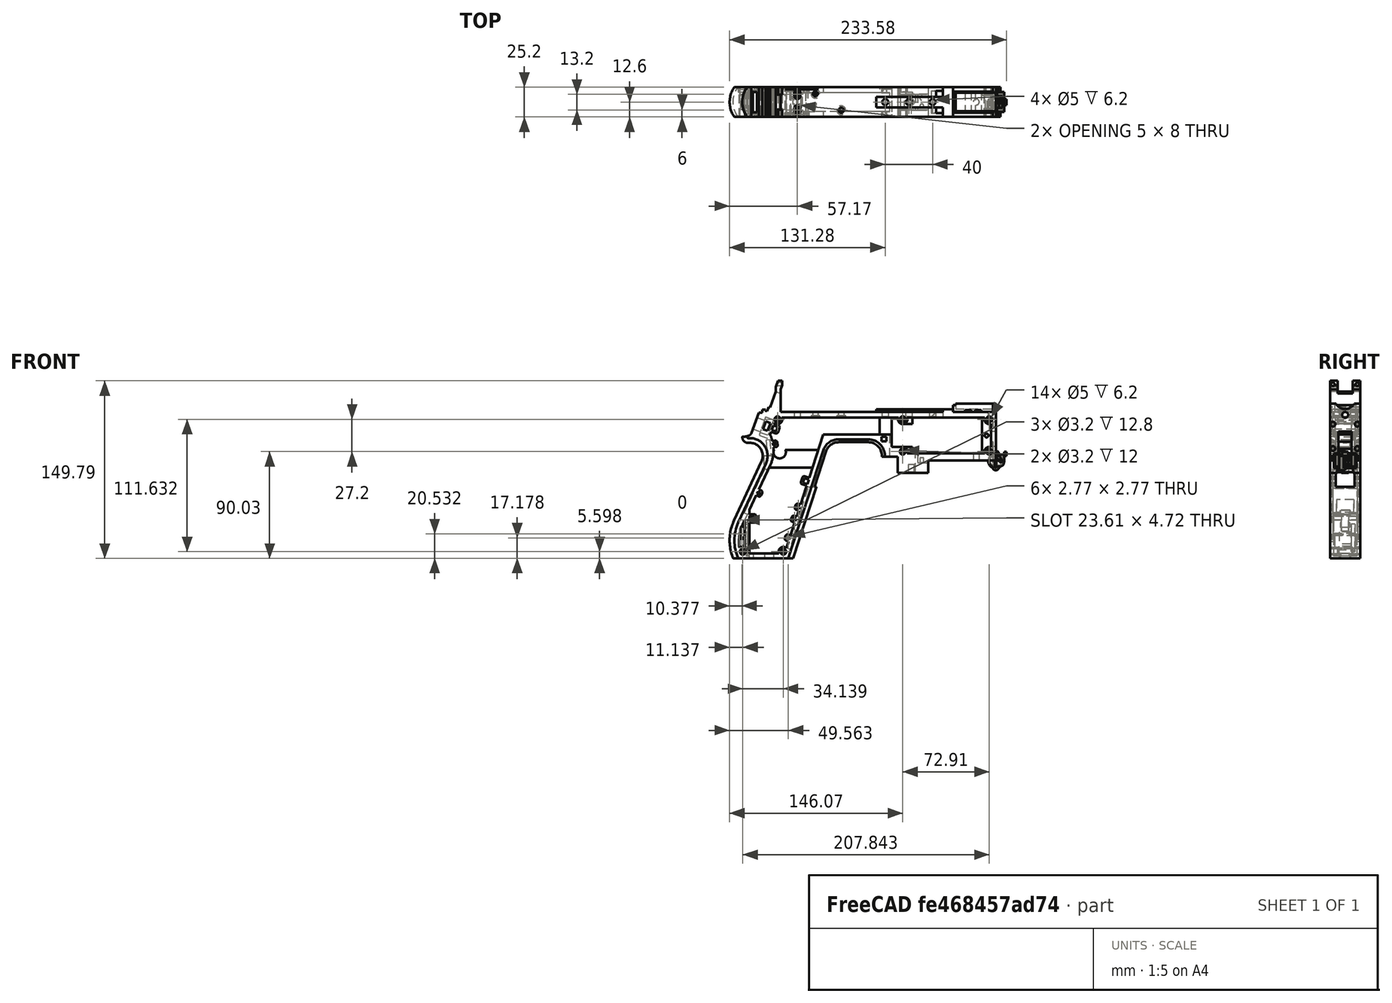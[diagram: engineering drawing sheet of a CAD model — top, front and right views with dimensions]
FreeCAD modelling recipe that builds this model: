
FCSTD DOCUMENT  (FreeCAD 1.0R39319 (Git))
Label: PICON-OF_ver_45
License: All rights reserved
LicenseURL: https://en.wikipedia.org/wiki/All_rights_reserved
objects: Sketcher::SketchObject×119, Part::Extrusion×62, Part::Cut×46, PartDesign::Pad×29, PartDesign::Pocket×18, PartDesign::Chamfer×15, PartDesign::Body×10, PartDesign::Fillet×6, Part::MultiFuse×4, PartDesign::SubtractivePipe×4, Part::Part2DObjectPython×4, PartDesign::SubtractiveLoft×4, PartDesign::Plane×2, PartDesign::SubShapeBinder×2, Part::Sweep×1, PartDesign::ShapeBinder×1, Mesh::Feature×1
note: 598 computed .brp shape members not serialized (recipe doc carries the construction recipe); baked Part::Feature solids carry a one-line shape summary decoded from their .brp

FEATURE [Sketcher::SketchObject] Sketch  label="corpo principale"
  ArcFitTolerance = 1e-06
  AttacherType = Attacher::AttachEngine3D
  AttachmentSupport = -> [XZ_Plane]
  FullyConstrained = true
  MakeInternals = false
  MapMode = 5
  Placement = pos=(0,0,0) rot=(1,0,0;1.5708rad)
  sketch-geometry (65):
    g0: LineSegment StartX=0 StartY=0 StartZ=0 EndX=-57.2 EndY=0 EndZ=0
    g1: LineSegment StartX=-57.2 StartY=0 StartZ=0 EndX=-57.2 EndY=-10.4 EndZ=0
    g2: LineSegment StartX=-57.2 StartY=-10.4 StartZ=0 EndX=-82.8 EndY=-10.4 EndZ=0
    g3: LineSegment StartX=-82.8 StartY=-10.4 StartZ=0 EndX=-82.8 EndY=3.2 EndZ=0
    g4: LineSegment StartX=-82.8 StartY=3.2 StartZ=0 EndX=-93.6 EndY=3.2 EndZ=0
    g5: LineSegment StartX=-93.6 StartY=3.2 StartZ=0 EndX=-93.6 EndY=4 EndZ=0
    g6: LineSegment StartX=-107.6 StartY=18 StartZ=0 EndX=-132.428 EndY=18 EndZ=0
    g7: LineSegment StartX=-145.743 StartY=8.32624 StartZ=0 EndX=-175.232 EndY=-82.4316 EndZ=0
    g8: LineSegment StartX=-175.232 StartY=-82.4316 StartZ=0 EndX=-217.232 EndY=-82.4316 EndZ=0
    g9: LineSegment StartX=-217.232 StartY=-52.1862 StartZ=0 EndX=-193.988 EndY=-2.33927 EndZ=0
    g10: LineSegment StartX=-206.196 StartY=23.0857 StartZ=0 EndX=-199.861 EndY=40.4914 EndZ=0
    g11: LineSegment StartX=-199.861 StartY=40.4914 StartZ=0 EndX=-197.061 EndY=40.4914 EndZ=0
    g12: LineSegment StartX=-197.061 StartY=40.4914 StartZ=0 EndX=-197.061 EndY=42.8914 EndZ=0
    g13: LineSegment StartX=-197.061 StartY=42.8914 StartZ=0 EndX=-194.261 EndY=42.8914 EndZ=0
    g14: LineSegment StartX=-194.261 StartY=42.8914 StartZ=0 EndX=-194.535 EndY=42.1397 EndZ=0
    g15: LineSegment StartX=-194.535 StartY=42.1397 StartZ=0 EndX=-193.031 EndY=41.5924 EndZ=0
    g16: LineSegment StartX=-193.031 StartY=41.5924 StartZ=0 EndX=-191.663 EndY=45.3512 EndZ=0
    g17: LineSegment StartX=-191.663 StartY=45.3512 StartZ=0 EndX=-190.536 EndY=44.9408 EndZ=0
    g18: LineSegment StartX=-190.536 StartY=44.9408 StartZ=0 EndX=-185.747 EndY=58.0965 EndZ=0
    g19: LineSegment StartX=-185.747 StartY=58.0965 StartZ=0 EndX=-185.747 EndY=62.0965 EndZ=0
    g20: LineSegment StartX=-185.747 StartY=62.0965 StartZ=0 EndX=-183.832 EndY=67.3588 EndZ=0
    g21: LineSegment StartX=-183.832 StartY=67.3588 StartZ=0 EndX=-180.232 EndY=67.3588 EndZ=0
    g22: LineSegment StartX=-180.232 StartY=67.3588 StartZ=0 EndX=-180.232 EndY=63.7588 EndZ=0
    g23: LineSegment StartX=-180.232 StartY=63.7588 StartZ=0 EndX=-181.6 EndY=60 EndZ=0
    g24: LineSegment StartX=-181.6 StartY=60 StartZ=0 EndX=-181.6 EndY=41.2 EndZ=0
    g25: LineSegment StartX=-181.6 StartY=41.2 StartZ=0 EndX=-100.8 EndY=41.2 EndZ=0
    g26: LineSegment StartX=-36 StartY=43.2 StartZ=0 EndX=-36 EndY=41.2 EndZ=0
    g27: LineSegment StartX=0 StartY=48 StartZ=0 EndX=0 EndY=0 EndZ=0
    g28: LineSegment StartX=-209.901 StartY=19.85 StartZ=0 EndX=-209.901 EndY=20.1 EndZ=0
    g29: LineSegment StartX=-208.001 StartY=22 StartZ=0 EndX=-207.747 EndY=22 EndZ=0
    g30: LineSegment StartX=-207.583 StartY=19 StartZ=0 EndX=-209.051 EndY=19 EndZ=0
    g31: ArcOfCircle CenterX=-208.001 CenterY=20.1 CenterZ=0 NormalX=0 NormalY=0 NormalZ=1 AngleXU=0 Radius=1.9 StartAngle=1.5708 EndAngle=3.14159
    g32: GeomPoint [constr] X=-209.901 Y=22 Z=0
    g33: ArcOfCircle CenterX=-209.051 CenterY=19.85 CenterZ=0 NormalX=0 NormalY=0 NormalZ=1 AngleXU=0 Radius=0.85 StartAngle=3.14159 EndAngle=4.71239
    g34: GeomPoint [constr] X=-209.901 Y=19 Z=0
    g35: ArcOfCircle CenterX=-207.747 CenterY=23.65 CenterZ=0 NormalX=0 NormalY=0 NormalZ=1 AngleXU=0 Radius=1.65 StartAngle=4.71239 EndAngle=5.93412
    g36: GeomPoint [constr] X=-206.591 Y=22 Z=0
    g37: LineSegment StartX=-4 StartY=6 StartZ=0 EndX=-4 EndY=36.4 EndZ=0
    g38: LineSegment StartX=-4 StartY=36.4 StartZ=0 EndX=-185.2 EndY=36.4 EndZ=0
    g39: LineSegment StartX=-185.2 StartY=36.4 StartZ=0 EndX=-190.441 EndY=22 EndZ=0
    g40: LineSegment StartX=-214.575 StartY=-78.4316 StartZ=0 EndX=-178.142 EndY=-78.4316 EndZ=0
    g41: LineSegment StartX=-178.142 StartY=-78.4316 StartZ=0 EndX=-145.51 EndY=22 EndZ=0
    g42: LineSegment StartX=-145.51 StartY=22 StartZ=0 EndX=-87.91 EndY=22 EndZ=0
    g43: LineSegment StartX=-87.91 StartY=22 StartZ=0 EndX=-87.91 EndY=11.6 EndZ=0
    g44: LineSegment StartX=-87.91 StartY=11.6 StartZ=0 EndX=-80.11 EndY=11.6 EndZ=0
    g45: LineSegment StartX=-80.11 StartY=11.6 StartZ=0 EndX=-80.11 EndY=6 EndZ=0
    g46: LineSegment StartX=-80.11 StartY=6 StartZ=0 EndX=-4 EndY=6 EndZ=0
    g47: LineSegment StartX=-190.363 StartY=-4.02975 StartZ=0 EndX=-213.607 EndY=-53.8767 EndZ=0
    g48: ArcOfCircle CenterX=-132.428 CenterY=4 CenterZ=0 NormalX=0 NormalY=0 NormalZ=1 AngleXU=0 Radius=14 StartAngle=1.5708 EndAngle=2.82743
    g49: GeomPoint [constr] X=-142.6 Y=18 Z=0
    g50: ArcOfCircle CenterX=-107.6 CenterY=4 CenterZ=0 NormalX=0 NormalY=0 NormalZ=1 AngleXU=0 Radius=14 StartAngle=0 EndAngle=1.5708
    g51: GeomPoint [constr] X=-93.6 Y=18 Z=0
    g52: ArcOfCircle CenterX=-184.801 CenterY=-67.3089 CenterZ=0 NormalX=0 NormalY=0 NormalZ=1 AngleXU=0 Radius=35.7833 StartAngle=2.70526 EndAngle=3.57792
    g53: ArcOfCircle CenterX=-207.583 CenterY=4 CenterZ=0 NormalX=0 NormalY=0 NormalZ=1 AngleXU=0 Radius=15 StartAngle=5.84685 EndAngle=7.85398
    g54: LineSegment [constr] StartX=-213.607 StartY=-53.8767 StartZ=0 EndX=-217.232 EndY=-52.1862 EndZ=0
    g55: ArcOfCircle CenterX=-184.801 CenterY=-67.3089 CenterZ=0 NormalX=0 NormalY=0 NormalZ=1 AngleXU=0 Radius=31.7833 StartAngle=2.70526 EndAngle=3.49911
    g56: ArcOfCircle CenterX=-218.095 CenterY=8.90192 CenterZ=0 NormalX=0 NormalY=0 NormalZ=1 AngleXU=0 Radius=30.5989 StartAngle=5.84685 EndAngle=6.72553
    g57: LineSegment StartX=-44.6 StartY=43.2 StartZ=0 EndX=-36 EndY=43.2 EndZ=0
    g58: LineSegment StartX=-100.8 StartY=41.2 StartZ=0 EndX=-44.6 EndY=41.2 EndZ=0
    g59: LineSegment StartX=-44.6 StartY=41.2 StartZ=0 EndX=-44.6 EndY=43.2 EndZ=0
    g60: LineSegment StartX=-2.4 StartY=48 StartZ=0 EndX=0 EndY=48 EndZ=0
    g61: LineSegment StartX=-36 StartY=41.2 StartZ=0 EndX=-2.4 EndY=41.2 EndZ=0
    g62: LineSegment StartX=-2.4 StartY=41.2 StartZ=0 EndX=-2.4 EndY=48 EndZ=0
    g63: LineSegment [constr] StartX=-181.6 StartY=36.4 StartZ=0 EndX=-152.209 EndY=36.4 EndZ=0
    g64: LineSegment [constr] StartX=-181.6 StartY=36.4 StartZ=0 EndX=-130.41 EndY=36.4 EndZ=0
  constraints (183):
    c: Coincident(g-1,g0)
    c: PointOnObject(g0,g-1)
    c: Coincident(g0,g1)
    c: Vertical(g1)
    c: Coincident(g1,g2)
    c: Horizontal(g2)
    c: Coincident(g2,g3)
    c: Vertical(g3)
    c: Coincident(g3,g4)
    c: Coincident(g4,g5)
    c: Vertical(g5)
    c: Horizontal(g6)
    c: Coincident(g7,g8)
    c: Horizontal(g8)
    c: Coincident(g10,g11)
    c: Horizontal(g11)
    c: Coincident(g11,g12)
    c: Vertical(g12)
    c: Coincident(g12,g13)
    c: Horizontal(g13)
    c: Coincident(g13,g14)
    c: Coincident(g14,g15)
    c: Coincident(g15,g16)
    c: Coincident(g16,g17)
    c: Coincident(g17,g18)
    c: Coincident(g18,g19)
    c: Vertical(g19)
    c: Coincident(g19,g20)
    c: Coincident(g20,g21)
    c: Horizontal(g21)
    c: Coincident(g21,g22)
    c: Vertical(g22)
    c: Coincident(g22,g23)
    c: Coincident(g23,g24)
    c: Vertical(g24)
    c: Coincident(g24,g25)
    c: Horizontal(g25)
    c: Coincident(g57,g26)
    c: Vertical(g26)
    c: Coincident(g26,g61)
    c: PointOnObject(g60,g-2)
    c: Coincident(g60,g27)
    c: Coincident(g27,g0)
    c: DistanceY(g27,g27) = 48
    c: DistanceY(g1,g1) = 10.4
    c: DistanceX(g0,g0) = 57.2
    c: DistanceX(g2,g2) = 25.6
    c: Horizontal(g4)
    c: DistanceY(g3,g3) = 13.6
    c: DistanceX(g4,g4) = 10.8
    c: DistanceY(g5,g51) = 14.8
    c: DistanceX(g49,g51) = 49
    c: Distance(g7,g49) = 105.6
    c: DistanceX(g61,g60) = 36
    c: DistanceX(g25,g25) = 80.8
    c: DistanceY(g24,g24) = 18.8
    c: DistanceY(g22,g22) = 3.6
    c: Distance(g23) = 4
    c: Angle(g-1,g23) = 1.22173
    c: DistanceX(g21,g21) = 3.6
    c: Distance(g20) = 5.6
    c: Angle(g-1,g20) = 1.22173
    c: DistanceY(g19,g19) = 4
    c: Distance(g18) = 14
    c: Angle(g-1,g18) = 1.22173
    c: Distance(g17) = 1.2
    c: Distance(g16) = 4
    c: Angle(g16) = 1.22173
    c: Perpendicular(g18,g17)
    c: Distance(g15) = 1.6
    c: Perpendicular(g16,g15)
    c: Distance(g14) = 0.8
    c: DistanceX(g13,g13) = 2.8
    c: Perpendicular(g15,g14)
    c: DistanceY(g12,g12) = 2.4
    c: DistanceX(g11,g11) = 2.8
    c: Distance(g9) = 55
    c: Angle(g9,g-1) = 2.00713
    c: Horizontal(g29)
    c: Vertical(g28)
    c: Horizontal(g30)
    c: PointOnObject(g32,g29)
    c: PointOnObject(g32,g28)
    c: Tangent(g29,g31) = 1.5708
    c: Tangent(g28,g31) = 1.5708
    c: PointOnObject(g34,g28)
    c: PointOnObject(g34,g30)
    c: Tangent(g28,g33) = 1.5708
    c: Tangent(g30,g33) = 1.5708
    c: PointOnObject(g36,g29)
    c: PointOnObject(g36,g10)
    c: Tangent(g29,g35) = -1.5708
    c: Tangent(g10,g35) = -1.5708
    c: Angle(g-1,g10) = 1.22173
    c: Radius(g35) = 1.65
    c: Vertical(g37)
    c: Coincident(g37,g38)
    c: Horizontal(g38)
    c: Coincident(g38,g39)
    c: Horizontal(g40)
    c: Coincident(g40,g41)
    c: Coincident(g41,g42)
    c: Horizontal(g42)
    c: Coincident(g42,g43)
    c: Vertical(g43)
    c: Coincident(g43,g44)
    c: Horizontal(g44)
    c: Coincident(g44,g45)
    c: Vertical(g45)
    c: Coincident(g45,g46)
    c: Coincident(g46,g37)
    c: Horizontal(g46)
    c: DistanceY(g0,g37) = 6
    c: DistanceX(g37,g0) = 4
    c: DistanceY(g37,g25) = 4.8
    c: DistanceX(g38,g38) = 181.2
    c: DistanceX(g42,g42) = 57.6
    c: DistanceY(g49,g41) = 4
    c: DistanceX(g41,g49) = 2.91
    c: DistanceY(g43,g43) = 10.4
    c: DistanceX(g44,g44) = 7.8
    c: DistanceY(g7,g40) = 4
    c: Distance(g47) = 55
    c: Angle(g-1,g39) = 1.22173
    c: PointOnObject(g49,g7)
    c: PointOnObject(g49,g6)
    c: Tangent(g7,g48) = -1.5708
    c: Tangent(g6,g48) = -1.5708
    c: PointOnObject(g51,g5)
    c: PointOnObject(g51,g6)
    c: Tangent(g5,g50) = -1.5708
    c: Tangent(g6,g50) = -1.5708
    c: Radius(g50) = 14
    c: Radius(g48) = 14
    c: DistanceX(g8,g8) = 42
    c: Angle(g7,g-1) = 1.88496
    c: Parallel(g41,g7)
    c: Parallel(g47,g9)
    c: Coincident(g52,g8)
    c: Tangent(g52,g9) = 1.5708
    c: DistanceX(g9,g8) = 0
    c: Tangent(g53,g9) = -1.5708
    c: Tangent(g53,g30) = -1.5708
    c: Diameter(g53) = 30
    c: DistanceY(g53,g0) = -4
    c: Coincident(g54,g47)
    c: Distance(g54) = 4
    c: Coincident(g54,g9)
    c: Coincident(g55,g40)
    c: Tangent(g55,g47) = -1.5708
    c: Coincident(g52,g55)
    c: Coincident(g56,g39)
    c: Tangent(g56,g47) = 1.5708
    c: Horizontal(g57)
    c: DistanceX(g57,g57) = 8.6
    c: Coincident(g58,g25)
    c: Horizontal(g58)
    c: Coincident(g59,g58)
    c: Vertical(g59)
    c: DistanceY(g58,g57) = 2
    c: DistanceX(g58,g58) = 56.2
    c: Coincident(g59,g57)
    c: DistanceY(g41,g36) = 0
    c: DistanceY(g36,g39) = 0
    c: DistanceY(g28,g28) = 0.25
    c: DistanceX(g30,g36) = 2.46
    c: DistanceX(g28,g29) = 1.9
    c: Coincident(g62,g60)
    c: Horizontal(g60)
    c: DistanceX(g62,g27) = 2.4
    c: Coincident(g61,g62)
    c: DistanceY(g26,g26) = 2
    c: Vertical(g62)
    c: DistanceY(g61,g60) = 6.8
    c: Horizontal(g61)
    c: Distance(g63) = 29.391
    c: PointOnObject(g63,g38)
    c: PointOnObject(g63,g38)
    c: Distance(g64) = 51.19
    c: PointOnObject(g64,g38)
    c: PointOnObject(g64,g38)
    c: DistanceX(g24,g63) = 0
    c: DistanceX(g24,g64) = 0
FEATURE [Part::Extrusion] Extrude  label="Extrude corpo principale"
  Base = -> Sketch
  Dir = (0,-1,2e-16)
  DirMode = 2
  FaceMakerClass = Part::FaceMakerBullseye
  FaceMakerMode = 3
  LengthFwd = 25.2
  LengthRev = 12.6
  Solid = true
  Symmetric = true
FEATURE [Sketcher::SketchObject] Sketch002  label="scavo grilletto"
  ArcFitTolerance = 1e-06
  AttachmentSupport = -> [XZ_Plane]
  ExternalGeometry = -> [Sketch]
  FullyConstrained = true
  MakeInternals = false
  MapMode = 5
  Placement = pos=(0,0,0) rot=(1,0,0;1.5708rad)
  sketch-geometry (4):
    g0: LineSegment StartX=-89.51 StartY=22 StartZ=0 EndX=-152.71 EndY=22 EndZ=0
    g1: LineSegment StartX=-152.71 StartY=22 StartZ=0 EndX=-167.006 EndY=-22 EndZ=0
    g2: LineSegment StartX=-167.006 StartY=-22 StartZ=0 EndX=-89.51 EndY=-22 EndZ=0
    g3: LineSegment StartX=-89.51 StartY=-22 StartZ=0 EndX=-89.51 EndY=22 EndZ=0
  constraints (12):
    c: Horizontal(g0)
    c: Coincident(g0,g1)
    c: Coincident(g1,g2)
    c: Horizontal(g2)
    c: Coincident(g2,g3)
    c: Coincident(g3,g0)
    c: Vertical(g3)
    c: Angle(g1,g0) = 1.88496
    c: DistanceY(g3,g3) = 44
    c: DistanceX(g0,g0) = 63.2
    c: DistanceX(g0,g-3) = 1.6
    c: DistanceY(g-3,g0) = 0
FEATURE [Sketcher::SketchObject] Sketch004  label="traiettoria arrotondamento impugnatura anteriore"
  ArcFitTolerance = 1e-06
  AttachmentSupport = -> [XZ_Plane]
  ExternalGeometry = -> [Sketch]
  FullyConstrained = true
  MakeInternals = false
  MapMode = 5
  Placement = pos=(0,0,0) rot=(1,0,0;1.5708rad)
  sketch-geometry (13):
    g0: LineSegment StartX=-175.232 StartY=-82.4316 StartZ=0 EndX=-145.743 EndY=8.32624 EndZ=0
    g1: LineSegment StartX=-93.6 StartY=3.2 StartZ=0 EndX=-93.6 EndY=4 EndZ=0
    g2: LineSegment StartX=-132.428 StartY=18 StartZ=0 EndX=-107.6 EndY=18 EndZ=0
    g3: ArcOfCircle CenterX=-132.428 CenterY=4 CenterZ=0 NormalX=0 NormalY=0 NormalZ=1 AngleXU=0 Radius=14 StartAngle=1.5708 EndAngle=2.82743
    g4: ArcOfCircle CenterX=-107.6 CenterY=4 CenterZ=0 NormalX=0 NormalY=0 NormalZ=1 AngleXU=0 Radius=14 StartAngle=0 EndAngle=1.5708
    g5: LineSegment StartX=-175.232 StartY=-82.4316 StartZ=0 EndX=-217.232 EndY=-82.4316 EndZ=0
    g6: LineSegment StartX=-217.232 StartY=-52.1862 StartZ=0 EndX=-193.988 EndY=-2.33927 EndZ=0
    g7: LineSegment StartX=-209.051 StartY=19 StartZ=0 EndX=-207.583 EndY=19 EndZ=0
    g8: LineSegment StartX=-209.901 StartY=20.1 StartZ=0 EndX=-209.901 EndY=19.85 EndZ=0
    g9: ArcOfCircle CenterX=-184.801 CenterY=-67.3089 CenterZ=0 NormalX=0 NormalY=0 NormalZ=1 AngleXU=0 Radius=35.7833 StartAngle=2.70526 EndAngle=3.57792
    g10: ArcOfCircle CenterX=-207.583 CenterY=4 CenterZ=0 NormalX=0 NormalY=0 NormalZ=1 AngleXU=0 Radius=15 StartAngle=5.84685 EndAngle=7.85398
    g11: ArcOfCircle CenterX=-209.051 CenterY=19.85 CenterZ=0 NormalX=0 NormalY=0 NormalZ=1 AngleXU=0 Radius=0.85 StartAngle=3.14159 EndAngle=4.71239
    g12: ArcOfCircle CenterX=-208.001 CenterY=20.1 CenterZ=0 NormalX=0 NormalY=0 NormalZ=1 AngleXU=0 Radius=1.9 StartAngle=1.5708 EndAngle=3.14159
  constraints (26):
    c: Coincident(g0,g-3)
    c: Coincident(g0,g-6)
    c: Coincident(g1,g-8)
    c: Coincident(g1,g-7)
    c: Coincident(g2,g-5)
    c: Coincident(g2,g-4)
    c: Coincident(g3,g2)
    c: Tangent(g3,g0) = 1.5708
    c: Coincident(g4,g1)
    c: Tangent(g4,g2) = 1.5708
    c: Coincident(g5,g0)
    c: Coincident(g5,g-9)
    c: Coincident(g6,g-12)
    c: Coincident(g6,g-11)
    c: Coincident(g7,g-15)
    c: Coincident(g7,g-14)
    c: Coincident(g8,g-16)
    c: Coincident(g8,g-17)
    c: Tangent(g9,g6) = 1.5708
    c: Coincident(g9,g5)
    c: Coincident(g10,g7)
    c: Tangent(g10,g6) = -1.5708
    c: Tangent(g11,g7) = -1.5708
    c: Coincident(g11,g8)
    c: Tangent(g12,g8) = -1.5708
    c: Coincident(g12,g-17)
FEATURE [PartDesign::Plane] DatumPlane  label="Piano per disegno arrotondamento impugnatura"
  AttachmentSupport = -> [Sketch]
  Length = 73.6581
  MapMode = 7
  Placement = pos=(-145.743,1.8e-15,8.32624) rot=(0.154555,0.154555,0.97582;1.59527rad)
  ResizeMode = 0
  Width = 303.511
FEATURE [Sketcher::SketchObject] Sketch005  label="forma arrotondamento impugnatura anteriore"
  ArcFitTolerance = 1e-06
  AttachmentSupport = -> [DatumPlane]
  FullyConstrained = true
  MakeInternals = false
  MapMode = 5
  Placement = pos=(-145.743,1.8e-15,8.32624) rot=(0.154555,0.154555,0.97582;1.59527rad)
  sketch-geometry (5):
    g0: GeomPoint [constr] X=0 Y=-4 Z=0
    g1: GeomPoint [constr] X=-12.6 Y=7.1e-15 Z=0
    g2: GeomPoint [constr] X=12.6 Y=4.97e-14 Z=0
    g3: LineSegment StartX=-12.6 StartY=7.1e-15 StartZ=0 EndX=12.6 EndY=4.97e-14 EndZ=0
    g4: ArcOfCircle CenterX=-3.88e-14 CenterY=17.845 CenterZ=0 NormalX=0 NormalY=0 NormalZ=1 AngleXU=0 Radius=21.845 StartAngle=4.09759 EndAngle=5.32718
  constraints (11):
    c: DistanceY(g0,g-1) = 4
    c: DistanceX(g-1,g0) = 0
    c: DistanceX(g1,g-1) = 12.6
    c: DistanceX(g-1,g2) = 12.6
    c: DistanceY(g-1,g2) = 0
    c: DistanceY(g-1,g1) = 0
    c: Coincident(g3,g1)
    c: Coincident(g3,g2)
    c: Coincident(g4,g1)
    c: Coincident(g4,g2)
    c: PointOnObject(g0,g4)
FEATURE [Part::Sweep] Sweep  label="Sweep impugnatura"
  Frenet = true
  Sections = -> [Sketch005]
  Solid = true
  Spine = -> Sketch [Edge32,Edge33,Edge34,Edge35,Edge36,Edge37,Edge38,Edge39,Edge40,Edge41,Edge42,Edge43,Edge44]
  Transition = 1
FEATURE [Sketcher::SketchObject] Sketch008  label="buchi e pulizie varie"
  ArcFitTolerance = 1e-06
  AttachmentSupport = -> [XZ_Plane]
  ExternalGeometry = -> [Sketch]
  FullyConstrained = true
  MakeInternals = false
  MapMode = 5
  Placement = pos=(0,0,0) rot=(1,0,0;1.5708rad)
  sketch-geometry (26):
    g0: LineSegment StartX=-96.278 StartY=20.155 StartZ=0 EndX=-92.278 EndY=20.155 EndZ=0
    g1: LineSegment StartX=-92.278 StartY=20.155 StartZ=0 EndX=-92.278 EndY=16.155 EndZ=0
    g2: LineSegment StartX=-92.278 StartY=16.155 StartZ=0 EndX=-96.278 EndY=16.155 EndZ=0
    g3: LineSegment StartX=-96.278 StartY=16.155 StartZ=0 EndX=-96.278 EndY=20.155 EndZ=0
    g4: LineSegment StartX=-222.232 StartY=-82.4316 StartZ=0 EndX=-170.232 EndY=-82.4316 EndZ=0
    g5: LineSegment StartX=-170.232 StartY=-82.4316 StartZ=0 EndX=-170.232 EndY=-86.4316 EndZ=0
    g6: LineSegment StartX=-170.232 StartY=-86.4316 StartZ=0 EndX=-222.232 EndY=-86.4316 EndZ=0
    g7: LineSegment StartX=-222.232 StartY=-86.4316 StartZ=0 EndX=-222.232 EndY=-82.4316 EndZ=0
    g8: LineSegment StartX=-213.901 StartY=20.1 StartZ=0 EndX=-213.901 EndY=26 EndZ=0
    g9: LineSegment StartX=-213.901 StartY=26 StartZ=0 EndX=-206.196 EndY=26 EndZ=0
    g10: LineSegment StartX=-17.4 StartY=42.8 StartZ=0 EndX=-12.4 EndY=42.8 EndZ=0
    g11: LineSegment StartX=-12.4 StartY=42.8 StartZ=0 EndX=-12.4 EndY=41.2 EndZ=0
    g12: LineSegment StartX=-12.4 StartY=41.2 StartZ=0 EndX=-17.4 EndY=41.2 EndZ=0
    g13: LineSegment StartX=-17.4 StartY=41.2 StartZ=0 EndX=-17.4 EndY=42.8 EndZ=0
    g14: LineSegment StartX=-25.9 StartY=42.8 StartZ=0 EndX=-20.9 EndY=42.8 EndZ=0
    g15: LineSegment StartX=-20.9 StartY=42.8 StartZ=0 EndX=-20.9 EndY=41.2 EndZ=0
    g16: LineSegment StartX=-20.9 StartY=41.2 StartZ=0 EndX=-25.9 EndY=41.2 EndZ=0
    g17: LineSegment StartX=-25.9 StartY=41.2 StartZ=0 EndX=-25.9 EndY=42.8 EndZ=0
    g18: GeomPoint [constr] X=-206.196 Y=23.0857 Z=0
    g19: GeomPoint [constr] X=-213.901 Y=20.1 Z=0
    g20: BSplineCurve PolesCount=4 KnotsCount=2 Degree=3 IsPeriodic=0
    g21-g24: Circle [constr] x4 (B-spline internal-alignment scaffolding for g20; pole/knot coordinates omitted)
    g25: LineSegment StartX=-206.196 StartY=26 StartZ=0 EndX=-206.196 EndY=23.0857 EndZ=0
  constraints (73):
    c: Horizontal(g0)
    c: Coincident(g1,g0)
    c: Vertical(g1)
    c: Coincident(g2,g1)
    c: Horizontal(g2)
    c: Coincident(g3,g2)
    c: Coincident(g3,g0)
    c: Vertical(g3)
    c: DistanceX(g0,g-4) = 4.368
    c: DistanceY(g0,g-4) = 1.845
    c: DistanceY(g1,g1) = 4
    c: DistanceX(g2,g2) = 4
    c: Horizontal(g4)
    c: Coincident(g5,g4)
    c: Vertical(g5)
    c: Coincident(g6,g5)
    c: Horizontal(g6)
    c: Coincident(g7,g6)
    c: Coincident(g7,g4)
    c: Vertical(g7)
    c: DistanceY(g7,g7) = 4
    c: DistanceX(g4,g-5) = 5
    c: DistanceX(g-5,g4) = 5
    c: DistanceY(g4,g-5) = 0
    c: Coincident(g9,g8)
    c: Parallel(g9,g-6)
    c: DistanceX(g8,g-8) = 4
    c: Horizontal(g10)
    c: Coincident(g11,g10)
    c: Vertical(g11)
    c: Coincident(g12,g11)
    c: Horizontal(g12)
    c: Coincident(g13,g12)
    c: Coincident(g13,g10)
    c: Vertical(g13)
    c: Horizontal(g14)
    c: Coincident(g15,g14)
    c: Vertical(g15)
    c: Coincident(g16,g15)
    c: Horizontal(g16)
    c: Coincident(g17,g16)
    c: Coincident(g17,g14)
    c: Vertical(g17)
    c: DistanceY(g11,g10) = 1.6
    c: DistanceX(g10,g10) = 5
    c: DistanceY(g15,g14) = 1.6
    c: DistanceX(g14,g14) = 5
    c: DistanceX(g15,g12) = 3.5
    c: DistanceX(g11,g-9) = 10
    c: DistanceY(g-9,g11) = 0
    c: DistanceY(g-9,g15) = 0
    c: Perpendicular(g8,g9)
    c: DistanceY(g-7,g9) = 4
    c: DistanceY(g8,g-8) = 0
    c: InternalAlignment(g18,g20)
    c: InternalAlignment(g19,g20)
    c: InternalAlignment(g21,g20)
    c: Weight(g21) = 1
    c: InternalAlignment(g22,g20)
    c: Equal(g22,g21)
    c: InternalAlignment(g23,g20)
    c: Equal(g23,g21)
    c: InternalAlignment(g24,g20)
    c: Equal(g24,g21)
    c: Coincident(g18,g-12)
    c: Coincident(g19,g8)
    c: Coincident(g25,g9)
    c: Coincident(g25,g20)
    c: Vertical(g25)
    c: DistanceY(g20,g23) = 0
    c: DistanceY(g22,g18) = 2.26
    c: DistanceX(g22,g18) = 0.93
    c: DistanceX(g20,g23) = 2.9
FEATURE [Part::Extrusion] Extrude004  label="Extrude Buchi e pulizie varie"
  Base = -> Sketch008
  Dir = (0,-1,2e-16)
  DirMode = 2
  FaceMakerClass = Part::FaceMakerBullseye
  FaceMakerMode = 3
  LengthFwd = 25.2
  LengthRev = 0
  Solid = true
  Symmetric = true
FEATURE [Sketcher::SketchObject] Sketch009  label="rinforzi"
  ArcFitTolerance = 1e-06
  AttachmentSupport = -> [XZ_Plane]
  ExternalGeometry = -> [Sketch]
  FullyConstrained = true
  MakeInternals = false
  MapMode = 5
  Placement = pos=(0,0,0) rot=(1,0,0;1.5708rad)
  sketch-geometry (9):
    g0: LineSegment StartX=-87.91 StartY=22 StartZ=0 EndX=-87.91 EndY=36.4 EndZ=0
    g1: LineSegment StartX=-87.91 StartY=36.4 StartZ=0 EndX=-97.91 EndY=36.4 EndZ=0
    g2: LineSegment StartX=-97.91 StartY=36.4 StartZ=0 EndX=-97.91 EndY=22 EndZ=0
    g3: LineSegment StartX=-97.91 StartY=22 StartZ=0 EndX=-87.91 EndY=22 EndZ=0
    g4: LineSegment StartX=-149.713 StartY=9.06563 StartZ=0 EndX=-154.586 EndY=-5.93437 EndZ=0
    g5: LineSegment StartX=-154.586 StartY=-5.93437 StartZ=0 EndX=-191.863 EndY=-5.93437 EndZ=0
    g6: LineSegment StartX=-191.863 StartY=-5.93437 StartZ=0 EndX=-191.863 EndY=9.06563 EndZ=0
    g7: LineSegment StartX=-191.863 StartY=9.06563 StartZ=0 EndX=-149.713 EndY=9.06563 EndZ=0
    g8: LineSegment [constr] StartX=-145.51 StartY=22 StartZ=0 EndX=-149.713 EndY=9.06563 EndZ=0
  constraints (25):
    c: Vertical(g0)
    c: Coincident(g1,g0)
    c: Horizontal(g1)
    c: Coincident(g2,g1)
    c: Vertical(g2)
    c: Coincident(g3,g2)
    c: Coincident(g3,g0)
    c: Horizontal(g3)
    c: Coincident(g0,g-4)
    c: DistanceX(g3,g3) = 10
    c: DistanceY(g0,g-3) = 0
    c: Coincident(g5,g4)
    c: Horizontal(g5)
    c: Coincident(g6,g5)
    c: Vertical(g6)
    c: Coincident(g7,g6)
    c: Coincident(g7,g4)
    c: Horizontal(g7)
    c: Distance(g8) = 13.6
    c: Parallel(g-6,g8)
    c: Coincident(g-6,g8)
    c: Parallel(g4,g-6)
    c: DistanceY(g4,g4) = 15
    c: Coincident(g4,g8)
    c: DistanceX(g-5,g5) = -1.5
FEATURE [Part::Extrusion] Extrude001  label="Extrude scavo grilletto"
  Base = -> Sketch002
  Dir = (0,-1,2e-16)
  DirMode = 2
  FaceMakerClass = Part::FaceMakerBullseye
  FaceMakerMode = 3
  LengthFwd = 16
  LengthRev = 0
  Solid = true
  Symmetric = true
FEATURE [Part::Extrusion] Extrude005  label="Extrude Rinforzi"
  Base = -> Sketch009
  Dir = (0,-1,2e-16)
  DirMode = 2
  FaceMakerClass = Part::FaceMakerBullseye
  FaceMakerMode = 3
  LengthFwd = 2
  LengthRev = 0
  Placement = pos=(0,12.6,0) rot=(0,0,1;0rad)
  Solid = true
  Symmetric = false
FEATURE [PartDesign::ShapeBinder] CopyCut
  TraceSupport = false
FEATURE [PartDesign::Plane] DatumPlane001
  AttachmentSupport = -> [CopyCut]
  Length = 283.944
  MapMode = 5
  Placement = pos=(0,12.6,0) rot=(0,0.707107,0.707107;3.14159rad)
  ResizeMode = 0
  Width = 188.15
FEATURE [Sketcher::SketchObject] Sketch010  label="buco neopixel"
  ArcFitTolerance = 1e-06
  AttachmentSupport = -> [XZ_Plane]
  ExternalGeometry = -> [Sketch]
  FullyConstrained = true
  MakeInternals = false
  MapMode = 5
  Placement = pos=(0,0,0) rot=(1,0,0;1.5708rad)
  sketch-geometry (5):
    g0: LineSegment [constr] StartX=-199.861 StartY=40.4914 StartZ=0 EndX=-201.368 EndY=36.3521 EndZ=0
    g1: LineSegment StartX=-201.368 StartY=36.3521 StartZ=0 EndX=-204.932 EndY=26.5605 EndZ=0
    g2: LineSegment StartX=-201.368 StartY=36.3521 StartZ=0 EndX=-180.2 EndY=28.6477 EndZ=0
    g3: LineSegment StartX=-180.2 StartY=28.6477 StartZ=0 EndX=-183.764 EndY=18.8561 EndZ=0
    g4: LineSegment StartX=-183.764 StartY=18.8561 StartZ=0 EndX=-204.932 EndY=26.5605 EndZ=0
  constraints (14):
    c: Parallel(g0,g-3)
    c: Distance(g0) = 4.405
    c: Coincident(g0,g-3)
    c: Coincident(g2,g1)
    c: Coincident(g3,g2)
    c: Coincident(g4,g3)
    c: Coincident(g4,g1)
    c: Parallel(g1,g-3)
    c: Distance(g1) = 10.42
    c: Coincident(g1,g0)
    c: Parallel(g2,g4)
    c: Perpendicular(g1,g2)
    c: DistanceX(g-4,g2) = 5
    c: Parallel(g3,g1)
FEATURE [Part::Extrusion] Extrude006  label="Extrude buco neopixel"
  Base = -> Sketch010
  Dir = (0,-1,2e-16)
  DirMode = 2
  FaceMakerClass = Part::FaceMakerBullseye
  FaceMakerMode = 3
  LengthFwd = 17.2
  LengthRev = 0
  Solid = true
  Symmetric = true
FEATURE [Sketcher::SketchObject] Sketch011  label="fermo grilletto"
  ArcFitTolerance = 1e-06
  AttachmentSupport = -> [XZ_Plane]
  ExternalGeometry = -> [Sketch]
  FullyConstrained = true
  MakeInternals = false
  MapMode = 5
  Placement = pos=(0,0,0) rot=(1,0,0;1.5708rad)
  sketch-geometry (18):
    g0: LineSegment [constr] StartX=-145.51 StartY=22 StartZ=0 EndX=-157.347 EndY=-14.4293 EndZ=0
    g1: LineSegment [constr] StartX=-157.347 StartY=-14.4293 StartZ=0 EndX=-157.841 EndY=-15.951 EndZ=0
    g2: LineSegment StartX=-161.151 StartY=-13.1932 StartZ=0 EndX=-155.825 EndY=-14.9237 EndZ=0
    g3: LineSegment StartX=-163.167 StartY=-14.2205 StartZ=0 EndX=-164.403 EndY=-18.0247 EndZ=0
    g4: LineSegment StartX=-163.376 StartY=-20.0408 StartZ=0 EndX=-158.05 EndY=-21.7713 EndZ=0
    g5: LineSegment StartX=-158.05 StartY=-21.7713 StartZ=0 EndX=-155.825 EndY=-14.9237 EndZ=0
    g6: LineSegment StartX=-161.645 StartY=-14.7149 StartZ=0 EndX=-157.841 EndY=-15.951 EndZ=0
    g7: LineSegment StartX=-157.841 StartY=-15.951 StartZ=0 EndX=-159.077 EndY=-19.7552 EndZ=0
    g8: LineSegment StartX=-159.077 StartY=-19.7552 StartZ=0 EndX=-162.881 EndY=-18.5191 EndZ=0
    g9: LineSegment StartX=-162.881 StartY=-18.5191 StartZ=0 EndX=-161.645 EndY=-14.7149 EndZ=0
    g10: LineSegment [constr] StartX=-161.645 StartY=-14.7149 StartZ=0 EndX=-161.151 EndY=-13.1932 EndZ=0
    g11: LineSegment [constr] StartX=-159.077 StartY=-19.7552 StartZ=0 EndX=-157.555 EndY=-20.2496 EndZ=0
    g12: LineSegment [constr] StartX=-159.077 StartY=-19.7552 StartZ=0 EndX=-159.572 EndY=-21.2769 EndZ=0
    g13: LineSegment [constr] StartX=-161.645 StartY=-14.7149 StartZ=0 EndX=-163.167 EndY=-14.2205 EndZ=0
    g14: ArcOfCircle CenterX=-161.645 CenterY=-14.7149 CenterZ=0 NormalX=0 NormalY=0 NormalZ=1 AngleXU=0 Radius=1.6 StartAngle=1.25664 EndAngle=2.82743
    g15: GeomPoint [constr] X=-162.673 Y=-12.6988 Z=0
    g16: ArcOfCircle CenterX=-162.881 CenterY=-18.5191 CenterZ=0 NormalX=0 NormalY=0 NormalZ=1 AngleXU=0 Radius=1.6 StartAngle=2.82743 EndAngle=4.39823
    g17: GeomPoint [constr] X=-164.897 Y=-19.5464 Z=0
  constraints (48):
    c: Parallel(g0,g-3)
    c: Distance(g0) = 38.304
    c: Coincident(g0,g-3)
    c: Parallel(g1,g-3)
    c: Distance(g1) = 1.6
    c: Coincident(g1,g0)
    c: Coincident(g5,g4)
    c: Coincident(g5,g2)
    c: Coincident(g7,g6)
    c: Coincident(g8,g7)
    c: Coincident(g9,g8)
    c: Coincident(g9,g6)
    c: Parallel(g7,g-3)
    c: Parallel(g9,g7)
    c: Perpendicular(g6,g7)
    c: Parallel(g6,g8)
    c: Distance(g6) = 4
    c: Distance(g9) = 4
    c: Parallel(g5,g7)
    c: Parallel(g9,g3)
    c: Parallel(g2,g6)
    c: Parallel(g4,g8)
    c: Parallel(g13,g6)
    c: Parallel(g10,g9)
    c: Parallel(g11,g8)
    c: Parallel(g12,g7)
    c: Distance(g10) = 1.6
    c: Distance(g13) = 1.6
    c: Distance(g12) = 1.6
    c: Distance(g11) = 1.6
    c: Coincident(g10,g6)
    c: Coincident(g13,g6)
    c: Coincident(g12,g7)
    c: Coincident(g11,g7)
    c: Distance(g10,g15) = 1.6
    c: Distance(g15,g13) = 1.6
    c: Distance(g4,g12) = 1.6
    c: Distance(g4,g11) = 1.6
    c: PointOnObject(g15,g2)
    c: Tangent(g3,g14) = -1.5708
    c: Tangent(g2,g14) = 1.5708
    c: PointOnObject(g17,g4)
    c: PointOnObject(g17,g3)
    c: Tangent(g4,g16) = -1.5708
    c: Tangent(g3,g16) = -1.5708
    c: Equal(g16,g14)
    c: Coincident(g16,g8)
    c: Coincident(g6,g1)
FEATURE [Part::Extrusion] Extrude007  label="Extrude fermo grilletto"
  Base = -> Sketch011
  Dir = (0,-1,2e-16)
  DirMode = 2
  FaceMakerClass = Part::FaceMakerBullseye
  FaceMakerMode = 3
  LengthFwd = 25.2
  LengthRev = 0
  Solid = true
  Symmetric = true
FEATURE [Sketcher::SketchObject] Sketch012  label="buco oled"
  ArcFitTolerance = 1e-06
  AttachmentSupport = -> [XZ_Plane]
  ExternalGeometry = -> [Sketch]
  FullyConstrained = true
  MakeInternals = false
  MapMode = 5
  Placement = pos=(0,0,0) rot=(1,0,0;1.5708rad)
  sketch-geometry (4):
    g0: LineSegment StartX=-185.747 StartY=58.0965 StartZ=0 EndX=-180.232 EndY=56.0891 EndZ=0
    g1: LineSegment StartX=-185.747 StartY=58.0965 StartZ=0 EndX=-185.747 EndY=67.3588 EndZ=0
    g2: LineSegment StartX=-185.747 StartY=67.3588 StartZ=0 EndX=-180.232 EndY=67.3588 EndZ=0
    g3: LineSegment StartX=-180.232 StartY=67.3588 StartZ=0 EndX=-180.232 EndY=56.0891 EndZ=0
  constraints (10):
    c: Coincident(g1,g0)
    c: Coincident(g2,g1)
    c: Coincident(g3,g2)
    c: Coincident(g3,g0)
    c: Parallel(g1,g-5)
    c: Perpendicular(g-3,g0)
    c: Parallel(g2,g-6)
    c: Parallel(g3,g-4)
    c: Coincident(g0,g-5)
    c: Coincident(g2,g-6)
FEATURE [Part::Extrusion] Extrude008  label="Extrude buco oled"
  Base = -> Sketch012
  Dir = (0,-1,2e-16)
  DirMode = 2
  FaceMakerClass = Part::FaceMakerBullseye
  FaceMakerMode = 3
  LengthFwd = 12.8
  LengthRev = 0
  Solid = true
  Symmetric = true
FEATURE [Sketcher::SketchObject] Sketch013  label="buco pompa"
  ArcFitTolerance = 1e-06
  AttachmentSupport = -> [XZ_Plane]
  ExternalGeometry = -> [Sketch]
  FullyConstrained = true
  MakeInternals = false
  MapMode = 5
  Placement = pos=(0,0,0) rot=(1,0,0;1.5708rad)
  sketch-geometry (8):
    g0: LineSegment StartX=-82.8 StartY=-10.4 StartZ=0 EndX=-82.8 EndY=-9.6 EndZ=0
    g1: LineSegment StartX=-82.8 StartY=-9.6 StartZ=0 EndX=-67.9 EndY=-9.6 EndZ=0
    g2: LineSegment StartX=-67.9 StartY=-9.6 StartZ=0 EndX=-67.9 EndY=6 EndZ=0
    g3: LineSegment StartX=-67.9 StartY=6 StartZ=0 EndX=-65.9 EndY=6 EndZ=0
    g4: LineSegment StartX=-65.9 StartY=6 StartZ=0 EndX=-65.9 EndY=-1.7 EndZ=0
    g5: LineSegment StartX=-65.9 StartY=-1.7 StartZ=0 EndX=-57.2 EndY=-1.7 EndZ=0
    g6: LineSegment StartX=-57.2 StartY=-1.7 StartZ=0 EndX=-57.2 EndY=-10.4 EndZ=0
    g7: LineSegment StartX=-57.2 StartY=-10.4 StartZ=0 EndX=-82.8 EndY=-10.4 EndZ=0
  constraints (22):
    c: Vertical(g0)
    c: Coincident(g1,g0)
    c: Horizontal(g1)
    c: Coincident(g2,g1)
    c: Vertical(g2)
    c: Coincident(g3,g2)
    c: Horizontal(g3)
    c: Coincident(g4,g3)
    c: Vertical(g4)
    c: Coincident(g5,g4)
    c: Horizontal(g5)
    c: Coincident(g6,g5)
    c: Vertical(g6)
    c: Coincident(g7,g6)
    c: Coincident(g7,g0)
    c: DistanceY(g0,g0) = 0.8
    c: DistanceY(g6,g6) = 8.7
    c: DistanceX(g1,g1) = 14.9
    c: DistanceX(g3,g3) = 2
    c: Coincident(g0,g-4)
    c: DistanceY(g2,g-6) = 0
    c: Coincident(g6,g-5)
FEATURE [Part::Extrusion] Extrude009  label="Extrude buco pompa"
  Base = -> Sketch013
  Dir = (0,-1,2e-16)
  DirMode = 2
  FaceMakerClass = Part::FaceMakerBullseye
  FaceMakerMode = 3
  LengthFwd = 13.2
  LengthRev = 0
  Solid = true
  Symmetric = true
FEATURE [Sketcher::SketchObject] Sketch014  label="buco frontale"
  ArcFitTolerance = 1e-06
  AttachmentSupport = -> [XZ_Plane]
  ExternalGeometry = -> [Sketch]
  FullyConstrained = true
  MakeInternals = false
  MapMode = 5
  Placement = pos=(0,0,0) rot=(1,0,0;1.5708rad)
  sketch-geometry (10):
    g0: LineSegment StartX=0 StartY=0 StartZ=0 EndX=0 EndY=24.671 EndZ=0
    g1: LineSegment StartX=0 StartY=24.671 StartZ=0 EndX=-4 EndY=24.671 EndZ=0
    g2: LineSegment StartX=-4 StartY=24.671 StartZ=0 EndX=-4 EndY=16 EndZ=0
    g3: LineSegment StartX=-4 StartY=16 StartZ=0 EndX=-2.4 EndY=16 EndZ=0
    g4: LineSegment StartX=-2.4 StartY=16 StartZ=0 EndX=-2.4 EndY=10 EndZ=0
    g5: LineSegment StartX=-2.4 StartY=10 StartZ=0 EndX=-12 EndY=10 EndZ=0
    g6: LineSegment StartX=-12 StartY=10 StartZ=0 EndX=-12 EndY=6 EndZ=0
    g7: LineSegment StartX=-12 StartY=6 StartZ=0 EndX=-2.4 EndY=6 EndZ=0
    g8: LineSegment StartX=-2.4 StartY=6 StartZ=0 EndX=-2.4 EndY=0 EndZ=0
    g9: LineSegment StartX=-2.4 StartY=0 StartZ=0 EndX=0 EndY=0 EndZ=0
  constraints (29):
    c: Vertical(g0)
    c: Coincident(g1,g0)
    c: Horizontal(g1)
    c: Coincident(g2,g1)
    c: Vertical(g2)
    c: Coincident(g3,g2)
    c: Horizontal(g3)
    c: Coincident(g4,g3)
    c: Vertical(g4)
    c: Coincident(g5,g4)
    c: Horizontal(g5)
    c: Coincident(g6,g5)
    c: Vertical(g6)
    c: Coincident(g7,g6)
    c: Coincident(g8,g7)
    c: Vertical(g8)
    c: Coincident(g9,g8)
    c: Coincident(g9,g0)
    c: Horizontal(g9)
    c: DistanceY(g0,g0) = 24.671
    c: Horizontal(g7)
    c: DistanceY(g6,g6) = 4
    c: DistanceY(g4,g4) = 6
    c: DistanceX(g9,g9) = 2.4
    c: Coincident(g0,g-1)
    c: DistanceY(g-3,g7) = 0
    c: DistanceX(g8,g4) = 0
    c: DistanceX(g-3,g1) = 0
    c: DistanceX(g6,g-3) = 8
FEATURE [Part::Extrusion] Extrude010  label="Extrude buco frontale"
  Base = -> Sketch014
  Dir = (0,-1,2e-16)
  DirMode = 2
  FaceMakerClass = Part::FaceMakerBullseye
  FaceMakerMode = 3
  LengthFwd = 11.2
  LengthRev = 0
  Solid = true
  Symmetric = true
FEATURE [Sketcher::SketchObject] Sketch015  label="guida rail"
  ArcFitTolerance = 1e-06
  AttachmentSupport = -> [XZ_Plane]
  ExternalGeometry = -> [Sketch]
  FullyConstrained = true
  MakeInternals = false
  MapMode = 5
  Placement = pos=(0,0,0) rot=(1,0,0;1.5708rad)
  sketch-geometry (4):
    g0: LineSegment StartX=-100.8 StartY=43.2 StartZ=0 EndX=-44.6 EndY=43.2 EndZ=0
    g1: LineSegment StartX=-44.6 StartY=43.2 StartZ=0 EndX=-44.6 EndY=41.2 EndZ=0
    g2: LineSegment StartX=-44.6 StartY=41.2 StartZ=0 EndX=-100.8 EndY=41.2 EndZ=0
    g3: LineSegment StartX=-100.8 StartY=41.2 StartZ=0 EndX=-100.8 EndY=43.2 EndZ=0
  constraints (9):
    c: Horizontal(g0)
    c: Coincident(g1,g0)
    c: Coincident(g2,g1)
    c: Coincident(g3,g2)
    c: Coincident(g3,g0)
    c: Vertical(g3)
    c: Coincident(g2,g-3)
    c: Coincident(g1,g-3)
    c: Coincident(g0,g-4)
FEATURE [Part::Extrusion] Extrude011  label="Extrude guida rail"
  Base = -> Sketch015
  Dir = (0,-1,2e-16)
  DirMode = 2
  FaceMakerClass = Part::FaceMakerBullseye
  FaceMakerMode = 3
  LengthFwd = 9
  LengthRev = 0
  Solid = true
  Symmetric = true
FEATURE [Sketcher::SketchObject] Sketch016  label="guide per coperture laterali"
  ArcFitTolerance = 1e-06
  AttachmentSupport = -> [XZ_Plane]
  ExternalGeometry = -> [Sketch]
  FullyConstrained = true
  MakeInternals = false
  MapMode = 5
  Placement = pos=(0,0,0) rot=(1,0,0;1.5708rad)
  sketch-geometry (14):
    g0: Circle CenterX=-5.6 CenterY=7.6 CenterZ=0 NormalX=0 NormalY=0 NormalZ=1 AngleXU=0 Radius=1.6
    g1: Circle CenterX=-5.6 CenterY=7.6 CenterZ=0 NormalX=0 NormalY=0 NormalZ=1 AngleXU=0 Radius=4
    g2: Circle CenterX=-5.6 CenterY=34.8 CenterZ=0 NormalX=0 NormalY=0 NormalZ=1 AngleXU=0 Radius=1.6
    g3: Circle CenterX=-5.6 CenterY=34.8 CenterZ=0 NormalX=0 NormalY=0 NormalZ=1 AngleXU=0 Radius=4
    g4: Circle CenterX=-184.08 CenterY=34.8 CenterZ=0 NormalX=0 NormalY=0 NormalZ=1 AngleXU=0 Radius=1.6
    g5: Circle CenterX=-184.08 CenterY=34.8 CenterZ=0 NormalX=0 NormalY=0 NormalZ=1 AngleXU=0 Radius=4
    g6: Circle CenterX=-179.305 CenterY=-76.8316 CenterZ=0 NormalX=0 NormalY=0 NormalZ=1 AngleXU=0 Radius=1.6
    g7: Circle CenterX=-179.305 CenterY=-76.8316 CenterZ=0 NormalX=0 NormalY=0 NormalZ=1 AngleXU=0 Radius=4
    g8: Circle CenterX=-213.443 CenterY=-76.8316 CenterZ=0 NormalX=0 NormalY=0 NormalZ=1 AngleXU=0 Radius=1.6
    g9: Circle CenterX=-213.443 CenterY=-76.8316 CenterZ=0 NormalX=0 NormalY=0 NormalZ=1 AngleXU=0 Radius=4
    g10: Circle CenterX=-78.51 CenterY=7.6 CenterZ=0 NormalX=0 NormalY=0 NormalZ=1 AngleXU=0 Radius=1.6
    g11: Circle CenterX=-78.51 CenterY=7.6 CenterZ=0 NormalX=0 NormalY=0 NormalZ=1 AngleXU=0 Radius=4
    g12: Circle CenterX=-78.51 CenterY=34.8 CenterZ=0 NormalX=0 NormalY=0 NormalZ=1 AngleXU=0 Radius=1.6
    g13: Circle CenterX=-78.51 CenterY=34.8 CenterZ=0 NormalX=0 NormalY=0 NormalZ=1 AngleXU=0 Radius=4
  constraints (35):
    c: Diameter(g0) = 3.2
    c: Diameter(g1) = 8
    c: Coincident(g0,g1)
    c: Diameter(g2) = 3.2
    c: Diameter(g3) = 8
    c: Coincident(g3,g2)
    c: Tangent(g2,g-7)
    c: Diameter(g4) = 3.2
    c: Diameter(g5) = 8
    c: Coincident(g5,g4)
    c: Tangent(g4,g-7)
    c: Tangent(g4,g-8)
    c: Diameter(g6) = 3.2
    c: Diameter(g7) = 8
    c: Coincident(g7,g6)
    c: Tangent(g6,g-9)
    c: Tangent(g6,g-10)
    c: Diameter(g8) = 3.2
    c: Diameter(g9) = 8
    c: Coincident(g9,g8)
    c: Tangent(g8,g-10)
    c: Tangent(g8,g-11)
    c: Diameter(g10) = 3.2
    c: Diameter(g11) = 8
    c: Diameter(g12) = 3.2
    c: Diameter(g13) = 8
    c: Coincident(g12,g13)
    c: Coincident(g10,g11)
    c: Tangent(g12,g-7)
    c: DistanceX(g12,g10) = 0
    c: Tangent(g2,g-6)
    c: Tangent(g0,g-6)
    c: Tangent(g0,g-3)
    c: Tangent(g10,g-3)
    c: Tangent(g10,g-4)
FEATURE [Part::Extrusion] Extrude012  label="extrude guide per coperture laterali"
  Base = -> Sketch016
  Dir = (0,-1,2e-16)
  DirMode = 2
  FaceMakerClass = Part::FaceMakerBullseye
  FaceMakerMode = 3
  LengthFwd = 25.2
  LengthRev = 0
  Solid = true
  Symmetric = true
FEATURE [Sketcher::SketchObject] Sketch017  label="supporto CAM"
  ArcFitTolerance = 1e-06
  AttachmentSupport = -> [XZ_Plane]
  ExternalGeometry = -> [Sketch]
  FullyConstrained = true
  MakeInternals = false
  MapMode = 5
  Placement = pos=(0,0,0) rot=(1,0,0;1.5708rad)
  sketch-geometry (6):
    g0: LineSegment StartX=-2.4 StartY=48 StartZ=0 EndX=-2.4 EndY=41.2 EndZ=0
    g1: LineSegment StartX=-2.4 StartY=48 StartZ=0 EndX=-34 EndY=48 EndZ=0
    g2: LineSegment StartX=-34 StartY=48 StartZ=0 EndX=-34 EndY=46.72 EndZ=0
    g3: LineSegment StartX=-34 StartY=46.72 StartZ=0 EndX=-36 EndY=46.72 EndZ=0
    g4: LineSegment StartX=-36 StartY=46.72 StartZ=0 EndX=-36 EndY=41.2 EndZ=0
    g5: LineSegment StartX=-36 StartY=41.2 StartZ=0 EndX=-2.4 EndY=41.2 EndZ=0
  constraints (15):
    c: Coincident(g1,g0)
    c: Horizontal(g1)
    c: Coincident(g2,g1)
    c: Vertical(g2)
    c: Coincident(g3,g2)
    c: Horizontal(g3)
    c: Coincident(g4,g3)
    c: Coincident(g5,g4)
    c: DistanceX(g1,g0) = 31.6
    c: Coincident(g5,g0)
    c: Vertical(g4)
    c: DistanceY(g2,g1) = 1.28
    c: Coincident(g0,g-3)
    c: Coincident(g0,g-3)
    c: Coincident(g4,g-4)
FEATURE [Part::Extrusion] Extrude013  label="Extrude supporto CAM"
  Base = -> Sketch017
  Dir = (0,-1,2e-16)
  DirMode = 2
  FaceMakerClass = Part::FaceMakerBullseye
  FaceMakerMode = 3
  LengthFwd = 17.8
  LengthRev = 0
  Solid = true
  Symmetric = true
FEATURE [Sketcher::SketchObject] Sketch018  label="Scavo CAM"
  ArcFitTolerance = 1e-06
  AttachmentSupport = -> [YZ_Plane]
  ExternalGeometry = -> [Sketch]
  FullyConstrained = true
  MakeInternals = false
  MapMode = 5
  Placement = pos=(0,0,0) rot=(0.57735,0.57735,0.57735;2.0944rad)
  sketch-geometry (4):
    g0: LineSegment StartX=-7.73 StartY=48 StartZ=0 EndX=7.73 EndY=48 EndZ=0
    g1: LineSegment [constr] StartX=1.07e-14 StartY=48 StartZ=0 EndX=0 EndY=43.5155 EndZ=0
    g2: ArcOfCircle CenterX=9e-15 CenterY=52.42 CenterZ=0 NormalX=0 NormalY=0 NormalZ=1 AngleXU=0 Radius=8.90445 StartAngle=3.66102 EndAngle=5.76376
    g3: Circle [constr] CenterX=9e-15 CenterY=52.42 CenterZ=0 NormalX=0 NormalY=0 NormalZ=1 AngleXU=0 Radius=8.9
  constraints (13):
    c: Horizontal(g0)
    c: DistanceY(g-3,g0) = 0
    c: DistanceX(g0,g0) = 15.46
    c: DistanceX(g0,g-3) = 7.73
    c: DistanceX(g-3) = 0
    c: Coincident(g1,g-3)
    c: PointOnObject(g1,g-2)
    c: Coincident(g2,g0)
    c: Coincident(g2,g0)
    c: PointOnObject(g1,g2)
    c: Diameter(g3) = 17.8
    c: DistanceY(g1,g3) = 4.42
    c: Coincident(g2,g3)
FEATURE [Part::Extrusion] Extrude014  label="Extrude Scavo CAM"
  Base = -> Sketch018
  Dir = (1,0,0)
  DirMode = 2
  FaceMakerClass = Part::FaceMakerBullseye
  FaceMakerMode = 3
  LengthFwd = -34
  LengthRev = 0
  Solid = true
  Symmetric = false
FEATURE [Sketcher::SketchObject] Sketch019  label="scavo rumble"
  ArcFitTolerance = 1e-06
  AttachmentSupport = -> [XZ_Plane]
  ExternalGeometry = -> [Sketch]
  FullyConstrained = true
  MakeInternals = false
  MapMode = 5
  Placement = pos=(0,0,0) rot=(1,0,0;1.5708rad)
  sketch-geometry (6):
    g0: LineSegment StartX=-163.771 StartY=-21.9058 StartZ=0 EndX=-158.636 EndY=-23.5745 EndZ=0
    g1: LineSegment StartX=-158.636 StartY=-23.5745 StartZ=0 EndX=-165.743 EndY=-45.4488 EndZ=0
    g2: LineSegment StartX=-165.743 StartY=-45.4488 StartZ=0 EndX=-170.879 EndY=-43.7801 EndZ=0
    g3: LineSegment StartX=-170.879 StartY=-43.7801 StartZ=0 EndX=-163.771 EndY=-21.9058 EndZ=0
    g4: LineSegment [constr] StartX=-145.51 StartY=22 StartZ=0 EndX=-160.157 EndY=-23.0801 EndZ=0
    g5: LineSegment [constr] StartX=-158.636 StartY=-23.5745 StartZ=0 EndX=-160.157 EndY=-23.0801 EndZ=0
  constraints (17):
    c: Coincident(g1,g0)
    c: Coincident(g2,g1)
    c: Coincident(g3,g2)
    c: Coincident(g3,g0)
    c: Parallel(g3,g-3)
    c: Parallel(g3,g1)
    c: Perpendicular(g3,g0)
    c: Perpendicular(g2,g3)
    c: Distance(g2,g0) = 23
    c: Parallel(g4,g-3)
    c: Distance(g4) = 47.4
    c: Coincident(g4,g-3)
    c: Parallel(g5,g0)
    c: Distance(g5) = 1.6
    c: Coincident(g5,g0)
    c: Distance(g5,g0) = 3.8
    c: Coincident(g5,g4)
FEATURE [Part::Extrusion] Extrude015  label="scavo rumble001"
  Base = -> Sketch019
  Dir = (0,-1,2e-16)
  DirMode = 2
  FaceMakerClass = Part::FaceMakerBullseye
  FaceMakerMode = 3
  LengthFwd = 21
  LengthRev = 0
  Solid = true
  Symmetric = true
FEATURE [Sketcher::SketchObject] Sketch020  label="fermo rumble"
  ArcFitTolerance = 1e-06
  AttachmentSupport = -> [XZ_Plane]
  ExternalGeometry = -> [Sketch019,Sketch]
  FullyConstrained = true
  MakeInternals = false
  MapMode = 5
  Placement = pos=(0,0,0) rot=(1,0,0;1.5708rad)
  sketch-geometry (16):
    g0: LineSegment [constr] StartX=-165.905 StartY=-40.7697 StartZ=0 EndX=-167.265 EndY=-44.9544 EndZ=0
    g1: LineSegment [constr] StartX=-167.265 StartY=-44.9544 StartZ=0 EndX=-165.743 EndY=-45.4488 EndZ=0
    g2: LineSegment StartX=-167.318 StartY=-37.9976 StartZ=0 EndX=-165.225 EndY=-38.6774 EndZ=0
    g3: LineSegment StartX=-165.225 StartY=-38.6774 StartZ=0 EndX=-165.905 EndY=-40.7697 EndZ=0
    g4: LineSegment StartX=-165.905 StartY=-40.7697 StartZ=0 EndX=-167.997 EndY=-40.0899 EndZ=0
    g5: LineSegment StartX=-167.997 StartY=-40.0899 StartZ=0 EndX=-167.318 EndY=-37.9976 EndZ=0
    g6: LineSegment StartX=-166.823 StartY=-36.4759 StartZ=0 EndX=-163.399 EndY=-37.5883 EndZ=0
    g7: LineSegment StartX=-163.399 StartY=-37.5883 StartZ=0 EndX=-165.006 EndY=-42.5338 EndZ=0
    g8: LineSegment StartX=-165.006 StartY=-42.5338 StartZ=0 EndX=-168.43 EndY=-41.4214 EndZ=0
    g9: LineSegment StartX=-169.457 StartY=-39.4053 StartZ=0 EndX=-168.839 EndY=-37.5031 EndZ=0
    g10: LineSegment [constr] StartX=-168.839 StartY=-37.5031 StartZ=0 EndX=-168.345 EndY=-35.9815 EndZ=0
    g11: LineSegment [constr] StartX=-168.345 StartY=-35.9815 StartZ=0 EndX=-166.823 EndY=-36.4759 EndZ=0
    g12: ArcOfCircle CenterX=-167.936 CenterY=-39.8997 CenterZ=0 NormalX=0 NormalY=0 NormalZ=1 AngleXU=0 Radius=1.6 StartAngle=2.82743 EndAngle=4.39823
    g13: GeomPoint [constr] X=-169.952 Y=-40.9269 Z=0
    g14: ArcOfCircle CenterX=-167.318 CenterY=-37.9976 CenterZ=0 NormalX=0 NormalY=0 NormalZ=1 AngleXU=0 Radius=1.6 StartAngle=1.25664 EndAngle=2.82743
    g15: GeomPoint [constr] X=-168.345 Y=-35.9815 Z=0
  constraints (42):
    c: Parallel(g0,g-4)
    c: Distance(g0) = 4.4
    c: Coincident(g1,g0)
    c: Perpendicular(g0,g1)
    c: Distance(g1) = 1.6
    c: Coincident(g1,g-5)
    c: Coincident(g3,g2)
    c: Coincident(g4,g3)
    c: Coincident(g5,g4)
    c: Coincident(g5,g2)
    c: Parallel(g3,g-4)
    c: Parallel(g3,g5)
    c: Perpendicular(g2,g3)
    c: Parallel(g4,g2)
    c: Distance(g2) = 2.2
    c: Distance(g3) = 2.2
    c: Coincident(g7,g6)
    c: Coincident(g8,g7)
    c: Parallel(g7,g-4)
    c: Parallel(g7,g9)
    c: Perpendicular(g6,g7)
    c: Parallel(g6,g8)
    c: Distance(g6,g15) = 5.2
    c: Distance(g7) = 5.2
    c: Coincident(g11,g10)
    c: Parallel(g10,g9)
    c: Parallel(g11,g6)
    c: Distance(g10) = 1.6
    c: Distance(g11) = 1.6
    c: Coincident(g10,g15)
    c: Distance(g11,g2) = 1.6
    c: Distance(g2,g10) = 1.6
    c: PointOnObject(g13,g8)
    c: PointOnObject(g13,g9)
    c: Tangent(g8,g12) = 1.5708
    c: Tangent(g9,g12) = 1.5708
    c: PointOnObject(g15,g9)
    c: Tangent(g6,g14) = 1.5708
    c: Tangent(g9,g14) = 1.5708
    c: Equal(g12,g14)
    c: Coincident(g6,g11)
    c: Coincident(g3,g0)
FEATURE [Part::Extrusion] Extrude016  label="Extrude fermo rumble"
  Base = -> Sketch020
  Dir = (0,-1,2e-16)
  DirMode = 2
  FaceMakerClass = Part::FaceMakerBullseye
  FaceMakerMode = 3
  LengthFwd = 25.2
  LengthRev = 0
  Solid = true
  Symmetric = true
FEATURE [Sketcher::SketchObject] Sketch021  label="perno fermo rumble001"
  ArcFitTolerance = 1e-06
  AttachmentSupport = -> [XZ_Plane001]
  FullyConstrained = true
  MakeInternals = false
  MapMode = 5
  Placement = pos=(0,0,0) rot=(1,0,0;1.5708rad)
  sketch-geometry (16):
    g0: LineSegment StartX=0 StartY=0.45 StartZ=0 EndX=0 EndY=1.55 EndZ=0
    g1: LineSegment StartX=0.45 StartY=2 StartZ=0 EndX=1.55 EndY=2 EndZ=0
    g2: LineSegment StartX=2 StartY=1.55 StartZ=0 EndX=2 EndY=0.45 EndZ=0
    g3: LineSegment StartX=1.55 StartY=0 StartZ=0 EndX=0.45 EndY=0 EndZ=0
    g4: ArcOfCircle [constr] CenterX=0.45 CenterY=1.55 CenterZ=0 NormalX=0 NormalY=0 NormalZ=1 AngleXU=0 Radius=0.45 StartAngle=1.5708 EndAngle=3.14159
    g5: GeomPoint [constr] X=0 Y=2 Z=0
    g6: LineSegment StartX=0.45 StartY=2 StartZ=0 EndX=0 EndY=1.55 EndZ=0
    g7: ArcOfCircle [constr] CenterX=1.55 CenterY=1.55 CenterZ=0 NormalX=0 NormalY=0 NormalZ=1 AngleXU=0 Radius=0.45 StartAngle=0 EndAngle=1.5708
    g8: GeomPoint [constr] X=2 Y=2 Z=0
    g9: LineSegment StartX=2 StartY=1.55 StartZ=0 EndX=1.55 EndY=2 EndZ=0
    g10: ArcOfCircle [constr] CenterX=1.55 CenterY=0.45 CenterZ=0 NormalX=0 NormalY=0 NormalZ=1 AngleXU=0 Radius=0.45 StartAngle=4.71239 EndAngle=6.28319
    g11: GeomPoint [constr] X=2 Y=0 Z=0
    g12: LineSegment StartX=1.55 StartY=0 StartZ=0 EndX=2 EndY=0.45 EndZ=0
    g13: ArcOfCircle [constr] CenterX=0.45 CenterY=0.45 CenterZ=0 NormalX=0 NormalY=0 NormalZ=1 AngleXU=0 Radius=0.45 StartAngle=3.14159 EndAngle=4.71239
    g14: GeomPoint [constr] X=0 Y=0 Z=0
    g15: LineSegment StartX=0 StartY=0.45 StartZ=0 EndX=0.45 EndY=0 EndZ=0
  constraints (35):
    c: Coincident(g14,g-1)
    c: PointOnObject(g5,g-2)
    c: Horizontal(g1)
    c: Vertical(g2)
    c: Horizontal(g3)
    c: DistanceX(g5,g8) = 2
    c: DistanceY(g11,g8) = 2
    c: PointOnObject(g5,g0)
    c: PointOnObject(g5,g1)
    c: Tangent(g0,g4) = 1.5708
    c: Tangent(g1,g4) = 1.5708
    c: Coincident(g6,g0)
    c: Coincident(g6,g1)
    c: PointOnObject(g8,g2)
    c: PointOnObject(g8,g1)
    c: Tangent(g2,g7) = 1.5708
    c: Tangent(g1,g7) = 1.5708
    c: Coincident(g9,g2)
    c: Coincident(g9,g1)
    c: PointOnObject(g11,g2)
    c: PointOnObject(g11,g3)
    c: Tangent(g2,g10) = 1.5708
    c: Tangent(g3,g10) = 1.5708
    c: Coincident(g12,g2)
    c: Coincident(g12,g3)
    c: PointOnObject(g14,g0)
    c: PointOnObject(g14,g3)
    c: Tangent(g0,g13) = 1.5708
    c: Tangent(g3,g13) = 1.5708
    c: Coincident(g15,g0)
    c: Coincident(g15,g3)
    c: Equal(g6,g9)
    c: Equal(g9,g12)
    c: Equal(g12,g15)
    c: DistanceX(g14,g3) = 0.45
FEATURE [Sketcher::SketchObject] Sketch022  label="fori per M3x5(OD)x6(L)"
  ArcFitTolerance = 1e-06
  AttachmentSupport = -> [XZ_Plane]
  ExternalGeometry = -> [Sketch016]
  FullyConstrained = true
  MakeInternals = false
  MapMode = 5
  Placement = pos=(0,0,0) rot=(1,0,0;1.5708rad)
  sketch-geometry (7):
    g0: Circle CenterX=-5.6 CenterY=34.8 CenterZ=0 NormalX=0 NormalY=0 NormalZ=1 AngleXU=0 Radius=2.5
    g1: Circle CenterX=-5.6 CenterY=7.6 CenterZ=0 NormalX=0 NormalY=0 NormalZ=1 AngleXU=0 Radius=2.5
    g2: Circle CenterX=-78.51 CenterY=34.8 CenterZ=0 NormalX=0 NormalY=0 NormalZ=1 AngleXU=0 Radius=2.5
    g3: Circle CenterX=-78.51 CenterY=7.6 CenterZ=0 NormalX=0 NormalY=0 NormalZ=1 AngleXU=0 Radius=2.5
    g4: Circle CenterX=-184.08 CenterY=34.8 CenterZ=0 NormalX=0 NormalY=0 NormalZ=1 AngleXU=0 Radius=2.5
    g5: Circle CenterX=-179.305 CenterY=-76.8316 CenterZ=0 NormalX=0 NormalY=0 NormalZ=1 AngleXU=0 Radius=2.5
    g6: Circle CenterX=-213.443 CenterY=-76.8316 CenterZ=0 NormalX=0 NormalY=0 NormalZ=1 AngleXU=0 Radius=2.5
  constraints (14):
    c: Diameter(g0) = 5
    c: Diameter(g1) = 5
    c: Diameter(g2) = 5
    c: Diameter(g3) = 5
    c: Diameter(g4) = 5
    c: Diameter(g5) = 5
    c: Diameter(g6) = 5
    c: Coincident(g0,g-8)
    c: Coincident(g1,g-9)
    c: Coincident(g2,g-6)
    c: Coincident(g3,g-7)
    c: Coincident(g4,g-5)
    c: Coincident(g5,g-4)
    c: Coincident(g6,g-3)
FEATURE [Part::Extrusion] Extrude018  label="Extrude fori M3x5x6 - dx"
  Base = -> Sketch022
  Dir = (0,-1,2e-16)
  DirMode = 2
  FaceMakerClass = Part::FaceMakerBullseye
  FaceMakerMode = 3
  LengthFwd = 6.2
  LengthRev = 0
  Placement = pos=(0,-9.5,0) rot=(0,0,1;0rad)
  Solid = true
  Symmetric = true
FEATURE [Part::Extrusion] Extrude019  label="Extrude fori M3x5x6 - sx"
  Base = -> Sketch022
  Dir = (0,-1,2e-16)
  DirMode = 2
  FaceMakerClass = Part::FaceMakerBullseye
  FaceMakerMode = 3
  LengthFwd = 6.2
  LengthRev = 0
  Placement = pos=(0,9.5,0) rot=(0,0,1;0rad)
  Solid = true
  Symmetric = true
FEATURE [Sketcher::SketchObject] Sketch023  label="foro anteriore M3x5x6"
  ArcFitTolerance = 1e-06
  AttachmentSupport = -> [YZ_Plane]
  FullyConstrained = true
  MakeInternals = false
  MapMode = 5
  Placement = pos=(0,0,0) rot=(0.57735,0.57735,0.57735;2.0944rad)
  sketch-geometry (2):
    g0: LineSegment [constr] StartX=0 StartY=0 StartZ=0 EndX=0 EndY=38.6 EndZ=0
    g1: Circle CenterX=0 CenterY=38.6 CenterZ=0 NormalX=0 NormalY=0 NormalZ=1 AngleXU=0 Radius=2.5
  constraints (5):
    c: Coincident(g0,g-1)
    c: PointOnObject(g0,g-2)
    c: DistanceY(g0,g0) = 38.6
    c: Diameter(g1) = 5
    c: Coincident(g1,g0)
FEATURE [Part::Extrusion] Extrude020  label="Extrude foro anteriore M3x5x6"
  Base = -> Sketch023
  Dir = (1,0,0)
  DirMode = 2
  FaceMakerClass = Part::FaceMakerBullseye
  FaceMakerMode = 3
  LengthFwd = -6.2
  LengthRev = 0
  Solid = true
  Symmetric = false
FEATURE [Sketcher::SketchObject] Sketch024  label="fori per viti frontale"
  ArcFitTolerance = 1e-06
  AttachmentSupport = -> [YZ_Plane]
  FullyConstrained = true
  MakeInternals = false
  MapMode = 5
  Placement = pos=(0,0,0) rot=(0.57735,0.57735,0.57735;2.0944rad)
  sketch-geometry (9):
    g0: LineSegment [constr] StartX=-10.3 StartY=30.721 StartZ=0 EndX=10.3 EndY=30.721 EndZ=0
    g1: LineSegment [constr] StartX=10.3 StartY=30.721 StartZ=0 EndX=10.3 EndY=10.121 EndZ=0
    g2: LineSegment [constr] StartX=10.3 StartY=10.121 StartZ=0 EndX=-10.3 EndY=10.121 EndZ=0
    g3: LineSegment [constr] StartX=-10.3 StartY=10.121 StartZ=0 EndX=-10.3 EndY=30.721 EndZ=0
    g4: LineSegment [constr] StartX=0 StartY=0 StartZ=0 EndX=0 EndY=10.121 EndZ=0
    g5: Circle CenterX=-10.3 CenterY=30.721 CenterZ=0 NormalX=0 NormalY=0 NormalZ=1 AngleXU=0 Radius=2
    g6: Circle CenterX=10.3 CenterY=30.721 CenterZ=0 NormalX=0 NormalY=0 NormalZ=1 AngleXU=0 Radius=2
    g7: Circle CenterX=-10.3 CenterY=10.121 CenterZ=0 NormalX=0 NormalY=0 NormalZ=1 AngleXU=0 Radius=2
    g8: Circle CenterX=10.3 CenterY=10.121 CenterZ=0 NormalX=0 NormalY=0 NormalZ=1 AngleXU=0 Radius=2
  constraints (22):
    c: Horizontal(g0)
    c: Coincident(g1,g0)
    c: Vertical(g1)
    c: Coincident(g2,g1)
    c: Horizontal(g2)
    c: Coincident(g3,g2)
    c: Coincident(g3,g0)
    c: Vertical(g3)
    c: DistanceX(g0,g0) = 20.6
    c: DistanceY(g3,g3) = 20.6
    c: Coincident(g4,g-1)
    c: PointOnObject(g4,g-2)
    c: DistanceY(g4,g4) = 10.121
    c: Symmetric(g2,g2,g4)
    c: Diameter(g5) = 4
    c: Diameter(g6) = 4
    c: Diameter(g7) = 4
    c: Diameter(g8) = 4
    c: Coincident(g5,g0)
    c: Coincident(g6,g0)
    c: Coincident(g7,g2)
    c: Coincident(g8,g1)
FEATURE [Part::Extrusion] Extrude021  label="Extrude fori per viti frontale"
  Base = -> Sketch024
  Dir = (1,0,0)
  DirMode = 2
  FaceMakerClass = Part::FaceMakerBullseye
  FaceMakerMode = 3
  LengthFwd = -2.4
  LengthRev = 0
  Solid = true
  Symmetric = false
FEATURE [Sketcher::SketchObject] Sketch025  label="foro per filo CAM"
  ArcFitTolerance = 1e-06
  AttachmentSupport = -> [XZ_Plane]
  ExternalGeometry = -> [Sketch]
  FullyConstrained = true
  MakeInternals = false
  MapMode = 5
  Placement = pos=(0,0,0) rot=(1,0,0;1.5708rad)
  sketch-geometry (4):
    g0: LineSegment StartX=-44.6 StartY=41.2 StartZ=0 EndX=-44.6 EndY=36.4 EndZ=0
    g1: LineSegment StartX=-44.6 StartY=36.4 StartZ=0 EndX=-54.6 EndY=36.4 EndZ=0
    g2: LineSegment StartX=-54.6 StartY=36.4 StartZ=0 EndX=-50.4 EndY=41.2 EndZ=0
    g3: LineSegment StartX=-50.4 StartY=41.2 StartZ=0 EndX=-44.6 EndY=41.2 EndZ=0
  constraints (11):
    c: Vertical(g0)
    c: Coincident(g1,g0)
    c: Horizontal(g1)
    c: Coincident(g2,g1)
    c: Coincident(g3,g2)
    c: Coincident(g3,g0)
    c: Horizontal(g3)
    c: Coincident(g0,g-3)
    c: DistanceY(g0,g-4) = 0
    c: DistanceX(g3,g3) = 5.8
    c: DistanceX(g1,g1) = 10
FEATURE [Part::Extrusion] Extrude022  label="Extrude foro per filo CAM dx"
  Base = -> Sketch025
  Dir = (0,-1,2e-16)
  DirMode = 2
  FaceMakerClass = Part::FaceMakerBullseye
  FaceMakerMode = 3
  LengthFwd = 4.9
  LengthRev = 0
  Placement = pos=(0,6.95,0) rot=(0,0,1;0rad)
  Solid = true
  Symmetric = true
FEATURE [Part::Extrusion] Extrude023  label="Extrude foro per filo CAM sx"
  Base = -> Sketch025
  Dir = (0,-1,2e-16)
  DirMode = 2
  FaceMakerClass = Part::FaceMakerBullseye
  FaceMakerMode = 3
  LengthFwd = 4.9
  LengthRev = 0
  Placement = pos=(0,-6.95,0) rot=(0,0,1;0rad)
  Solid = true
  Symmetric = true
FEATURE [Sketcher::SketchObject] Sketch026  label="foro sotto anteriore M3x5x6"
  ArcFitTolerance = 1e-06
  AttachmentSupport = -> [XY_Plane]
  FullyConstrained = true
  MakeInternals = false
  MapMode = 5
  sketch-geometry (2):
    g0: LineSegment [constr] StartX=0 StartY=0 StartZ=0 EndX=-16.5 EndY=0 EndZ=0
    g1: Circle CenterX=-16.5 CenterY=0 CenterZ=0 NormalX=0 NormalY=0 NormalZ=1 AngleXU=0 Radius=2.5
  constraints (5):
    c: Distance(g0) = 16.5
    c: Coincident(g0,g-1)
    c: PointOnObject(g0,g-1)
    c: Diameter(g1) = 5
    c: Coincident(g0,g1)
FEATURE [Sketcher::SketchObject] Sketch027  label="foro sotto posteriore M3x5x6"
  ArcFitTolerance = 1e-06
  AttachmentSupport = -> [XY_Plane]
  ExternalGeometry = -> [Sketch]
  FullyConstrained = true
  MakeInternals = false
  MapMode = 5
  sketch-geometry (2):
    g0: LineSegment [constr] StartX=-82.8 StartY=2e-16 StartZ=0 EndX=-71.3 EndY=2e-16 EndZ=0
    g1: Circle CenterX=-71.3 CenterY=2e-16 CenterZ=0 NormalX=0 NormalY=0 NormalZ=1 AngleXU=0 Radius=2.5
  constraints (5):
    c: Distance(g0) = 11.5
    c: Coincident(g0,g-3)
    c: PointOnObject(g0,g-3)
    c: Diameter(g1) = 5
    c: Coincident(g1,g0)
FEATURE [Sketcher::SketchObject] Sketch029  label="fori sotto impugnatura"
  ArcFitTolerance = 1e-06
  AttachmentSupport = -> [XY_Plane]
  ExternalGeometry = -> [Sketch]
  FullyConstrained = true
  MakeInternals = false
  MapMode = 5
  sketch-geometry (15):
    g0: LineSegment [constr] StartX=-175.232 StartY=-1.83e-14 StartZ=0 EndX=-191.232 EndY=0 EndZ=0
    g1: Circle CenterX=-191.232 CenterY=0 CenterZ=0 NormalX=0 NormalY=0 NormalZ=1 AngleXU=0 Radius=3.95
    g2: LineSegment [constr] StartX=-175.232 StartY=-1.83e-14 StartZ=0 EndX=-204.275 EndY=0 EndZ=0
    g3: LineSegment StartX=-204.275 StartY=3.525 StartZ=0 EndX=-204.275 EndY=-3.525 EndZ=0
    g4: LineSegment StartX=-205.4 StartY=-4.65 StartZ=0 EndX=-206.65 EndY=-4.65 EndZ=0
    g5: LineSegment StartX=-207.775 StartY=-3.525 StartZ=0 EndX=-207.775 EndY=3.525 EndZ=0
    g6: LineSegment StartX=-206.65 StartY=4.65 StartZ=0 EndX=-205.4 EndY=4.65 EndZ=0
    g7: ArcOfCircle CenterX=-206.65 CenterY=3.525 CenterZ=0 NormalX=0 NormalY=0 NormalZ=1 AngleXU=0 Radius=1.125 StartAngle=1.5708 EndAngle=3.14159
    g8: GeomPoint [constr] X=-207.775 Y=4.65 Z=0
    g9: ArcOfCircle CenterX=-205.4 CenterY=3.525 CenterZ=0 NormalX=0 NormalY=0 NormalZ=1 AngleXU=0 Radius=1.125 StartAngle=0 EndAngle=1.5708
    g10: GeomPoint [constr] X=-204.275 Y=4.65 Z=0
    g11: ArcOfCircle CenterX=-205.4 CenterY=-3.525 CenterZ=0 NormalX=0 NormalY=0 NormalZ=1 AngleXU=0 Radius=1.125 StartAngle=4.71239 EndAngle=6.28319
    g12: GeomPoint [constr] X=-204.275 Y=-4.65 Z=0
    g13: ArcOfCircle CenterX=-206.65 CenterY=-3.525 CenterZ=0 NormalX=0 NormalY=0 NormalZ=1 AngleXU=0 Radius=1.125 StartAngle=3.14159 EndAngle=4.71239
    g14: GeomPoint [constr] X=-207.775 Y=-4.65 Z=0
  constraints (35):
    c: Distance(g0) = 16
    c: Coincident(g0,g-3)
    c: PointOnObject(g0,g-1)
    c: Diameter(g1) = 7.9
    c: Coincident(g1,g0)
    c: Coincident(g2,g0)
    c: PointOnObject(g2,g-1)
    c: Vertical(g3)
    c: Horizontal(g4)
    c: Vertical(g5)
    c: Horizontal(g6)
    c: DistanceY(g12,g10) = 9.3
    c: DistanceX(g8,g10) = 3.5
    c: Symmetric(g10,g12,g2)
    c: PointOnObject(g8,g5)
    c: PointOnObject(g8,g6)
    c: Tangent(g5,g7) = 1.5708
    c: Tangent(g6,g7) = 1.5708
    c: PointOnObject(g10,g3)
    c: PointOnObject(g10,g6)
    c: Tangent(g3,g9) = 1.5708
    c: Tangent(g6,g9) = 1.5708
    c: PointOnObject(g12,g3)
    c: PointOnObject(g12,g4)
    c: Tangent(g3,g11) = 1.5708
    c: Tangent(g4,g11) = 1.5708
    c: PointOnObject(g14,g4)
    c: PointOnObject(g14,g5)
    c: Tangent(g4,g13) = 1.5708
    c: Tangent(g5,g13) = 1.5708
    c: Equal(g7,g9)
    c: Equal(g9,g11)
    c: Equal(g11,g13)
    c: DistanceX(g6,g6) = 1.25
    c: DistanceX(g-5,g5) = 6.8
FEATURE [Sketcher::SketchObject] Sketch030  label="fori superiori per solenoide e oled"
  ArcFitTolerance = 1e-06
  AttachmentSupport = -> [XY_Plane]
  ExternalGeometry = -> [Sketch]
  FullyConstrained = true
  MakeInternals = false
  MapMode = 5
  sketch-geometry (33):
    g0: LineSegment [constr] StartX=-181.6 StartY=1.12e-14 StartZ=0 EndX=-169.91 EndY=0 EndZ=0
    g1: LineSegment [constr] StartX=-169.91 StartY=0 StartZ=0 EndX=-169.91 EndY=-2.6 EndZ=0
    g2: LineSegment [constr] StartX=-169.91 StartY=0 StartZ=0 EndX=-169.91 EndY=2.6 EndZ=0
    g3: LineSegment StartX=-169.91 StartY=4.975 StartZ=0 EndX=-169.91 EndY=8.225 EndZ=0
    g4: LineSegment StartX=-167.535 StartY=10.6 StartZ=0 EndX=-167.285 EndY=10.6 EndZ=0
    g5: LineSegment StartX=-164.91 StartY=8.225 StartZ=0 EndX=-164.91 EndY=4.975 EndZ=0
    g6: LineSegment StartX=-167.285 StartY=2.6 StartZ=0 EndX=-167.535 EndY=2.6 EndZ=0
    g7: LineSegment StartX=-169.91 StartY=-4.975 StartZ=0 EndX=-169.91 EndY=-8.225 EndZ=0
    g8: LineSegment StartX=-167.535 StartY=-10.6 StartZ=0 EndX=-167.285 EndY=-10.6 EndZ=0
    g9: LineSegment StartX=-164.91 StartY=-8.225 StartZ=0 EndX=-164.91 EndY=-4.975 EndZ=0
    g10: LineSegment StartX=-167.285 StartY=-2.6 StartZ=0 EndX=-167.535 EndY=-2.6 EndZ=0
    g11: ArcOfCircle CenterX=-167.535 CenterY=8.225 CenterZ=0 NormalX=0 NormalY=0 NormalZ=1 AngleXU=0 Radius=2.375 StartAngle=1.5708 EndAngle=3.14159
    g12: GeomPoint [constr] X=-169.91 Y=10.6 Z=0
    g13: ArcOfCircle CenterX=-167.285 CenterY=8.225 CenterZ=0 NormalX=0 NormalY=0 NormalZ=1 AngleXU=0 Radius=2.375 StartAngle=0 EndAngle=1.5708
    g14: GeomPoint [constr] X=-164.91 Y=10.6 Z=0
    g15: ArcOfCircle CenterX=-167.285 CenterY=4.975 CenterZ=0 NormalX=0 NormalY=0 NormalZ=1 AngleXU=0 Radius=2.375 StartAngle=4.71239 EndAngle=6.28319
    g16: GeomPoint [constr] X=-164.91 Y=2.6 Z=0
    g17: ArcOfCircle CenterX=-167.535 CenterY=4.975 CenterZ=0 NormalX=0 NormalY=0 NormalZ=1 AngleXU=0 Radius=2.375 StartAngle=3.14159 EndAngle=4.71239
    g18: GeomPoint [constr] X=-169.91 Y=2.6 Z=0
    g19: ArcOfCircle CenterX=-167.535 CenterY=-4.975 CenterZ=0 NormalX=0 NormalY=0 NormalZ=1 AngleXU=0 Radius=2.375 StartAngle=1.5708 EndAngle=3.14159
    g20: GeomPoint [constr] X=-169.91 Y=-2.6 Z=0
    g21: ArcOfCircle CenterX=-167.285 CenterY=-4.975 CenterZ=0 NormalX=0 NormalY=0 NormalZ=1 AngleXU=0 Radius=2.375 StartAngle=0 EndAngle=1.5708
    g22: GeomPoint [constr] X=-164.91 Y=-2.6 Z=0
    g23: ArcOfCircle CenterX=-167.285 CenterY=-8.225 CenterZ=0 NormalX=0 NormalY=0 NormalZ=1 AngleXU=0 Radius=2.375 StartAngle=4.71239 EndAngle=6.28319
    g24: GeomPoint [constr] X=-164.91 Y=-10.6 Z=0
    g25: ArcOfCircle CenterX=-167.535 CenterY=-8.225 CenterZ=0 NormalX=0 NormalY=0 NormalZ=1 AngleXU=0 Radius=2.375 StartAngle=3.14159 EndAngle=4.71239
    g26: GeomPoint [constr] X=-169.91 Y=-10.6 Z=0
    g27: LineSegment [constr] StartX=-181.6 StartY=1.12e-14 StartZ=0 EndX=-152.209 EndY=0 EndZ=0
    g28: LineSegment [constr] StartX=-181.6 StartY=1.12e-14 StartZ=0 EndX=-130.41 EndY=0 EndZ=0
    g29: LineSegment [constr] StartX=-152.209 StartY=0 StartZ=0 EndX=-152.209 EndY=6.95 EndZ=0
    g30: LineSegment [constr] StartX=-130.41 StartY=0 StartZ=0 EndX=-130.41 EndY=-6.95 EndZ=0
    g31: Circle CenterX=-152.209 CenterY=6.95 CenterZ=0 NormalX=0 NormalY=0 NormalZ=1 AngleXU=0 Radius=2.1
    g32: Circle CenterX=-130.41 CenterY=-6.95 CenterZ=0 NormalX=0 NormalY=0 NormalZ=1 AngleXU=0 Radius=2.1
  constraints (79):
    c: Distance(g0) = 11.69
    c: PointOnObject(g0,g-1)
    c: Coincident(g-4,g0)
    c: Distance(g1) = 2.6
    c: Coincident(g1,g0)
    c: Vertical(g1)
    c: Distance(g2) = 2.6
    c: Coincident(g2,g0)
    c: Vertical(g2)
    c: Distance(g18,g12) = 8
    c: Coincident(g18,g2)
    c: Vertical(g3)
    c: Distance(g14,g12) = 5
    c: Horizontal(g4)
    c: Distance(g16,g14) = 8
    c: Vertical(g5)
    c: Distance(g26,g20) = 8
    c: Coincident(g20,g1)
    c: Vertical(g7)
    c: Distance(g26,g24) = 5
    c: Horizontal(g8)
    c: Distance(g24,g22) = 8
    c: Vertical(g9)
    c: PointOnObject(g12,g3)
    c: PointOnObject(g12,g4)
    c: Tangent(g3,g11) = 1.5708
    c: Tangent(g4,g11) = 1.5708
    c: PointOnObject(g14,g5)
    c: PointOnObject(g14,g4)
    c: Tangent(g5,g13) = 1.5708
    c: Tangent(g4,g13) = 1.5708
    c: PointOnObject(g16,g5)
    c: PointOnObject(g16,g6)
    c: Tangent(g5,g15) = 1.5708
    c: Tangent(g6,g15) = 1.5708
    c: PointOnObject(g18,g3)
    c: PointOnObject(g18,g6)
    c: Tangent(g3,g17) = 1.5708
    c: Tangent(g6,g17) = 1.5708
    c: Equal(g11,g13)
    c: Equal(g13,g15)
    c: Equal(g15,g17)
    c: DistanceX(g4,g4) = 0.25
    c: PointOnObject(g20,g7)
    c: PointOnObject(g20,g10)
    c: Tangent(g7,g19) = -1.5708
    c: Tangent(g10,g19) = -1.5708
    c: PointOnObject(g22,g9)
    c: PointOnObject(g22,g10)
    c: Tangent(g9,g21) = -1.5708
    c: Tangent(g10,g21) = -1.5708
    c: PointOnObject(g24,g9)
    c: PointOnObject(g24,g8)
    c: Tangent(g9,g23) = -1.5708
    c: Tangent(g8,g23) = -1.5708
    c: PointOnObject(g26,g8)
    c: PointOnObject(g26,g7)
    c: Tangent(g8,g25) = -1.5708
    c: Tangent(g7,g25) = -1.5708
    c: Equal(g19,g21)
    c: Equal(g21,g23)
    c: Equal(g23,g25)
    c: DistanceX(g10,g10) = 0.25
    c: Distance(g27) = 29.391
    c: Coincident(g27,g0)
    c: PointOnObject(g27,g-1)
    c: Distance(g28) = 51.19
    c: Coincident(g28,g0)
    c: PointOnObject(g28,g-1)
    c: Distance(g29) = 6.95
    c: Coincident(g29,g27)
    c: Vertical(g29)
    c: Distance(g30) = 6.95
    c: Coincident(g30,g28)
    c: Vertical(g30)
    c: Diameter(g31) = 4.2
    c: Diameter(g32) = 4.2
    c: Coincident(g32,g30)
    c: Coincident(g31,g29)
FEATURE [Sketcher::SketchObject] Sketch031  label="fori inferiori switch pompa"
  ArcFitTolerance = 1e-06
  AttachmentSupport = -> [XY_Plane]
  ExternalGeometry = -> [Sketch]
  FullyConstrained = true
  MakeInternals = false
  MapMode = 5
  sketch-geometry (4):
    g0: LineSegment [constr] StartX=-57.2 StartY=1.9e-15 StartZ=0 EndX=-62.45 EndY=1.9e-15 EndZ=0
    g1: LineSegment [constr] StartX=-62.45 StartY=3.25 StartZ=0 EndX=-62.45 EndY=-3.25 EndZ=0
    g2: Circle CenterX=-62.45 CenterY=3.25 CenterZ=0 NormalX=0 NormalY=0 NormalZ=1 AngleXU=0 Radius=1.6
    g3: Circle CenterX=-62.45 CenterY=-3.25 CenterZ=0 NormalX=0 NormalY=0 NormalZ=1 AngleXU=0 Radius=1.6
  constraints (10):
    c: Distance(g0) = 5.25
    c: Coincident(g0,g-3)
    c: PointOnObject(g0,g-3)
    c: Vertical(g1)
    c: DistanceY(g1,g1) = 6.5
    c: Symmetric(g1,g1,g0)
    c: Diameter(g2) = 3.2
    c: Diameter(g3) = 3.2
    c: Coincident(g2,g1)
    c: Coincident(g3,g1)
FEATURE [Sketcher::SketchObject] Sketch032  label="spazio per PILA 18650"
  ArcFitTolerance = 1e-06
  AttachmentSupport = -> [XY_Plane]
  ExternalGeometry = -> [Sketch]
  FullyConstrained = true
  MakeInternals = false
  MapMode = 5
  sketch-geometry (2):
    g0: LineSegment [constr] StartX=-178.142 StartY=-1.74e-14 StartZ=0 EndX=-191.142 EndY=-1.83e-14 EndZ=0
    g1: Circle CenterX=-191.142 CenterY=-1.83e-14 CenterZ=0 NormalX=0 NormalY=0 NormalZ=1 AngleXU=0 Radius=10.5
  constraints (5):
    c: Distance(g0) = 13
    c: Coincident(g0,g-3)
    c: PointOnObject(g0,g-4)
    c: Diameter(g1) = 21
    c: Coincident(g1,g0)
FEATURE [Part::Extrusion] Extrude030  label="Extrude spazio per PILA 18650"
  Base = -> Sketch032
  Dir = (0,0,1)
  DirLink = -> Sketch [Edge45]
  DirMode = 2
  FaceMakerClass = Part::FaceMakerBullseye
  FaceMakerMode = 3
  LengthFwd = 76
  LengthRev = 0
  Placement = pos=(6,0,-72) rot=(0,0,1;0rad)
  Solid = true
  Symmetric = false
FEATURE [Sketcher::SketchObject] Sketch033  label="fermo per scheda micro"
  ArcFitTolerance = 1e-06
  AttachmentSupport = -> [XZ_Plane]
  ExternalGeometry = -> [Sketch]
  FullyConstrained = true
  MakeInternals = false
  MapMode = 5
  Placement = pos=(0,0,0) rot=(1,0,0;1.5708rad)
  sketch-geometry (12):
    g0: LineSegment StartX=-11.6 StartY=6 StartZ=0 EndX=-4 EndY=6 EndZ=0
    g1: LineSegment StartX=-4 StartY=6 StartZ=0 EndX=-4 EndY=36.4 EndZ=0
    g2: LineSegment StartX=-4 StartY=36.4 StartZ=0 EndX=-11.6 EndY=36.4 EndZ=0
    g3: LineSegment StartX=-11.6 StartY=36.4 StartZ=0 EndX=-11.6 EndY=6 EndZ=0
    g4: LineSegment StartX=-80.11 StartY=11.6 StartZ=0 EndX=-70.51 EndY=11.6 EndZ=0
    g5: LineSegment StartX=-70.51 StartY=11.6 StartZ=0 EndX=-70.51 EndY=6 EndZ=0
    g6: LineSegment StartX=-70.51 StartY=6 StartZ=0 EndX=-80.11 EndY=6 EndZ=0
    g7: LineSegment StartX=-80.11 StartY=6 StartZ=0 EndX=-80.11 EndY=11.6 EndZ=0
    g8: LineSegment StartX=-78.51 StartY=36.4 StartZ=0 EndX=-70.51 EndY=36.4 EndZ=0
    g9: LineSegment StartX=-70.51 StartY=36.4 StartZ=0 EndX=-70.51 EndY=30.8 EndZ=0
    g10: LineSegment StartX=-70.51 StartY=30.8 StartZ=0 EndX=-78.51 EndY=30.8 EndZ=0
    g11: LineSegment StartX=-78.51 StartY=30.8 StartZ=0 EndX=-78.51 EndY=36.4 EndZ=0
  constraints (33):
    c: Horizontal(g0)
    c: Coincident(g1,g0)
    c: Coincident(g2,g1)
    c: Horizontal(g2)
    c: Coincident(g3,g2)
    c: Coincident(g3,g0)
    c: Vertical(g3)
    c: DistanceX(g2,g2) = 7.6
    c: Coincident(g1,g-3)
    c: Coincident(g0,g-3)
    c: Horizontal(g4)
    c: Coincident(g5,g4)
    c: Vertical(g5)
    c: Coincident(g6,g5)
    c: Horizontal(g6)
    c: Coincident(g7,g6)
    c: Coincident(g7,g4)
    c: Vertical(g7)
    c: DistanceY(g5,g5) = 5.6
    c: DistanceX(g4,g4) = 9.6
    c: Coincident(g9,g8)
    c: Vertical(g9)
    c: Coincident(g10,g9)
    c: Horizontal(g10)
    c: Coincident(g11,g10)
    c: Coincident(g11,g8)
    c: Vertical(g11)
    c: DistanceY(g9,g9) = 5.6
    c: DistanceX(g10,g10) = 8
    c: Coincident(g4,g-4)
    c: DistanceX(g4,g10) = 1.6
    c: Horizontal(g8)
    c: DistanceY(g8,g1) = 0
FEATURE [Sketcher::SketchObject] Sketch034  label="buchi guida rail"
  ArcFitTolerance = 1e-06
  AttachmentSupport = -> [XY_Plane]
  ExternalGeometry = -> [Sketch]
  FullyConstrained = true
  MakeInternals = false
  MapMode = 5
  sketch-geometry (6):
    g0: LineSegment [constr] StartX=-100.8 StartY=9.1e-15 StartZ=0 EndX=-93.3 EndY=0 EndZ=0
    g1: LineSegment [constr] StartX=-93.3 StartY=0 StartZ=0 EndX=-73.3 EndY=0 EndZ=0
    g2: LineSegment [constr] StartX=-73.3 StartY=0 StartZ=0 EndX=-53.3 EndY=0 EndZ=0
    g3: Circle CenterX=-93.3 CenterY=0 CenterZ=0 NormalX=0 NormalY=0 NormalZ=1 AngleXU=0 Radius=2.5
    g4: Circle CenterX=-73.3 CenterY=0 CenterZ=0 NormalX=0 NormalY=0 NormalZ=1 AngleXU=0 Radius=2.5
    g5: Circle CenterX=-53.3 CenterY=0 CenterZ=0 NormalX=0 NormalY=0 NormalZ=1 AngleXU=0 Radius=2.5
  constraints (15):
    c: Distance(g0) = 7.5
    c: Coincident(g0,g-3)
    c: PointOnObject(g0,g-1)
    c: Distance(g1) = 20
    c: Coincident(g1,g0)
    c: PointOnObject(g1,g-1)
    c: Distance(g2) = 20
    c: Coincident(g2,g1)
    c: PointOnObject(g2,g-1)
    c: Diameter(g3) = 5
    c: Diameter(g4) = 5
    c: Diameter(g5) = 5
    c: Coincident(g3,g0)
    c: Coincident(g4,g1)
    c: Coincident(g5,g2)
FEATURE [Part::Extrusion] Extrude032  label="Extrude buchi guida rail"
  Base = -> Sketch034
  Dir = (0,0,1)
  DirMode = 2
  FaceMakerClass = Part::FaceMakerBullseye
  FaceMakerMode = 3
  LengthFwd = -6.2
  LengthRev = 0
  Placement = pos=(0,0,43.2) rot=(0,0,1;0rad)
  Solid = true
  Symmetric = false
FEATURE [Part::Extrusion] Extrude033  label="Extrude fori superiori per solenoide e oled001"
  Base = -> Sketch030
  Dir = (0,0,1)
  DirMode = 2
  FaceMakerClass = Part::FaceMakerBullseye
  FaceMakerMode = 3
  LengthFwd = -4.8
  LengthRev = 0
  Placement = pos=(0,0,41.2) rot=(0,0,1;0rad)
  Solid = true
  Symmetric = false
FEATURE [Part::Extrusion] Extrude034  label="Extrude fori sotto impugnatura001"
  Base = -> Sketch029
  Dir = (0,0,1)
  DirMode = 2
  FaceMakerClass = Part::FaceMakerBullseye
  FaceMakerMode = 3
  LengthFwd = 5
  LengthRev = 0
  Placement = pos=(0,0,-83) rot=(0,0,1;0rad)
  Solid = true
  Symmetric = false
FEATURE [Part::Extrusion] Extrude035  label="Extrude fori inferiori switch pompa001"
  Base = -> Sketch031
  Dir = (0,0,1)
  DirMode = 2
  FaceMakerClass = Part::FaceMakerBullseye
  FaceMakerMode = 3
  LengthFwd = 4
  LengthRev = 0
  Placement = pos=(0,0,-1.7) rot=(0,0,1;0rad)
  Solid = true
  Symmetric = false
FEATURE [Part::Extrusion] Extrude036  label="Extrude foro sotto posteriore M3x5x007"
  Base = -> Sketch027
  Dir = (0,0,1)
  DirMode = 2
  FaceMakerClass = Part::FaceMakerBullseye
  FaceMakerMode = 3
  LengthFwd = 6.2
  LengthRev = 0
  Placement = pos=(0,0,-9.6) rot=(0,0,1;0rad)
  Solid = true
  Symmetric = false
FEATURE [Part::Extrusion] Extrude037  label="Extrude foro sotto anteriore M3x5x007"
  Base = -> Sketch026
  Dir = (0,0,1)
  DirMode = 2
  FaceMakerClass = Part::FaceMakerBullseye
  FaceMakerMode = 3
  LengthFwd = 6.2
  LengthRev = 0
  Solid = true
  Symmetric = false
FEATURE [Sketcher::SketchObject] Sketch035  label="foro per fissaggio micro"
  ArcFitTolerance = 1e-06
  AttachmentSupport = -> [XZ_Plane]
  ExternalGeometry = -> [Sketch,Sketch033]
  FullyConstrained = true
  MakeInternals = false
  MapMode = 5
  Placement = pos=(0,0,0) rot=(1,0,0;1.5708rad)
  sketch-geometry (3):
    g0: Circle CenterX=-7.8 CenterY=21.2 CenterZ=0 NormalX=0 NormalY=0 NormalZ=1 AngleXU=0 Radius=1.6
    g1: GeomPoint [constr] X=-4 Y=21.2 Z=0
    g2: LineSegment [constr] StartX=-4 StartY=21.2 StartZ=0 EndX=-11.6 EndY=21.2 EndZ=0
  constraints (6):
    c: Diameter(g0) = 3.2
    c: Symmetric(g-3,g-3,g1)
    c: Coincident(g2,g1)
    c: Horizontal(g2)
    c: DistanceX(g-4,g2) = 0
    c: Symmetric(g2,g1,g0)
FEATURE [Part::Extrusion] Extrude038  label="Extrude foro per fissaggio micro"
  Base = -> Sketch035
  Dir = (0,-1,2e-16)
  DirMode = 2
  FaceMakerClass = Part::FaceMakerBullseye
  FaceMakerMode = 3
  LengthFwd = 3
  LengthRev = 0
  Placement = pos=(0,8.6,0) rot=(0,0,1;0rad)
  Solid = true
  Symmetric = false
FEATURE [Sketcher::SketchObject] Sketch036  label="supporto per alimentatore"
  ArcFitTolerance = 1e-06
  AttachmentSupport = -> [XZ_Plane]
  ExternalGeometry = -> [Sketch,Sketch016,Sketch022]
  FullyConstrained = true
  MakeInternals = false
  MapMode = 5
  Placement = pos=(0,0,0) rot=(1,0,0;1.5708rad)
  sketch-geometry (5):
    g0: LineSegment StartX=-211.843 StartY=-50.0944 StartZ=0 EndX=-211.843 EndY=-80.4316 EndZ=0
    g1: LineSegment StartX=-211.843 StartY=-50.0944 StartZ=0 EndX=-207.775 EndY=-41.3701 EndZ=0
    g2: LineSegment [constr] StartX=-209.443 StartY=-50.0944 StartZ=0 EndX=-209.443 EndY=-80.4316 EndZ=0
    g3: LineSegment StartX=-207.775 StartY=-41.3701 StartZ=0 EndX=-207.775 EndY=-80.4316 EndZ=0
    g4: LineSegment StartX=-211.843 StartY=-80.4316 StartZ=0 EndX=-207.775 EndY=-80.4316 EndZ=0
  constraints (15):
    c: Vertical(g0)
    c: Coincident(g1,g0)
    c: Vertical(g2)
    c: Tangent(g2,g-5)
    c: Coincident(g3,g1)
    c: Vertical(g3)
    c: DistanceY(g-3,g3) = -2
    c: Tangent(g1,g-8)
    c: DistanceY(g-3,g0) = -2
    c: Coincident(g4,g0)
    c: Coincident(g4,g3)
    c: Tangent(g0,g-6)
    c: DistanceY(g-3,g2) = -2
    c: DistanceY(g2,g0) = 0
    c: DistanceX(g-3,g3) = 6.8
FEATURE [Part::Extrusion] Extrude039  label="Extrude039 supporto alimentatore"
  Base = -> Sketch036
  Dir = (0,-1,2e-16)
  DirMode = 2
  FaceMakerClass = Part::FaceMakerBullseye
  FaceMakerMode = 3
  LengthFwd = 25.2
  LengthRev = 0
  Solid = true
  Symmetric = true
FEATURE [Sketcher::SketchObject] Sketch037  label="scavo per alimentatore"
  ArcFitTolerance = 1e-06
  AttachmentSupport = -> [XZ_Plane]
  ExternalGeometry = -> [Sketch036]
  FullyConstrained = true
  MakeInternals = false
  MapMode = 5
  Placement = pos=(0,0,0) rot=(1,0,0;1.5708rad)
  sketch-geometry (4):
    g0: LineSegment StartX=-209.575 StartY=-50.4316 StartZ=0 EndX=-209.575 EndY=-80.4316 EndZ=0
    g1: LineSegment StartX=-209.575 StartY=-50.4316 StartZ=0 EndX=-207.775 EndY=-50.4316 EndZ=0
    g2: LineSegment StartX=-207.775 StartY=-50.4316 StartZ=0 EndX=-207.775 EndY=-80.4316 EndZ=0
    g3: LineSegment StartX=-207.775 StartY=-80.4316 StartZ=0 EndX=-209.575 EndY=-80.4316 EndZ=0
  constraints (11):
    c: Vertical(g0)
    c: Coincident(g1,g0)
    c: Horizontal(g1)
    c: Coincident(g2,g1)
    c: Vertical(g2)
    c: Coincident(g3,g2)
    c: Coincident(g3,g0)
    c: Horizontal(g3)
    c: DistanceX(g1,g1) = 1.8
    c: Coincident(g2,g-3)
    c: DistanceY(g2,g2) = 30
FEATURE [Part::Extrusion] Extrude040  label="Extrude040 scavo alimentatore"
  Base = -> Sketch037
  Dir = (0,-1,2e-16)
  DirMode = 2
  FaceMakerClass = Part::FaceMakerBullseye
  FaceMakerMode = 3
  LengthFwd = 19.5
  LengthRev = 0
  Solid = true
  Symmetric = true
FEATURE [Part::Extrusion] Extrude031  label="Extrude fermo per scheda micro"
  Base = -> Sketch033
  Dir = (0,-1,2e-16)
  DirMode = 2
  FaceMakerClass = Part::FaceMakerBullseye
  FaceMakerMode = 3
  LengthFwd = 3
  LengthRev = 0
  Placement = pos=(0,8.6,0) rot=(0,0,1;0rad)
  Solid = true
  Symmetric = false
FEATURE [Sketcher::SketchObject] Sketch038  label="scavo driver solenoide"
  ArcFitTolerance = 1e-06
  AttachmentSupport = -> [XZ_Plane]
  ExternalGeometry = -> [Sketch,Sketch036]
  FullyConstrained = true
  MakeInternals = false
  MapMode = 5
  Placement = pos=(0,0,0) rot=(1,0,0;1.5708rad)
  sketch-geometry (7):
    g0: LineSegment StartX=-192.222 StartY=-8.0175 StartZ=0 EndX=-194.941 EndY=-6.74965 EndZ=0
    g1: LineSegment StartX=-194.941 StartY=-6.74965 StartZ=0 EndX=-212.269 EndY=-43.9083 EndZ=0
    g2: LineSegment StartX=-192.222 StartY=-8.0175 StartZ=0 EndX=-188.779 EndY=-9.62345 EndZ=0
    g3: LineSegment StartX=-188.779 StartY=-9.62345 StartZ=0 EndX=-205.357 EndY=-45.1761 EndZ=0
    g4: LineSegment StartX=-205.357 StartY=-45.1761 StartZ=0 EndX=-209.55 EndY=-45.1761 EndZ=0
    g5: LineSegment [constr] StartX=-212.269 StartY=-43.9083 StartZ=0 EndX=-209.55 EndY=-45.1761 EndZ=0
    g6: LineSegment StartX=-212.269 StartY=-43.9083 StartZ=0 EndX=-209.55 EndY=-45.1761 EndZ=0
  constraints (20):
    c: Coincident(g1,g0)
    c: Coincident(g3,g2)
    c: Coincident(g4,g3)
    c: Distance(g2) = 3.8
    c: Distance(g1) = 41
    c: Coincident(g5,g1)
    c: Distance(g5) = 3
    c: Perpendicular(g5,g-3)
    c: Parallel(g1,g-3)
    c: Perpendicular(g1,g0)
    c: Distance(g0) = 3
    c: Coincident(g6,g1)
    c: Parallel(g3,g-3)
    c: Perpendicular(g2,g3)
    c: Coincident(g2,g0)
    c: Perpendicular(g-4,g4)
    c: PointOnObject(g5,g-3)
    c: Distance(g-3,g5) = 9.6
    c: Coincident(g4,g5)
    c: Coincident(g6,g4)
FEATURE [Part::Extrusion] Extrude041  label="Extrude scavo driver solenoide"
  Base = -> Sketch038
  Dir = (0,-1,2e-16)
  DirMode = 2
  FaceMakerClass = Part::FaceMakerBullseye
  FaceMakerMode = 3
  LengthFwd = 20.6
  LengthRev = 0
  Solid = true
  Symmetric = true
FEATURE [Sketcher::SketchObject] Sketch039  label="scavo per cavo usb per micro"
  ArcFitTolerance = 1e-06
  AttachmentSupport = -> [XZ_Plane]
  ExternalGeometry = -> [Sketch,Sketch016]
  FullyConstrained = true
  MakeInternals = false
  MapMode = 5
  Placement = pos=(0,0,0) rot=(1,0,0;1.5708rad)
  sketch-geometry (4):
    g0: LineSegment StartX=-82.51 StartY=36.4 StartZ=0 EndX=-74.51 EndY=36.4 EndZ=0
    g1: LineSegment StartX=-74.51 StartY=36.4 StartZ=0 EndX=-74.51 EndY=30.8 EndZ=0
    g2: LineSegment StartX=-74.51 StartY=30.8 StartZ=0 EndX=-82.51 EndY=30.8 EndZ=0
    g3: LineSegment StartX=-82.51 StartY=30.8 StartZ=0 EndX=-82.51 EndY=36.4 EndZ=0
  constraints (11):
    c: Coincident(g1,g0)
    c: Vertical(g1)
    c: Coincident(g2,g1)
    c: Horizontal(g2)
    c: Coincident(g3,g2)
    c: Coincident(g3,g0)
    c: Vertical(g3)
    c: Tangent(g0,g-3)
    c: Tangent(g2,g-4)
    c: Tangent(g3,g-4)
    c: Tangent(g1,g-4)
FEATURE [Part::Extrusion] Extrude042  label="Extrude scavo per cavo usb per micro"
  Base = -> Sketch039
  Dir = (0,-1,2e-16)
  DirMode = 2
  FaceMakerClass = Part::FaceMakerBullseye
  FaceMakerMode = 3
  LengthFwd = 11.2
  LengthRev = 0
  Solid = true
  Symmetric = true
FEATURE [Sketcher::SketchObject] Sketch040  label="scavo saldature alimentatore connettore 5v"
  ArcFitTolerance = 1e-06
  AttachmentSupport = -> [XZ_Plane]
  ExternalGeometry = -> [Sketch037]
  FullyConstrained = true
  MakeInternals = false
  MapMode = 5
  Placement = pos=(0,0,0) rot=(1,0,0;1.5708rad)
  sketch-geometry (4):
    g0: LineSegment StartX=-211.175 StartY=-52.4316 StartZ=0 EndX=-211.175 EndY=-56.4316 EndZ=0
    g1: LineSegment StartX=-211.175 StartY=-52.4316 StartZ=0 EndX=-209.575 EndY=-52.4316 EndZ=0
    g2: LineSegment StartX=-209.575 StartY=-52.4316 StartZ=0 EndX=-209.575 EndY=-56.4316 EndZ=0
    g3: LineSegment StartX=-209.575 StartY=-56.4316 StartZ=0 EndX=-211.175 EndY=-56.4316 EndZ=0
  constraints (11):
    c: Vertical(g0)
    c: Coincident(g1,g0)
    c: Horizontal(g1)
    c: Coincident(g2,g1)
    c: Coincident(g3,g2)
    c: Coincident(g3,g0)
    c: Horizontal(g3)
    c: DistanceX(g1,g1) = 1.6
    c: DistanceY(g2,g2) = 4
    c: Tangent(g2,g-3)
    c: DistanceY(g1,g-3) = 2
FEATURE [Part::Extrusion] Extrude043  label="Extrude scavo saldature alimentatore connettore 5v"
  Base = -> Sketch040
  Dir = (0,-1,2e-16)
  DirMode = 2
  FaceMakerClass = Part::FaceMakerBullseye
  FaceMakerMode = 3
  LengthFwd = 8
  LengthRev = 0
  Solid = true
  Symmetric = true
FEATURE [Sketcher::SketchObject] Sketch041  label="scavo saldature alimentatore connettore 5v verticali"
  ArcFitTolerance = 1e-06
  AttachmentSupport = -> [XZ_Plane]
  ExternalGeometry = -> [Sketch037]
  FullyConstrained = true
  MakeInternals = false
  MapMode = 5
  Placement = pos=(0,0,0) rot=(1,0,0;1.5708rad)
  sketch-geometry (4):
    g0: LineSegment StartX=-211.175 StartY=-53.6316 StartZ=0 EndX=-209.575 EndY=-53.6316 EndZ=0
    g1: LineSegment StartX=-209.575 StartY=-53.6316 StartZ=0 EndX=-209.575 EndY=-76.6316 EndZ=0
    g2: LineSegment StartX=-209.575 StartY=-76.6316 StartZ=0 EndX=-211.175 EndY=-76.6316 EndZ=0
    g3: LineSegment StartX=-211.175 StartY=-76.6316 StartZ=0 EndX=-211.175 EndY=-53.6316 EndZ=0
  constraints (11):
    c: Horizontal(g0)
    c: Coincident(g1,g0)
    c: Coincident(g2,g1)
    c: Horizontal(g2)
    c: Coincident(g3,g2)
    c: Coincident(g3,g0)
    c: Vertical(g3)
    c: DistanceY(g3,g3) = 23
    c: DistanceX(g0,g0) = 1.6
    c: Tangent(g1,g-3)
    c: DistanceY(g0,g-3) = 3.2
FEATURE [Part::Extrusion] Extrude044  label="Extrude scavo saldature alimentatore connettore 5v verticali"
  Base = -> Sketch041
  Dir = (0,-1,2e-16)
  DirMode = 2
  FaceMakerClass = Part::FaceMakerBullseye
  FaceMakerMode = 3
  LengthFwd = 3.2
  LengthRev = 0
  Placement = pos=(0,8.3,0) rot=(0,0,1;0rad)
  Solid = true
  Symmetric = false
FEATURE [Sketcher::SketchObject] Sketch042  label="fermi per driver solenoide e alimentatore"
  ArcFitTolerance = 1e-06
  AttachmentSupport = -> [XZ_Plane]
  ExternalGeometry = -> [Sketch036,Sketch037,Sketch,Sketch038]
  FullyConstrained = true
  MakeInternals = false
  MapMode = 5
  Placement = pos=(0,0,0) rot=(1,0,0;1.5708rad)
  sketch-geometry (27):
    g0: LineSegment StartX=-200.506 StartY=-25.7811 StartZ=0 EndX=-201.436 EndY=-27.775 EndZ=0
    g1: LineSegment StartX=-201.436 StartY=-27.775 StartZ=0 EndX=-199.442 EndY=-28.7048 EndZ=0
    g2: LineSegment StartX=-199.442 StartY=-28.7048 StartZ=0 EndX=-198.512 EndY=-26.7109 EndZ=0
    g3: LineSegment StartX=-198.512 StartY=-26.7109 StartZ=0 EndX=-200.506 EndY=-25.7811 EndZ=0
    g4: LineSegment StartX=-201.28 StartY=-23.6549 StartZ=0 EndX=-203.562 EndY=-28.5489 EndZ=0
    g5: LineSegment StartX=-203.562 StartY=-28.5489 StartZ=0 EndX=-200.118 EndY=-30.1549 EndZ=0
    g6: LineSegment StartX=-197.992 StartY=-29.381 StartZ=0 EndX=-197.062 EndY=-27.3871 EndZ=0
    g7: LineSegment StartX=-197.836 StartY=-25.2608 StartZ=0 EndX=-201.28 EndY=-23.6549 EndZ=0
    g8: LineSegment [constr] StartX=-198.668 StartY=-30.8311 StartZ=0 EndX=-197.992 EndY=-29.381 EndZ=0
    g9: LineSegment [constr] StartX=-198.668 StartY=-30.8311 StartZ=0 EndX=-200.118 EndY=-30.1549 EndZ=0
    g10: ArcOfCircle CenterX=-198.512 CenterY=-26.7109 CenterZ=0 NormalX=0 NormalY=0 NormalZ=1 AngleXU=0 Radius=1.6 StartAngle=5.84685 EndAngle=7.41765
    g11: GeomPoint [constr] X=-196.386 Y=-25.937 Z=0
    g12: ArcOfCircle CenterX=-199.442 CenterY=-28.7048 CenterZ=0 NormalX=0 NormalY=0 NormalZ=1 AngleXU=0 Radius=1.6 StartAngle=4.27606 EndAngle=5.84685
    g13: GeomPoint [constr] X=-198.668 Y=-30.8311 Z=0
    g14: LineSegment StartX=-207.775 StartY=-46.8316 StartZ=0 EndX=-207.775 EndY=-50.8316 EndZ=0
    g15: LineSegment StartX=-207.775 StartY=-46.8316 StartZ=0 EndX=-203.775 EndY=-46.8316 EndZ=0
    g16: LineSegment StartX=-203.775 StartY=-46.8316 StartZ=0 EndX=-203.775 EndY=-50.8316 EndZ=0
    g17: LineSegment StartX=-207.775 StartY=-50.8316 StartZ=0 EndX=-203.775 EndY=-50.8316 EndZ=0
    g18: LineSegment StartX=-209.375 StartY=-52.4316 StartZ=0 EndX=-203.775 EndY=-52.4316 EndZ=0
    g19: LineSegment StartX=-202.175 StartY=-50.8316 StartZ=0 EndX=-202.175 EndY=-46.8316 EndZ=0
    g20: LineSegment StartX=-203.775 StartY=-45.2316 StartZ=0 EndX=-209.375 EndY=-45.2316 EndZ=0
    g21: LineSegment StartX=-209.375 StartY=-45.2316 StartZ=0 EndX=-209.375 EndY=-52.4316 EndZ=0
    g22: ArcOfCircle CenterX=-203.775 CenterY=-46.8316 CenterZ=0 NormalX=0 NormalY=0 NormalZ=1 AngleXU=0 Radius=1.6 StartAngle=1.8e-15 EndAngle=1.5708
    g23: GeomPoint [constr] X=-202.175 Y=-45.2316 Z=0
    g24: ArcOfCircle CenterX=-203.775 CenterY=-50.8316 CenterZ=0 NormalX=0 NormalY=0 NormalZ=1 AngleXU=0 Radius=1.6 StartAngle=4.71239 EndAngle=6.28319
    g25: GeomPoint [constr] X=-202.175 Y=-52.4316 Z=0
    g26: LineSegment [constr] StartX=-207.775 StartY=-50.4316 StartZ=0 EndX=-207.775 EndY=-50.8316 EndZ=0
  constraints (69):
    c: Coincident(g1,g0)
    c: Coincident(g2,g1)
    c: Coincident(g3,g2)
    c: Coincident(g3,g0)
    c: Parallel(g0,g2)
    c: Perpendicular(g3,g0)
    c: Perpendicular(g1,g0)
    c: Coincident(g5,g4)
    c: Coincident(g7,g4)
    c: Distance(g3) = 2.2
    c: Distance(g2) = 2.2
    c: Parallel(g6,g2)
    c: Parallel(g6,g4)
    c: Perpendicular(g5,g6)
    c: Perpendicular(g7,g6)
    c: Distance(g13,g11) = 5.4
    c: Distance(g5,g13) = 5.4
    c: Coincident(g9,g8)
    c: Distance(g8) = 1.6
    c: Distance(g9) = 1.6
    c: Perpendicular(g9,g8)
    c: Parallel(g8,g6)
    c: Coincident(g8,g13)
    c: Distance(g8,g1) = 1.6
    c: Distance(g9,g1) = 1.6
    c: Tangent(g0,g-5)
    c: Distance(g0,g-6) = 19.2
    c: PointOnObject(g11,g7)
    c: PointOnObject(g11,g6)
    c: Tangent(g7,g10) = -1.5708
    c: Tangent(g6,g10) = -1.5708
    c: PointOnObject(g13,g5)
    c: Tangent(g5,g12) = -1.5708
    c: Tangent(g6,g12) = -1.5708
    c: Equal(g10,g12)
    c: Coincident(g10,g2)
    c: Vertical(g14)
    c: Coincident(g15,g14)
    c: Horizontal(g15)
    c: Coincident(g16,g15)
    c: Vertical(g16)
    c: Coincident(g17,g14)
    c: Coincident(g17,g16)
    c: Horizontal(g17)
    c: Distance(g16) = 4
    c: Distance(g15) = 4
    c: Horizontal(g18)
    c: Vertical(g19)
    c: Horizontal(g20)
    c: Coincident(g21,g20)
    c: Coincident(g21,g18)
    c: Vertical(g21)
    c: Distance(g20,g23) = 7.2
    c: Distance(g25,g23) = 7.2
    c: DistanceY(g18,g14) = 1.6
    c: DistanceX(g18,g14) = 1.6
    c: PointOnObject(g23,g20)
    c: PointOnObject(g23,g19)
    c: Tangent(g20,g22) = -1.5708
    c: Tangent(g19,g22) = -1.5708
    c: PointOnObject(g25,g19)
    c: Tangent(g18,g24) = -1.5708
    c: Tangent(g19,g24) = -1.5708
    c: Equal(g22,g24)
    c: Coincident(g22,g15)
    c: Vertical(g26)
    c: Distance(g26) = 0.4
    c: Coincident(g26,g-4)
    c: Coincident(g14,g26)
FEATURE [Part::Extrusion] Extrude045  label="Extrude fermi per driver solenoide e alimentatore"
  Base = -> Sketch042
  Dir = (0,-1,2e-16)
  DirMode = 2
  FaceMakerClass = Part::FaceMakerBullseye
  FaceMakerMode = 3
  LengthFwd = 25.2
  LengthRev = 0
  Solid = true
  Symmetric = true
FEATURE [Sketcher::SketchObject] Sketch043  label="scavo pulizia fermo alimentatore"
  ArcFitTolerance = 1e-06
  AttachmentSupport = -> [XZ_Plane]
  ExternalGeometry = -> [Sketch042,Sketch036,Sketch037]
  FullyConstrained = true
  MakeInternals = false
  MapMode = 5
  Placement = pos=(0,0,0) rot=(1,0,0;1.5708rad)
  sketch-geometry (6):
    g0: LineSegment StartX=-209.375 StartY=-52.4316 StartZ=0 EndX=-209.375 EndY=-50.4316 EndZ=0
    g1: LineSegment StartX=-209.375 StartY=-50.4316 StartZ=0 EndX=-207.775 EndY=-50.4316 EndZ=0
    g2: LineSegment StartX=-207.775 StartY=-50.4316 StartZ=0 EndX=-207.775 EndY=-45.2316 EndZ=0
    g3: LineSegment StartX=-207.775 StartY=-45.2316 StartZ=0 EndX=-202.175 EndY=-45.2316 EndZ=0
    g4: LineSegment StartX=-202.175 StartY=-45.2316 StartZ=0 EndX=-202.175 EndY=-52.4316 EndZ=0
    g5: LineSegment StartX=-202.175 StartY=-52.4316 StartZ=0 EndX=-209.375 EndY=-52.4316 EndZ=0
  constraints (13):
    c: Vertical(g0)
    c: Coincident(g1,g0)
    c: Coincident(g2,g1)
    c: Coincident(g3,g2)
    c: Coincident(g4,g3)
    c: Coincident(g5,g4)
    c: Coincident(g5,g0)
    c: Horizontal(g5)
    c: Coincident(g0,g-6)
    c: Tangent(g1,g-8)
    c: Tangent(g2,g-4)
    c: Tangent(g3,g-7)
    c: Tangent(g4,g-3)
FEATURE [Part::Extrusion] Extrude046  label="Extrude scavo pulizia fermo alimentatore"
  Base = -> Sketch043
  Dir = (0,-1,2e-16)
  DirMode = 2
  FaceMakerClass = Part::FaceMakerBullseye
  FaceMakerMode = 3
  LengthFwd = 19.5
  LengthRev = 0
  Solid = true
  Symmetric = true
FEATURE [Sketcher::SketchObject] Sketch044  label="buchini per fissaggio oled"
  ArcFitTolerance = 1e-06
  AttachmentSupport = -> [YZ_Plane]
  ExternalGeometry = -> [Sketch]
  FullyConstrained = true
  MakeInternals = false
  MapMode = 5
  Placement = pos=(0,0,0) rot=(0.57735,0.57735,0.57735;2.0944rad)
  sketch-geometry (5):
    g0: LineSegment [constr] StartX=1.5e-14 StartY=67.3588 StartZ=0 EndX=0 EndY=64.3588 EndZ=0
    g1: LineSegment [constr] StartX=0 StartY=64.3588 StartZ=0 EndX=10.4 EndY=64.3588 EndZ=0
    g2: LineSegment [constr] StartX=0 StartY=64.3588 StartZ=0 EndX=-10.4 EndY=64.3588 EndZ=0
    g3: Circle CenterX=10.4 CenterY=64.3588 CenterZ=0 NormalX=0 NormalY=0 NormalZ=1 AngleXU=0 Radius=1.5
    g4: Circle CenterX=-10.4 CenterY=64.3588 CenterZ=0 NormalX=0 NormalY=0 NormalZ=1 AngleXU=0 Radius=1.5
  constraints (13):
    c: Distance(g0) = 3
    c: PointOnObject(g0,g-2)
    c: Coincident(g1,g0)
    c: Horizontal(g1)
    c: Coincident(g2,g0)
    c: Horizontal(g2)
    c: DistanceX(g1,g1) = 10.4
    c: Coincident(g3,g1)
    c: Diameter(g4) = 3
    c: Coincident(g4,g2)
    c: Coincident(g0,g-7)
    c: Equal(g1,g2)
    c: Equal(g4,g3)
FEATURE [Part::Extrusion] Extrude047  label="Extrude buchini per fissaggio oled"
  Base = -> Sketch044
  Dir = (1,0,0)
  DirMode = 2
  FaceMakerClass = Part::FaceMakerBullseye
  FaceMakerMode = 3
  LengthFwd = 10
  LengthRev = 0
  Placement = pos=(-186,0,0) rot=(0,0,1;0rad)
  Solid = true
  Symmetric = false
FEATURE [Sketcher::SketchObject] Sketch046  label="scavo 5x5 neopixel"
  ArcFitTolerance = 1e-06
  AttachmentSupport = -> [YZ_Plane002]
  FullyConstrained = true
  MakeInternals = false
  MapMode = 5
  Placement = pos=(0,0,0) rot=(0.57735,0.57735,0.57735;2.0944rad)
  sketch-geometry (4):
    g0: LineSegment StartX=-2.7 StartY=2.7 StartZ=0 EndX=2.7 EndY=2.7 EndZ=0
    g1: LineSegment StartX=2.7 StartY=2.7 StartZ=0 EndX=2.7 EndY=-2.7 EndZ=0
    g2: LineSegment StartX=2.7 StartY=-2.7 StartZ=0 EndX=-2.7 EndY=-2.7 EndZ=0
    g3: LineSegment StartX=-2.7 StartY=-2.7 StartZ=0 EndX=-2.7 EndY=2.7 EndZ=0
  constraints (11):
    c: Horizontal(g0)
    c: Coincident(g1,g0)
    c: Vertical(g1)
    c: Coincident(g2,g1)
    c: Horizontal(g2)
    c: Coincident(g3,g2)
    c: Coincident(g3,g0)
    c: Vertical(g3)
    c: DistanceX(g0,g0) = 5.4
    c: DistanceY(g1,g1) = 5.4
    c: Symmetric(g0,g1,g-1)
FEATURE [Sketcher::SketchObject] Sketch047  label="scavo 10x10 neopixel corpo"
  ArcFitTolerance = 1e-06
  AttachmentOffset = pos=(0,0,1) rot=(0,0,1;0rad)
  AttachmentSupport = -> [YZ_Plane002]
  FullyConstrained = true
  MakeInternals = false
  MapMode = 5
  Placement = pos=(1,0,0) rot=(0.57735,0.57735,0.57735;2.0944rad)
  sketch-geometry (4):
    g0: LineSegment StartX=-5 StartY=5.1 StartZ=0 EndX=5 EndY=5.1 EndZ=0
    g1: LineSegment StartX=5 StartY=5.1 StartZ=0 EndX=5 EndY=-5.1 EndZ=0
    g2: LineSegment StartX=5 StartY=-5.1 StartZ=0 EndX=-5 EndY=-5.1 EndZ=0
    g3: LineSegment StartX=-5 StartY=-5.1 StartZ=0 EndX=-5 EndY=5.1 EndZ=0
  constraints (11):
    c: Horizontal(g0)
    c: Coincident(g1,g0)
    c: Vertical(g1)
    c: Coincident(g2,g1)
    c: Horizontal(g2)
    c: Coincident(g3,g2)
    c: Coincident(g3,g0)
    c: Vertical(g3)
    c: DistanceX(g0,g0) = 10
    c: DistanceY(g1,g1) = 10.2
    c: Symmetric(g0,g2,g-1)
FEATURE [Sketcher::SketchObject] Sketch048  label="buco per perno blocco neopixel"
  ArcFitTolerance = 1e-06
  AttachmentSupport = -> [XZ_Plane002]
  FullyConstrained = true
  MakeInternals = false
  MapMode = 5
  Placement = pos=(0,0,0) rot=(1,0,0;1.5708rad)
  sketch-geometry (4):
    g0: LineSegment StartX=3 StartY=1.2 StartZ=0 EndX=3 EndY=-1.2 EndZ=0
    g1: LineSegment StartX=3 StartY=-1.2 StartZ=0 EndX=5.4 EndY=-1.2 EndZ=0
    g2: LineSegment StartX=5.4 StartY=-1.2 StartZ=0 EndX=5.4 EndY=1.2 EndZ=0
    g3: LineSegment StartX=5.4 StartY=1.2 StartZ=0 EndX=3 EndY=1.2 EndZ=0
  constraints (11):
    c: Coincident(g1,g0)
    c: Horizontal(g1)
    c: Coincident(g2,g1)
    c: Vertical(g2)
    c: Coincident(g3,g2)
    c: Coincident(g3,g0)
    c: Horizontal(g3)
    c: DistanceX(g1,g1) = 2.4
    c: DistanceY(g2,g2) = 2.4
    c: Symmetric(g0,g0,g-1)
    c: DistanceX(g-1,g0) = 3
FEATURE [Sketcher::SketchObject] Sketch045  label="blocco principale per neopixel"
  ArcFitTolerance = 1e-06
  AttachmentSupport = -> [XZ_Plane002]
  ExternalGeometry = -> [Sketch048]
  FullyConstrained = true
  MakeInternals = false
  MapMode = 5
  Placement = pos=(0,0,0) rot=(1,0,0;1.5708rad)
  sketch-geometry (6):
    g0: LineSegment StartX=0 StartY=5.1 StartZ=0 EndX=0 EndY=-5.1 EndZ=0
    g1: LineSegment StartX=0 StartY=-5.1 StartZ=0 EndX=3 EndY=-5.1 EndZ=0
    g2: LineSegment StartX=7 StartY=-1.1 StartZ=0 EndX=7 EndY=5.1 EndZ=0
    g3: LineSegment StartX=7 StartY=5.1 StartZ=0 EndX=0 EndY=5.1 EndZ=0
    g4: ArcOfCircle CenterX=3 CenterY=-1.1 CenterZ=0 NormalX=0 NormalY=0 NormalZ=1 AngleXU=0 Radius=4 StartAngle=4.71239 EndAngle=6.28319
    g5: GeomPoint [constr] X=7 Y=-5.1 Z=0
  constraints (15):
    c: Vertical(g0)
    c: Coincident(g1,g0)
    c: Horizontal(g1)
    c: Vertical(g2)
    c: Coincident(g3,g2)
    c: Coincident(g3,g0)
    c: Horizontal(g3)
    c: DistanceY(g0,g0) = 10.2
    c: Symmetric(g0,g0,g-1)
    c: DistanceX(g3,g3) = 7
    c: PointOnObject(g5,g2)
    c: PointOnObject(g5,g1)
    c: Tangent(g2,g4) = -1.5708
    c: Tangent(g1,g4) = -1.5708
    c: DistanceX(g-3,g1) = 0
FEATURE [Sketcher::SketchObject] Sketch049  label="rinforzi esterni per corpo neopoixel"
  ArcFitTolerance = 1e-06
  AttachmentSupport = -> [XZ_Plane002]
  ExternalGeometry = -> [Sketch045]
  FullyConstrained = true
  MakeInternals = false
  MapMode = 5
  Placement = pos=(0,0,0) rot=(1,0,0;1.5708rad)
  sketch-geometry (8):
    g0: LineSegment StartX=1 StartY=-4.1 StartZ=0 EndX=2 EndY=-4.1 EndZ=0
    g1: LineSegment StartX=2 StartY=-4.1 StartZ=0 EndX=2 EndY=-5.1 EndZ=0
    g2: LineSegment StartX=2 StartY=-5.1 StartZ=0 EndX=1 EndY=-5.1 EndZ=0
    g3: LineSegment StartX=1 StartY=-5.1 StartZ=0 EndX=1 EndY=-4.1 EndZ=0
    g4: LineSegment StartX=1 StartY=5.1 StartZ=0 EndX=2 EndY=5.1 EndZ=0
    g5: LineSegment StartX=2 StartY=5.1 StartZ=0 EndX=2 EndY=4.1 EndZ=0
    g6: LineSegment StartX=2 StartY=4.1 StartZ=0 EndX=1 EndY=4.1 EndZ=0
    g7: LineSegment StartX=1 StartY=4.1 StartZ=0 EndX=1 EndY=5.1 EndZ=0
  constraints (24):
    c: Horizontal(g0)
    c: Coincident(g1,g0)
    c: Vertical(g1)
    c: Coincident(g2,g1)
    c: Horizontal(g2)
    c: Coincident(g3,g2)
    c: Coincident(g3,g0)
    c: Vertical(g3)
    c: Horizontal(g4)
    c: Coincident(g5,g4)
    c: Vertical(g5)
    c: Coincident(g6,g5)
    c: Horizontal(g6)
    c: Coincident(g7,g6)
    c: Coincident(g7,g4)
    c: Vertical(g7)
    c: DistanceX(g4,g4) = 1
    c: DistanceY(g5,g5) = 1
    c: DistanceX(g0,g0) = 1
    c: DistanceY(g1,g1) = 1
    c: DistanceX(g-3,g4) = 1
    c: DistanceY(g-3,g4) = 0
    c: DistanceX(g-4,g2) = 1
    c: DistanceY(g2,g-4) = 0
FEATURE [Sketcher::SketchObject] Sketch052  label="scavo saldature driver solenoide"
  ArcFitTolerance = 1e-06
  AttachmentSupport = -> [XZ_Plane]
  ExternalGeometry = -> [Sketch038]
  FullyConstrained = true
  MakeInternals = false
  MapMode = 5
  Placement = pos=(0,0,0) rot=(1,0,0;1.5708rad)
  sketch-geometry (4):
    g0: LineSegment StartX=-195.304 StartY=-6.5806 StartZ=0 EndX=-196.994 EndY=-10.2058 EndZ=0
    g1: LineSegment StartX=-196.994 StartY=-10.2058 StartZ=0 EndX=-196.632 EndY=-10.3749 EndZ=0
    g2: LineSegment StartX=-196.632 StartY=-10.3749 StartZ=0 EndX=-194.941 EndY=-6.74965 EndZ=0
    g3: LineSegment StartX=-194.941 StartY=-6.74965 StartZ=0 EndX=-195.304 EndY=-6.5806 EndZ=0
  constraints (11):
    c: Coincident(g1,g0)
    c: Coincident(g2,g1)
    c: Coincident(g3,g2)
    c: Coincident(g3,g0)
    c: Parallel(g2,g0)
    c: Perpendicular(g2,g3)
    c: Perpendicular(g1,g2,g1) = 1.5708
    c: Parallel(g2,g-3)
    c: Distance(g2) = 4
    c: Distance(g3) = 0.4
    c: Coincident(g2,g-3)
FEATURE [Part::Extrusion] Extrude055  label="Extrude scavo saldature driver solenoide"
  Base = -> Sketch052
  Dir = (0,-1,2e-16)
  DirMode = 2
  FaceMakerClass = Part::FaceMakerBullseye
  FaceMakerMode = 3
  LengthFwd = 6
  LengthRev = 0
  Solid = true
  Symmetric = true
FEATURE [Sketcher::SketchObject] Sketch053  label="scavo saldature rumble"
  ArcFitTolerance = 1e-06
  AttachmentSupport = -> [XZ_Plane]
  ExternalGeometry = -> [Sketch019]
  FullyConstrained = true
  MakeInternals = false
  MapMode = 5
  Placement = pos=(0,0,0) rot=(1,0,0;1.5708rad)
  sketch-geometry (4):
    g0: LineSegment StartX=-164.507 StartY=-41.6446 StartZ=0 EndX=-165.743 EndY=-45.4488 EndZ=0
    g1: LineSegment StartX=-165.743 StartY=-45.4488 StartZ=0 EndX=-164.602 EndY=-45.8196 EndZ=0
    g2: LineSegment StartX=-164.602 StartY=-45.8196 StartZ=0 EndX=-163.366 EndY=-42.0154 EndZ=0
    g3: LineSegment StartX=-163.366 StartY=-42.0154 StartZ=0 EndX=-164.507 EndY=-41.6446 EndZ=0
  constraints (11):
    c: Coincident(g1,g0)
    c: Coincident(g2,g1)
    c: Coincident(g3,g2)
    c: Coincident(g3,g0)
    c: Parallel(g0,g2)
    c: Perpendicular(g3,g0)
    c: Perpendicular(g1,g0)
    c: Parallel(g0,g-3)
    c: Distance(g0) = 4
    c: Distance(g1) = 1.2
    c: Coincident(g0,g-3)
FEATURE [Part::Extrusion] Extrude056  label="Extrude scavo saldature rumble"
  Base = -> Sketch053
  Dir = (0,-1,2e-16)
  DirMode = 2
  FaceMakerClass = Part::FaceMakerBullseye
  FaceMakerMode = 3
  LengthFwd = 8.4
  LengthRev = 0
  Solid = true
  Symmetric = true
FEATURE [Sketcher::SketchObject] Sketch054  label="scavo saldature alimentatore connettore USB"
  ArcFitTolerance = 1e-06
  AttachmentSupport = -> [XZ_Plane]
  ExternalGeometry = -> [Sketch037]
  FullyConstrained = true
  MakeInternals = false
  MapMode = 5
  Placement = pos=(0,0,0) rot=(1,0,0;1.5708rad)
  sketch-geometry (4):
    g0: LineSegment StartX=-209.575 StartY=-80.4316 StartZ=0 EndX=-210.375 EndY=-80.4316 EndZ=0
    g1: LineSegment StartX=-210.375 StartY=-80.4316 StartZ=0 EndX=-210.375 EndY=-72.4316 EndZ=0
    g2: LineSegment StartX=-210.375 StartY=-72.4316 StartZ=0 EndX=-209.575 EndY=-72.4316 EndZ=0
    g3: LineSegment StartX=-209.575 StartY=-72.4316 StartZ=0 EndX=-209.575 EndY=-80.4316 EndZ=0
  constraints (11):
    c: Horizontal(g0)
    c: Coincident(g1,g0)
    c: Vertical(g1)
    c: Coincident(g2,g1)
    c: Horizontal(g2)
    c: Coincident(g3,g2)
    c: Coincident(g3,g0)
    c: Vertical(g3)
    c: DistanceX(g0,g0) = 0.8
    c: DistanceY(g3,g3) = 8
    c: Coincident(g0,g-4)
FEATURE [Part::Extrusion] Extrude057  label="Extrude scavo saldature alimentatore connettore USB"
  Base = -> Sketch054
  Dir = (0,-1,2e-16)
  DirMode = 2
  FaceMakerClass = Part::FaceMakerBullseye
  FaceMakerMode = 3
  LengthFwd = 11
  LengthRev = 0
  Solid = true
  Symmetric = true
FEATURE [Sketcher::SketchObject] Sketch055  label="buco interno per micro switch"
  ArcFitTolerance = 1e-06
  AttachmentSupport = -> [XZ_Plane]
  ExternalGeometry = -> [Sketch]
  FullyConstrained = true
  MakeInternals = false
  MapMode = 5
  Placement = pos=(0,0,0) rot=(1,0,0;1.5708rad)
  sketch-geometry (11):
    g0: LineSegment [constr] StartX=-194.483 StartY=34.2854 StartZ=0 EndX=-196.022 EndY=30.0568 EndZ=0
    g1: LineSegment [constr] StartX=-196.022 StartY=30.0568 StartZ=0 EndX=-197.561 EndY=25.8282 EndZ=0
    g2: LineSegment [constr] StartX=-196.022 StartY=30.0568 StartZ=0 EndX=-194.143 EndY=29.3727 EndZ=0
    g3: LineSegment [constr] StartX=-196.022 StartY=30.0568 StartZ=0 EndX=-197.902 EndY=30.7408 EndZ=0
    g4: LineSegment StartX=-196.362 StartY=34.9694 StartZ=0 EndX=-192.604 EndY=33.6014 EndZ=0
    g5: LineSegment StartX=-199.441 StartY=26.5122 StartZ=0 EndX=-195.682 EndY=25.1441 EndZ=0
    g6: LineSegment StartX=-192.604 StartY=33.6014 StartZ=0 EndX=-195.682 EndY=25.1441 EndZ=0
    g7: LineSegment StartX=-196.362 StartY=34.9694 StartZ=0 EndX=-199.441 EndY=26.5122 EndZ=0
    g8: GeomPoint [constr] X=-187.821 Y=29.2 Z=0
    g9: LineSegment [constr] StartX=-188.505 StartY=27.3206 StartZ=0 EndX=-196.022 EndY=30.0568 EndZ=0
    g10: LineSegment [constr] StartX=-187.821 StartY=29.2 StartZ=0 EndX=-188.505 EndY=27.3206 EndZ=0
  constraints (27):
    c: Coincident(g2,g0)
    c: Parallel(g0,g-3)
    c: Tangent(g1,g0) = -1.5708
    c: Perpendicular(g0,g2)
    c: Tangent(g2,g3)
    c: Distance(g0,g1) = 9
    c: Equal(g0,g1)
    c: Distance(g3,g2) = 4
    c: Equal(g2,g3)
    c: Parallel(g3,g4)
    c: Symmetric(g4,g4,g0)
    c: Parallel(g6,g1)
    c: Parallel(g7,g1)
    c: Symmetric(g6,g6,g2)
    c: Symmetric(g5,g5,g1)
    c: Symmetric(g7,g7,g3)
    c: Coincident(g7,g4)
    c: Coincident(g6,g4)
    c: Coincident(g5,g6)
    c: Symmetric(g-3,g-3,g8)
    c: Perpendicular(g-3,g9)
    c: Distance(g9) = 8
    c: Coincident(g3,g9)
    c: Coincident(g10,g8)
    c: Parallel(g10,g-3)
    c: Distance(g10) = 2
    c: Coincident(g10,g9)
FEATURE [Sketcher::SketchObject] Sketch056  label="buco esterno per micro switch"
  ArcFitTolerance = 1e-06
  AttachmentSupport = -> [XZ_Plane]
  ExternalGeometry = -> [Sketch055]
  FullyConstrained = true
  MakeInternals = false
  MapMode = 5
  Placement = pos=(0,0,0) rot=(1,0,0;1.5708rad)
  sketch-geometry (17):
    g0: GeomPoint [constr] X=-194.143 Y=29.3727 Z=0
    g1: GeomPoint [constr] X=-194.483 Y=34.2854 Z=0
    g2: GeomPoint [constr] X=-197.902 Y=30.7408 Z=0
    g3: GeomPoint [constr] X=-197.561 Y=25.8282 Z=0
    g4: GeomPoint [constr] X=-196.022 Y=30.0568 Z=0
    g5: LineSegment [constr] StartX=-194.483 StartY=34.2854 StartZ=0 EndX=-196.022 EndY=30.0568 EndZ=0
    g6: LineSegment [constr] StartX=-196.022 StartY=30.0568 StartZ=0 EndX=-197.561 EndY=25.8282 EndZ=0
    g7: LineSegment [constr] StartX=-197.902 StartY=30.7408 StartZ=0 EndX=-196.022 EndY=30.0568 EndZ=0
    g8: LineSegment [constr] StartX=-196.022 StartY=30.0568 StartZ=0 EndX=-194.143 EndY=29.3727 EndZ=0
    g9: LineSegment [constr] StartX=-195.338 StartY=31.9362 StartZ=0 EndX=-196.022 EndY=30.0568 EndZ=0
    g10: LineSegment [constr] StartX=-196.022 StartY=30.0568 StartZ=0 EndX=-196.706 EndY=28.1774 EndZ=0
    g11: LineSegment [constr] StartX=-196.022 StartY=30.0568 StartZ=0 EndX=-196.821 EndY=30.3475 EndZ=0
    g12: LineSegment [constr] StartX=-196.022 StartY=30.0568 StartZ=0 EndX=-195.223 EndY=29.7661 EndZ=0
    g13: LineSegment StartX=-194.539 StartY=31.6454 StartZ=0 EndX=-195.907 EndY=27.8867 EndZ=0
    g14: LineSegment StartX=-196.137 StartY=32.2269 StartZ=0 EndX=-197.505 EndY=28.4681 EndZ=0
    g15: LineSegment StartX=-196.137 StartY=32.2269 StartZ=0 EndX=-194.539 EndY=31.6454 EndZ=0
    g16: LineSegment StartX=-197.505 StartY=28.4681 StartZ=0 EndX=-195.907 EndY=27.8867 EndZ=0
  constraints (34):
    c: Symmetric(g-5,g-5,g1)
    c: Symmetric(g-5,g-6,g0)
    c: Symmetric(g-6,g-6,g3)
    c: Symmetric(g-5,g-6,g2)
    c: Coincident(g5,g1)
    c: Coincident(g5,g4)
    c: Coincident(g6,g4)
    c: Coincident(g6,g3)
    c: Equal(g5,g6)
    c: Coincident(g7,g2)
    c: Coincident(g7,g4)
    c: Coincident(g8,g4)
    c: Coincident(g8,g0)
    c: Equal(g7,g8)
    c: Coincident(g11,g9)
    c: Coincident(g12,g9)
    c: Tangent(g10,g9) = -1.5708
    c: Perpendicular(g11,g9)
    c: Parallel(g9,g-4)
    c: Equal(g9,g10)
    c: Parallel(g12,g11)
    c: Equal(g11,g12)
    c: Distance(g11,g12) = 1.7
    c: Distance(g9,g10) = 4
    c: Symmetric(g13,g13,g12)
    c: Parallel(g13,g9)
    c: Symmetric(g14,g14,g11)
    c: Symmetric(g15,g15,g9)
    c: Parallel(g15,g11)
    c: Symmetric(g16,g16,g10)
    c: Coincident(g16,g14)
    c: Coincident(g15,g14)
    c: Coincident(g13,g15)
    c: Coincident(g9,g4)
FEATURE [Sketcher::SketchObject] Sketch057  label="buco interno per SWITCH"
  ArcFitTolerance = 1e-06
  AttachmentSupport = -> [XZ_Plane]
  ExternalGeometry = -> [Sketch]
  FullyConstrained = true
  MakeInternals = false
  MapMode = 5
  Placement = pos=(0,0,0) rot=(1,0,0;1.5708rad)
  sketch-geometry (10):
    g0: GeomPoint [constr] X=-187.821 Y=29.2 Z=0
    g1: LineSegment [constr] StartX=-188.505 StartY=27.3206 StartZ=0 EndX=-193.203 EndY=29.0307 EndZ=0
    g2: LineSegment [constr] StartX=-190.809 StartY=35.6086 StartZ=0 EndX=-195.597 EndY=22.4529 EndZ=0
    g3: GeomPoint [constr] X=-193.203 Y=29.0307 Z=0
    g4: LineSegment [constr] StartX=-196.492 StartY=30.2278 StartZ=0 EndX=-189.914 EndY=27.8336 EndZ=0
    g5: LineSegment StartX=-194.098 StartY=36.8056 StartZ=0 EndX=-187.52 EndY=34.4115 EndZ=0
    g6: LineSegment StartX=-194.098 StartY=36.8056 StartZ=0 EndX=-198.886 EndY=23.6499 EndZ=0
    g7: LineSegment StartX=-187.52 StartY=34.4115 StartZ=0 EndX=-192.308 EndY=21.2558 EndZ=0
    g8: LineSegment StartX=-198.886 StartY=23.6499 StartZ=0 EndX=-192.308 EndY=21.2558 EndZ=0
    g9: LineSegment [constr] StartX=-187.821 StartY=29.2 StartZ=0 EndX=-188.505 EndY=27.3206 EndZ=0
  constraints (23):
    c: Symmetric(g-3,g-3,g0)
    c: Perpendicular(g1,g-3)
    c: Parallel(g2,g-3)
    c: Symmetric(g2,g2,g3)
    c: Perpendicular(g2,g4)
    c: Symmetric(g4,g4,g3)
    c: Distance(g2) = 14
    c: Distance(g4) = 7
    c: Distance(g1) = 5
    c: Parallel(g5,g4)
    c: Parallel(g7,g2)
    c: Symmetric(g5,g5,g2)
    c: Symmetric(g6,g6,g4)
    c: Symmetric(g7,g7,g4)
    c: Symmetric(g8,g8,g2)
    c: Coincident(g6,g5)
    c: Coincident(g7,g5)
    c: Coincident(g8,g7)
    c: Coincident(g3,g1)
    c: Coincident(g9,g0)
    c: Parallel(g9,g-3)
    c: Distance(g9) = 2
    c: Coincident(g1,g9)
FEATURE [Sketcher::SketchObject] Sketch058  label="buco esterno per SWITCH"
  ArcFitTolerance = 1e-06
  AttachmentSupport = -> [XZ_Plane]
  ExternalGeometry = -> [Sketch057]
  FullyConstrained = true
  MakeInternals = false
  MapMode = 5
  Placement = pos=(0,0,0) rot=(1,0,0;1.5708rad)
  sketch-geometry (12):
    g0: GeomPoint [constr] X=-190.809 Y=35.6086 Z=0
    g1: GeomPoint [constr] X=-196.492 Y=30.2278 Z=0
    g2: GeomPoint [constr] X=-189.914 Y=27.8336 Z=0
    g3: GeomPoint [constr] X=-195.597 Y=22.4529 Z=0
    g4: GeomPoint [constr] X=-193.203 Y=29.0307 Z=0
    g5: LineSegment [constr] StartX=-192.006 StartY=32.3196 StartZ=0 EndX=-194.4 EndY=25.7418 EndZ=0
    g6: GeomPoint [constr] X=-193.203 Y=29.0307 Z=0
    g7: LineSegment [constr] StartX=-195.082 StartY=29.7148 StartZ=0 EndX=-191.324 EndY=28.3467 EndZ=0
    g8: LineSegment StartX=-193.885 StartY=33.0037 StartZ=0 EndX=-190.127 EndY=31.6356 EndZ=0
    g9: LineSegment StartX=-190.127 StartY=31.6356 StartZ=0 EndX=-192.521 EndY=25.0578 EndZ=0
    g10: LineSegment StartX=-196.28 StartY=26.4258 StartZ=0 EndX=-192.521 EndY=25.0578 EndZ=0
    g11: LineSegment StartX=-193.885 StartY=33.0037 StartZ=0 EndX=-196.28 EndY=26.4258 EndZ=0
  constraints (21):
    c: Symmetric(g-6,g-6,g3)
    c: Symmetric(g-4,g-6,g2)
    c: Symmetric(g-5,g-4,g0)
    c: Symmetric(g-5,g-6,g1)
    c: Symmetric(g1,g2,g4)
    c: Parallel(g5,g-4)
    c: Symmetric(g5,g5,g6)
    c: Perpendicular(g7,g5)
    c: Symmetric(g7,g7,g6)
    c: Distance(g5) = 7
    c: Distance(g7) = 4
    c: Parallel(g8,g7)
    c: Parallel(g11,g5)
    c: Symmetric(g8,g8,g5)
    c: Symmetric(g9,g9,g7)
    c: Symmetric(g10,g10,g5)
    c: Symmetric(g11,g11,g7)
    c: Coincident(g11,g8)
    c: Coincident(g9,g8)
    c: Coincident(g9,g10)
    c: Coincident(g6,g4)
FEATURE [Part::Extrusion] Extrude060  label="Extrude buco interno per SWITCH destro"
  Base = -> Sketch057
  Dir = (0,-1,2e-16)
  DirMode = 2
  FaceMakerClass = Part::FaceMakerBullseye
  FaceMakerMode = 3
  LengthFwd = 13.2
  LengthRev = 0
  Placement = pos=(0,2.6,0) rot=(0,0,1;0rad)
  Solid = true
  Symmetric = false
FEATURE [Part::Extrusion] Extrude061  label="Extrude buco esterno per SWITCH destro"
  Base = -> Sketch058
  Dir = (0,-1,2e-16)
  DirMode = 2
  FaceMakerClass = Part::FaceMakerBullseye
  FaceMakerMode = 3
  LengthFwd = 2
  LengthRev = 0
  Placement = pos=(0,-10.6,0) rot=(0,0,1;0rad)
  Solid = true
  Symmetric = false
FEATURE [Sketcher::SketchObject] Sketch059  label="buco per spazio introduzione SWITCH"
  ArcFitTolerance = 1e-06
  AttachmentSupport = -> [XZ_Plane]
  ExternalGeometry = -> [Sketch057,Sketch010]
  FullyConstrained = true
  MakeInternals = false
  MapMode = 5
  Placement = pos=(0,0,0) rot=(1,0,0;1.5708rad)
  sketch-geometry (8):
    g0: LineSegment [constr] StartX=-201.368 StartY=36.3521 StartZ=0 EndX=-195.094 EndY=34.0687 EndZ=0
    g1: LineSegment [constr] StartX=-194.098 StartY=36.8056 StartZ=0 EndX=-195.094 EndY=34.0687 EndZ=0
    g2: LineSegment StartX=-198.658 StartY=24.2771 StartZ=0 EndX=-199.654 EndY=21.5401 EndZ=0
    g3: LineSegment StartX=-199.654 StartY=21.5401 StartZ=0 EndX=-181.196 EndY=14.822 EndZ=0
    g4: LineSegment StartX=-181.196 StartY=14.822 StartZ=0 EndX=-180.2 EndY=17.559 EndZ=0
    g5: LineSegment StartX=-180.2 StartY=17.559 StartZ=0 EndX=-198.658 EndY=24.2771 EndZ=0
    g6: LineSegment [constr] StartX=-204.932 StartY=26.5605 StartZ=0 EndX=-198.658 EndY=24.2771 EndZ=0
    g7: LineSegment [constr] StartX=-198.658 StartY=24.2771 StartZ=0 EndX=-199.654 EndY=21.5401 EndZ=0
  constraints (20):
    c: Parallel(g1,g-3)
    c: Parallel(g0,g-4)
    c: Coincident(g0,g-4)
    c: Coincident(g1,g-3)
    c: Coincident(g0,g1)
    c: Coincident(g3,g2)
    c: Coincident(g4,g3)
    c: Coincident(g5,g4)
    c: Coincident(g5,g2)
    c: Parallel(g5,g-5)
    c: Parallel(g3,g-5)
    c: Parallel(g4,g-6)
    c: DistanceX(g-6,g4) = 0
    c: Coincident(g6,g-5)
    c: Equal(g6,g0)
    c: Coincident(g7,g6)
    c: Equal(g7,g1)
    c: Tangent(g7,g-3)
    c: Coincident(g2,g6)
    c: Coincident(g2,g7)
FEATURE [Part::Extrusion] Extrude062  label="Extrude buco per spazio introduzione SWITCH"
  Base = -> Sketch059
  Dir = (0,-1,2e-16)
  DirMode = 2
  FaceMakerClass = Part::FaceMakerBullseye
  FaceMakerMode = 3
  LengthFwd = 13.2
  LengthRev = 0
  Solid = true
  Symmetric = true
FEATURE [Part::Extrusion] Extrude063  label="Extrude buco interno per SWITCH sinistro"
  Base = -> Sketch057
  Dir = (0,-1,2e-16)
  DirMode = 2
  FaceMakerClass = Part::FaceMakerBullseye
  FaceMakerMode = 3
  LengthFwd = 13.2
  LengthRev = 0
  Placement = pos=(0,10.6,0) rot=(0,0,1;0rad)
  Solid = true
  Symmetric = false
FEATURE [Part::Extrusion] Extrude064  label="Extrude buco esterno per SWITCH sinistro"
  Base = -> Sketch058
  Dir = (0,-1,2e-16)
  DirMode = 2
  FaceMakerClass = Part::FaceMakerBullseye
  FaceMakerMode = 3
  LengthFwd = 2
  LengthRev = 0
  Placement = pos=(0,12.6,0) rot=(0,0,1;0rad)
  Solid = true
  Symmetric = false
FEATURE [Sketcher::SketchObject] Sketch061  label="struttura esterna blocco switch"
  ArcFitTolerance = 1e-06
  AttachmentSupport = -> [XZ_Plane003]
  FullyConstrained = true
  MakeInternals = false
  MapMode = 5
  Placement = pos=(0,0,0) rot=(1,0,0;1.5708rad)
  sketch-geometry (5):
    g0: LineSegment StartX=-1 StartY=-5.1 StartZ=0 EndX=1 EndY=-5.1 EndZ=0
    g1: LineSegment StartX=1 StartY=-5.1 StartZ=0 EndX=1 EndY=5.1 EndZ=0
    g2: LineSegment StartX=1 StartY=5.1 StartZ=0 EndX=-1 EndY=5.1 EndZ=0
    g3: LineSegment StartX=-1 StartY=5.1 StartZ=0 EndX=-1 EndY=-5.1 EndZ=0
    g4: GeomPoint [constr] X=0 Y=0 Z=0
  constraints (12):
    c: Coincident(g0,g1)
    c: Coincident(g1,g2)
    c: Coincident(g2,g3)
    c: Coincident(g3,g0)
    c: Horizontal(g0)
    c: Horizontal(g2)
    c: Vertical(g1)
    c: Vertical(g3)
    c: Symmetric(g2,g0,g4)
    c: Distance(g1,g3) = 2
    c: Distance(g0,g2) = 10.2
    c: Coincident(g4,g-1)
FEATURE [Sketcher::SketchObject] Sketch062  label="struttura interna blocco switch"
  ArcFitTolerance = 1e-06
  AttachmentSupport = -> [XZ_Plane003]
  ExternalGeometry = -> [Sketch061]
  FullyConstrained = true
  MakeInternals = false
  MapMode = 5
  Placement = pos=(0,0,0) rot=(1,0,0;1.5708rad)
  sketch-geometry (5):
    g0: LineSegment StartX=-1 StartY=3.1 StartZ=0 EndX=-1 EndY=-3.1 EndZ=0
    g1: LineSegment StartX=-1 StartY=-3.1 StartZ=0 EndX=1 EndY=-3.1 EndZ=0
    g2: LineSegment StartX=1 StartY=-3.1 StartZ=0 EndX=1 EndY=3.1 EndZ=0
    g3: LineSegment StartX=1 StartY=3.1 StartZ=0 EndX=-1 EndY=3.1 EndZ=0
    g4: GeomPoint [constr] X=0 Y=0 Z=0
  constraints (12):
    c: Coincident(g0,g1)
    c: Coincident(g1,g2)
    c: Coincident(g2,g3)
    c: Coincident(g3,g0)
    c: Vertical(g0)
    c: Vertical(g2)
    c: Horizontal(g1)
    c: Horizontal(g3)
    c: Symmetric(g2,g0,g4)
    c: Coincident(g4,g-1)
    c: Distance(g0) = 6.2
    c: Equal(g3,g-3)
FEATURE [Sketcher::SketchObject] Sketch063  label="blocchi tra switch"
  ArcFitTolerance = 1e-06
  AttachmentSupport = -> [XZ_Plane003]
  ExternalGeometry = -> [Sketch061,Sketch062]
  FullyConstrained = true
  MakeInternals = false
  MapMode = 5
  Placement = pos=(0,0,0) rot=(1,0,0;1.5708rad)
  sketch-geometry (8):
    g0: LineSegment StartX=-3 StartY=5.1 StartZ=0 EndX=-1 EndY=5.1 EndZ=0
    g1: LineSegment StartX=-1 StartY=5.1 StartZ=0 EndX=-1 EndY=3.1 EndZ=0
    g2: LineSegment StartX=-1 StartY=3.1 StartZ=0 EndX=-3 EndY=3.1 EndZ=0
    g3: LineSegment StartX=-3 StartY=3.1 StartZ=0 EndX=-3 EndY=5.1 EndZ=0
    g4: LineSegment StartX=-3 StartY=-3.1 StartZ=0 EndX=-1 EndY=-3.1 EndZ=0
    g5: LineSegment StartX=-1 StartY=-3.1 StartZ=0 EndX=-1 EndY=-5.1 EndZ=0
    g6: LineSegment StartX=-1 StartY=-5.1 StartZ=0 EndX=-3 EndY=-5.1 EndZ=0
    g7: LineSegment StartX=-3 StartY=-5.1 StartZ=0 EndX=-3 EndY=-3.1 EndZ=0
  constraints (20):
    c: Horizontal(g0)
    c: Coincident(g1,g0)
    c: Coincident(g2,g1)
    c: Horizontal(g2)
    c: Coincident(g3,g2)
    c: Coincident(g3,g0)
    c: Vertical(g3)
    c: Horizontal(g4)
    c: Coincident(g5,g4)
    c: Coincident(g6,g5)
    c: Horizontal(g6)
    c: Coincident(g7,g6)
    c: Coincident(g7,g4)
    c: Vertical(g7)
    c: Coincident(g0,g-4)
    c: Coincident(g1,g-5)
    c: Coincident(g4,g-6)
    c: Coincident(g5,g-7)
    c: Distance(g0) = 2
    c: Distance(g4) = 2
FEATURE [Sketcher::SketchObject] Sketch066  label="piano per rampino"
  ArcFitTolerance = 1e-06
  AttachmentSupport = -> [XZ_Plane002]
  ExternalGeometry = -> [Sketch045]
  FullyConstrained = true
  MakeInternals = false
  MapMode = 5
  Placement = pos=(0,0,0) rot=(1,0,0;1.5708rad)
  sketch-geometry (4):
    g0: LineSegment StartX=5.4 StartY=5.1 StartZ=0 EndX=5.4 EndY=3.9 EndZ=0
    g1: LineSegment StartX=5.4 StartY=3.9 StartZ=0 EndX=7 EndY=3.9 EndZ=0
    g2: LineSegment StartX=7 StartY=3.9 StartZ=0 EndX=7 EndY=5.1 EndZ=0
    g3: LineSegment StartX=7 StartY=5.1 StartZ=0 EndX=5.4 EndY=5.1 EndZ=0
  constraints (11):
    c: Coincident(g0,g1)
    c: Coincident(g1,g2)
    c: Coincident(g2,g3)
    c: Coincident(g3,g0)
    c: Vertical(g0)
    c: Vertical(g2)
    c: Horizontal(g1)
    c: Horizontal(g3)
    c: Distance(g0,g2) = 1.6
    c: Distance(g1,g3) = 1.2
    c: Coincident(g2,g-3)
FEATURE [Sketcher::SketchObject] Sketch064  label="rampini_per_serraggio_struttura"
  ArcFitTolerance = 1e-06
  AttachmentSupport = -> [XZ_Plane002]
  ExternalGeometry = -> [Sketch066,Sketch045]
  FullyConstrained = true
  MakeInternals = false
  MapMode = 5
  Placement = pos=(0,0,0) rot=(1,0,0;1.5708rad)
  sketch-geometry (7):
    g0: LineSegment StartX=7 StartY=5.1 StartZ=0 EndX=7 EndY=3.9 EndZ=0
    g1: LineSegment StartX=7 StartY=3.9 StartZ=0 EndX=9 EndY=3.9 EndZ=0
    g2: LineSegment StartX=7 StartY=5.1 StartZ=0 EndX=7 EndY=5.1 EndZ=0
    g3: LineSegment StartX=7 StartY=5.1 StartZ=0 EndX=7 EndY=7.5 EndZ=0
    g4: LineSegment StartX=9 StartY=5.1 StartZ=0 EndX=9 EndY=3.9 EndZ=0
    g5: LineSegment StartX=7 StartY=7.5 StartZ=0 EndX=9 EndY=7.5 EndZ=0
    g6: LineSegment StartX=9 StartY=7.5 StartZ=0 EndX=9 EndY=5.1 EndZ=0
  constraints (20):
    c: Vertical(g0)
    c: Coincident(g1,g0)
    c: Horizontal(g1)
    c: Coincident(g2,g0)
    c: Horizontal(g2)
    c: Coincident(g3,g2)
    c: Vertical(g3)
    c: Coincident(g5,g3)
    c: Coincident(g4,g6)
    c: Coincident(g4,g1)
    c: Vertical(g4)
    c: Coincident(g0,g-3)
    c: DistanceY(g-4,g3) = 2.4
    c: DistanceX(g1,g1) = 2
    c: DistanceY(g2,g6) = 0
    c: DistanceX(g2,g2) = 0
    c: DistanceY(g0,g0) = 1.2
    c: Coincident(g5,g6)
    c: Horizontal(g5)
    c: Vertical(g6)
FEATURE [Sketcher::SketchObject] Sketch067  label="perno per blocco switch"
  ArcFitTolerance = 1e-06
  AttachmentSupport = -> [XZ_Plane]
  ExternalGeometry = -> [Sketch,Sketch010]
  FullyConstrained = true
  MakeInternals = false
  MapMode = 5
  Placement = pos=(0,0,0) rot=(1,0,0;1.5708rad)
  sketch-geometry (14):
    g0: LineSegment StartX=-191.073 StartY=24.9429 StartZ=0 EndX=-185.81 EndY=23.0276 EndZ=0
    g1: LineSegment StartX=-183.76 StartY=23.9839 StartZ=0 EndX=-182.392 EndY=27.7427 EndZ=0
    g2: LineSegment StartX=-183.348 StartY=29.7934 StartZ=0 EndX=-188.61 EndY=31.7087 EndZ=0
    g3: LineSegment StartX=-188.61 StartY=31.7087 StartZ=0 EndX=-191.073 EndY=24.9429 EndZ=0
    g4: GeomPoint [constr] X=-186.459 Y=27.0946 Z=0
    g5: LineSegment StartX=-189.022 StartY=25.8992 StartZ=0 EndX=-185.263 EndY=24.5311 EndZ=0
    g6: LineSegment StartX=-185.263 StartY=24.5311 StartZ=0 EndX=-183.895 EndY=28.2899 EndZ=0
    g7: LineSegment StartX=-183.895 StartY=28.2899 StartZ=0 EndX=-187.654 EndY=29.658 EndZ=0
    g8: LineSegment StartX=-187.654 StartY=29.658 StartZ=0 EndX=-189.022 EndY=25.8992 EndZ=0
    g9: GeomPoint [constr] X=-186.459 Y=27.0946 Z=0
    g10: ArcOfCircle CenterX=-185.263 CenterY=24.5311 CenterZ=0 NormalX=0 NormalY=0 NormalZ=1 AngleXU=0 Radius=1.6 StartAngle=4.36332 EndAngle=5.93412
    g11: GeomPoint [constr] X=-184.307 Y=22.4804 Z=0
    g12: ArcOfCircle CenterX=-183.895 CenterY=28.2899 CenterZ=0 NormalX=0 NormalY=0 NormalZ=1 AngleXU=0 Radius=1.6 StartAngle=5.93412 EndAngle=7.50492
    g13: GeomPoint [constr] X=-181.844 Y=29.2462 Z=0
  constraints (30):
    c: Coincident(g2,g3)
    c: Coincident(g3,g0)
    c: Symmetric(g13,g0,g4)
    c: Distance(g11,g3) = 7.2
    c: Distance(g0,g2) = 7.2
    c: Parallel(g3,g1)
    c: Parallel(g2,g0)
    c: Perpendicular(g2,g3)
    c: Coincident(g5,g6)
    c: Coincident(g6,g7)
    c: Coincident(g7,g8)
    c: Coincident(g8,g5)
    c: Symmetric(g7,g5,g9)
    c: Distance(g6,g8) = 4
    c: Distance(g5,g7) = 4
    c: Coincident(g9,g4)
    c: Parallel(g8,g6)
    c: Parallel(g7,g5)
    c: Perpendicular(g7,g8)
    c: Tangent(g8,g-3)
    c: Tangent(g2,g-4)
    c: PointOnObject(g11,g1)
    c: PointOnObject(g11,g0)
    c: Tangent(g1,g10) = -1.5708
    c: Tangent(g0,g10) = -1.5708
    c: PointOnObject(g13,g1)
    c: Tangent(g1,g12) = -1.5708
    c: Tangent(g2,g12) = -1.5708
    c: Equal(g10,g12)
    c: Coincident(g10,g5)
FEATURE [Part::Extrusion] Extrude072  label="Extrude perno per blocco switch"
  Base = -> Sketch067
  Dir = (0,-1,2e-16)
  DirMode = 2
  FaceMakerClass = Part::FaceMakerBullseye
  FaceMakerMode = 3
  LengthFwd = 25.2
  LengthRev = 0
  Solid = true
  Symmetric = true
FEATURE [Part::MultiFuse] Fusion
  Refine = true
  Shapes = -> [Extrude,Sweep,Extrude007,Extrude011,Extrude005,Extrude012,Extrude013,Extrude016,Extrude031,Extrude039,Extrude045,Extrude072]
FEATURE [Part::Cut] Cut
  Base = -> Fusion
  Refine = true
  Tool = -> Extrude001
FEATURE [Part::Cut] Cut001
  Base = -> Cut
  Refine = true
  Tool = -> Extrude004
FEATURE [Part::Cut] Cut002
  Base = -> Cut001
  Refine = true
  Tool = -> Extrude006
FEATURE [Part::Cut] Cut003
  Base = -> Cut002
  Refine = true
  Tool = -> Extrude008
FEATURE [Part::Cut] Cut004
  Base = -> Cut003
  Refine = true
  Tool = -> Extrude009
FEATURE [Part::Cut] Cut005
  Base = -> Cut004
  Refine = true
  Tool = -> Extrude010
FEATURE [Part::Cut] Cut006
  Base = -> Cut005
  Refine = true
  Tool = -> Extrude014
FEATURE [Part::Cut] Cut007
  Base = -> Cut006
  Refine = true
  Tool = -> Extrude015
FEATURE [Part::Cut] Cut008
  Base = -> Cut007
  Refine = true
  Tool = -> Extrude018
FEATURE [Part::Cut] Cut009
  Base = -> Cut008
  Refine = true
  Tool = -> Extrude019
FEATURE [Part::Cut] Cut010
  Base = -> Cut009
  Refine = true
  Tool = -> Extrude020
FEATURE [Part::Cut] Cut011
  Base = -> Cut010
  Refine = true
  Tool = -> Extrude021
FEATURE [Part::Cut] Cut012
  Base = -> Cut011
  Refine = true
  Tool = -> Extrude022
FEATURE [Part::Cut] Cut013
  Base = -> Cut012
  Refine = true
  Tool = -> Extrude023
FEATURE [Part::Cut] Cut014
  Base = -> Cut013
  Refine = true
  Tool = -> Extrude032
FEATURE [Part::Cut] Cut015
  Base = -> Cut014
  Refine = true
  Tool = -> Extrude033
FEATURE [Part::Cut] Cut016
  Base = -> Cut015
  Refine = true
  Tool = -> Extrude034
FEATURE [Part::Cut] Cut017
  Base = -> Cut016
  Refine = true
  Tool = -> Extrude035
FEATURE [Part::Cut] Cut018
  Base = -> Cut017
  Refine = true
  Tool = -> Extrude036
FEATURE [Part::Cut] Cut019
  Base = -> Cut018
  Refine = true
  Tool = -> Extrude037
FEATURE [Part::Cut] Cut020
  Base = -> Cut019
  Refine = true
  Tool = -> Extrude030
FEATURE [Part::Cut] Cut022
  Base = -> Cut020
  Refine = true
  Tool = -> Extrude038
FEATURE [Part::Cut] Cut023
  Base = -> Cut022
  Refine = true
  Tool = -> Extrude041
FEATURE [Part::Cut] Cut024
  Base = -> Cut023
  Refine = true
  Tool = -> Extrude040
FEATURE [Part::Cut] Cut025
  Base = -> Cut024
  Refine = true
  Tool = -> Extrude042
FEATURE [Part::Cut] Cut026
  Base = -> Cut025
  Refine = true
  Tool = -> Extrude043
FEATURE [Part::Cut] Cut027
  Base = -> Cut026
  Refine = true
  Tool = -> Extrude044
FEATURE [Part::Cut] Cut028
  Base = -> Cut027
  Refine = true
  Tool = -> Extrude046
FEATURE [Part::Cut] Cut029
  Base = -> Cut028
  Refine = true
  Tool = -> Extrude047
FEATURE [Part::Cut] Cut033
  Base = -> Cut029
  Refine = true
  Tool = -> Extrude055
FEATURE [Part::Cut] Cut034
  Base = -> Cut033
  Refine = true
  Tool = -> Extrude056
FEATURE [Part::Cut] Cut035
  Base = -> Cut034
  Refine = true
  Tool = -> Extrude057
FEATURE [Part::Cut] Cut037
  Base = -> Cut035
  Refine = true
  Tool = -> Extrude060
FEATURE [Part::Cut] Cut038
  Base = -> Cut037
  Refine = true
  Tool = -> Extrude061
FEATURE [Part::Cut] Cut039
  Base = -> Cut038
  Refine = true
  Tool = -> Extrude063
FEATURE [Part::Cut] Cut040
  Base = -> Cut039
  Refine = true
  Tool = -> Extrude064
FEATURE [Part::Cut] Cut041
  Base = -> Cut040
  Refine = true
  Tool = -> Extrude062
FEATURE [Sketcher::SketchObject] Sketch068  label="base con smusso sopra neopixel"
  ArcFitTolerance = 1e-06
  AttachmentSupport = -> [YZ_Plane002]
  FullyConstrained = true
  MakeInternals = false
  MapMode = 5
  Placement = pos=(0,0,0) rot=(0.57735,0.57735,0.57735;2.0944rad)
  sketch-geometry (5):
    g0: LineSegment StartX=-9.5 StartY=-6.1 StartZ=0 EndX=9.5 EndY=-6.1 EndZ=0
    g1: LineSegment StartX=9.5 StartY=-6.1 StartZ=0 EndX=9.5 EndY=6.1 EndZ=0
    g2: LineSegment StartX=9.5 StartY=6.1 StartZ=0 EndX=-9.5 EndY=6.1 EndZ=0
    g3: LineSegment StartX=-9.5 StartY=6.1 StartZ=0 EndX=-9.5 EndY=-6.1 EndZ=0
    g4: GeomPoint [constr] X=0 Y=0 Z=0
  constraints (12):
    c: Coincident(g0,g1)
    c: Coincident(g1,g2)
    c: Coincident(g2,g3)
    c: Coincident(g3,g0)
    c: Horizontal(g0)
    c: Horizontal(g2)
    c: Vertical(g1)
    c: Vertical(g3)
    c: Symmetric(g2,g0,g4)
    c: Distance(g1,g3) = 19
    c: Distance(g0,g2) = 12.2
    c: Coincident(g4,g-1)
FEATURE [Sketcher::SketchObject] Sketch069  label="cilindro minore"
  ArcFitTolerance = 1e-06
  AttachmentSupport = -> [XZ_Plane004]
  FullyConstrained = true
  MakeInternals = false
  MapMode = 5
  Placement = pos=(0,0,0) rot=(1,0,0;1.5708rad)
  sketch-geometry (1):
    g0: Circle CenterX=0 CenterY=0 CenterZ=0 NormalX=0 NormalY=0 NormalZ=1 AngleXU=0 Radius=5.8
  constraints (2):
    c: Diameter(g0) = 11.6
    c: Coincident(g0,g-1)
FEATURE [Sketcher::SketchObject] Sketch070  label="cilindro maggiore"
  ArcFitTolerance = 1e-06
  AttachmentSupport = -> [XZ_Plane004]
  ExternalGeometry = -> [Sketch069]
  FullyConstrained = true
  MakeInternals = false
  MapMode = 5
  Placement = pos=(0,0,0) rot=(1,0,0;1.5708rad)
  sketch-geometry (1):
    g0: Circle CenterX=0 CenterY=0 CenterZ=0 NormalX=0 NormalY=0 NormalZ=1 AngleXU=0 Radius=6.5
  constraints (2):
    c: Coincident(g0,g-1)
    c: Diameter(g0) = 13
FEATURE [Sketcher::SketchObject] Sketch071  label="buco interno"
  ArcFitTolerance = 1e-06
  AttachmentSupport = -> [XZ_Plane004]
  ExternalGeometry = -> [Sketch069]
  FullyConstrained = true
  MakeInternals = false
  MapMode = 5
  Placement = pos=(0,0,0) rot=(1,0,0;1.5708rad)
  sketch-geometry (1):
    g0: Circle CenterX=0 CenterY=0 CenterZ=0 NormalX=0 NormalY=0 NormalZ=1 AngleXU=0 Radius=5
  constraints (2):
    c: Coincident(g0,g-1)
    c: Diameter(g0) = 10
FEATURE [PartDesign::Pad] Pad
  Direction = (0,-1,2e-16)
  Length = 1.2
  Length2 = 10
  Placement = pos=(0,0,0) rot=(1,0,0;1.5708rad)
  Profile = -> Sketch070
  ReferenceAxis = -> Sketch070 [N_Axis]
  Refine = true
  Suppressed = false
  Type = 0
FEATURE [PartDesign::Pad] Pad001
  BaseFeature = -> Pad
  Direction = (0,-1,2e-16)
  Length = 5.6
  Length2 = 10
  Placement = pos=(0,0,0) rot=(1,0,0;1.5708rad)
  Profile = -> Sketch069
  ReferenceAxis = -> Sketch069 [N_Axis]
  Refine = true
  Suppressed = false
  Type = 0
FEATURE [PartDesign::Pocket] Pocket
  BaseFeature = -> Pad001
  Direction = (0,1,-2e-16)
  Length = 7
  Length2 = 5
  Midplane = true
  Placement = pos=(0,0,0) rot=(1,0,0;1.5708rad)
  Profile = -> Sketch071
  ReferenceAxis = -> Sketch071 [N_Axis]
  Refine = true
  Suppressed = false
  Type = 0
FEATURE [PartDesign::Fillet] Fillet
  Base = -> Pocket [Face7]
  BaseFeature = -> Pocket
  Placement = pos=(0,0,0) rot=(1,0,0;1.5708rad)
  Radius = 1
  Refine = true
  SupportTransform = false
  Suppressed = false
  UseAllEdges = false
FEATURE [PartDesign::Body] Body004  label="pulsanti lato sinistro"
  AllowCompound = false
  Group = -> [Sketch069,Sketch070,Sketch071,Pad,Pad001,Pocket,Fillet]
  Origin = -> Origin004
  Tip = -> Fillet
FEATURE [Sketcher::SketchObject] Sketch072  label="buco per saldature e diodo driver solenoide"
  ArcFitTolerance = 1e-06
  AttachmentSupport = -> [XZ_Plane]
  ExternalGeometry = -> [Sketch038]
  FullyConstrained = true
  MakeInternals = false
  MapMode = 5
  Placement = pos=(0,0,0) rot=(1,0,0;1.5708rad)
  sketch-geometry (4):
    g0: LineSegment StartX=-212.269 StartY=-43.9083 StartZ=0 EndX=-207.197 EndY=-33.0326 EndZ=0
    g1: LineSegment StartX=-207.197 StartY=-33.0326 StartZ=0 EndX=-207.56 EndY=-32.8635 EndZ=0
    g2: LineSegment StartX=-207.56 StartY=-32.8635 StartZ=0 EndX=-212.631 EndY=-43.7392 EndZ=0
    g3: LineSegment StartX=-212.631 StartY=-43.7392 StartZ=0 EndX=-212.269 EndY=-43.9083 EndZ=0
  constraints (11):
    c: Coincident(g1,g0)
    c: Coincident(g2,g1)
    c: Coincident(g3,g2)
    c: Coincident(g3,g0)
    c: Parallel(g-3,g0)
    c: Parallel(g0,g2)
    c: Perpendicular(g0,g3)
    c: Perpendicular(g1,g0)
    c: Distance(g3) = 0.4
    c: Distance(g2) = 12
    c: Coincident(g0,g-3)
FEATURE [Part::Extrusion] Extrude074  label="Extrude buco per saldature e diodo driver solenoide"
  Base = -> Sketch072
  Dir = (0,-1,2e-16)
  DirMode = 2
  FaceMakerClass = Part::FaceMakerBullseye
  FaceMakerMode = 3
  LengthFwd = 14.6
  LengthRev = 0
  Solid = true
  Symmetric = true
FEATURE [Part::Cut] Cut042
  Base = -> Cut041
  Refine = true
  Tool = -> Extrude074
FEATURE [Sketcher::SketchObject] Sketch073  label="fori slargati blocco solenoide"
  ArcFitTolerance = 1e-06
  AttachmentSupport = -> [XY_Plane]
  ExternalGeometry = -> [Sketch030]
  FullyConstrained = true
  MakeInternals = false
  MapMode = 5
  sketch-geometry (2):
    g0: Circle CenterX=-152.209 CenterY=6.95 CenterZ=0 NormalX=0 NormalY=0 NormalZ=1 AngleXU=0 Radius=3.7
    g1: Circle CenterX=-130.41 CenterY=-6.95 CenterZ=0 NormalX=0 NormalY=0 NormalZ=1 AngleXU=0 Radius=3.7
  constraints (4):
    c: Diameter(g0) = 7.4
    c: Coincident(g0,g-3)
    c: Diameter(g1) = 7.4
    c: Coincident(g1,g-4)
FEATURE [Part::Extrusion] Extrude075  label="Extrude fori slargati blocco solenoide"
  Base = -> Sketch073
  Dir = (0,0,1)
  DirMode = 2
  FaceMakerClass = Part::FaceMakerBullseye
  FaceMakerMode = 3
  LengthFwd = 1.5
  LengthRev = 0
  Placement = pos=(0,0,36.4) rot=(0,0,1;0rad)
  Solid = true
  Symmetric = false
FEATURE [Part::Cut] Cut043
  Base = -> Cut042
  Refine = true
  Tool = -> Extrude075
FEATURE [Sketcher::SketchObject] Sketch074  label="lato sx pistola"
  ArcFitTolerance = 1e-06
  AttachmentSupport = -> [XZ_Plane]
  ExternalGeometry = -> [Sketch016,Sketch,Sketch058]
  FullyConstrained = true
  MakeInternals = false
  MapMode = 5
  Placement = pos=(0,0,0) rot=(1,0,0;1.5708rad)
  sketch-geometry (37):
    g0: LineSegment StartX=-82.8 StartY=3.2 StartZ=0 EndX=0 EndY=3.2 EndZ=0
    g1: LineSegment StartX=-82.8 StartY=3.2 StartZ=0 EndX=-82.8 EndY=6.2 EndZ=0
    g2: LineSegment [constr] StartX=-107.6 StartY=18 StartZ=0 EndX=-107.6 EndY=20 EndZ=0
    g3: LineSegment [constr] StartX=-132.428 StartY=18 StartZ=0 EndX=-132.428 EndY=20 EndZ=0
    g4: LineSegment StartX=-132.428 StartY=20 StartZ=0 EndX=-107.6 EndY=20 EndZ=0
    g5: ArcOfCircle CenterX=-107.6 CenterY=4 CenterZ=0 NormalX=0 NormalY=0 NormalZ=1 AngleXU=0 Radius=16 StartAngle=0.137937 EndAngle=1.5708
    g6: LineSegment StartX=-82.8 StartY=6.2 StartZ=0 EndX=-91.752 EndY=6.2 EndZ=0
    g7: LineSegment [constr] StartX=-145.743 StartY=8.32624 StartZ=0 EndX=-147.645 EndY=8.94427 EndZ=0
    g8: ArcOfCircle CenterX=-132.428 CenterY=4 CenterZ=0 NormalX=0 NormalY=0 NormalZ=1 AngleXU=0 Radius=16 StartAngle=1.5708 EndAngle=2.82743
    g9: LineSegment StartX=-215.932 StartY=-80.4316 StartZ=0 EndX=-176.685 EndY=-80.4316 EndZ=0
    g10: LineSegment StartX=-147.645 StartY=8.94427 StartZ=0 EndX=-176.685 EndY=-80.4316 EndZ=0
    g11: LineSegment [constr] StartX=-193.988 StartY=-2.33927 StartZ=0 EndX=-192.176 EndY=-3.18451 EndZ=0
    g12: LineSegment [constr] StartX=-217.232 StartY=-52.1862 StartZ=0 EndX=-215.42 EndY=-53.0314 EndZ=0
    g13: LineSegment StartX=-192.176 StartY=-3.18451 StartZ=0 EndX=-215.42 EndY=-53.0314 EndZ=0
    g14: ArcOfCircle CenterX=-184.801 CenterY=-67.3089 CenterZ=0 NormalX=0 NormalY=0 NormalZ=1 AngleXU=0 Radius=33.7833 StartAngle=2.70526 EndAngle=3.54053
    g15: ArcOfCircle CenterX=-207.583 CenterY=4 CenterZ=0 NormalX=0 NormalY=0 NormalZ=1 AngleXU=0 Radius=17 StartAngle=5.84685 EndAngle=7.56663
    g16: LineSegment StartX=-202.765 StartY=20.303 StartZ=0 EndX=-195.887 EndY=39.2 EndZ=0
    g17: LineSegment [constr] StartX=-193.885 StartY=33.0037 StartZ=0 EndX=-197.644 EndY=34.3718 EndZ=0
    g18: LineSegment StartX=-195.887 StartY=39.2 StartZ=0 EndX=0 EndY=39.2 EndZ=0
    g19: LineSegment StartX=0 StartY=3.2 StartZ=0 EndX=0 EndY=39.2 EndZ=0
    g20: LineSegment StartX=-189.939 StartY=31.5672 StartZ=0 EndX=-192.333 EndY=24.9893 EndZ=0
    g21: LineSegment StartX=-196.467 StartY=26.4942 StartZ=0 EndX=-194.073 EndY=33.0721 EndZ=0
    g22: Circle CenterX=-213.443 CenterY=-76.8316 CenterZ=0 NormalX=0 NormalY=0 NormalZ=1 AngleXU=0 Radius=1.8
    g23: Circle CenterX=-179.305 CenterY=-76.8316 CenterZ=0 NormalX=0 NormalY=0 NormalZ=1 AngleXU=0 Radius=1.8
    g24: Circle CenterX=-184.08 CenterY=34.8 CenterZ=0 NormalX=0 NormalY=0 NormalZ=1 AngleXU=0 Radius=1.8
    g25: Circle CenterX=-78.51 CenterY=34.8 CenterZ=0 NormalX=0 NormalY=0 NormalZ=1 AngleXU=0 Radius=1.8
    g26: Circle CenterX=-78.51 CenterY=7.6 CenterZ=0 NormalX=0 NormalY=0 NormalZ=1 AngleXU=0 Radius=1.8
    g27: Circle CenterX=-5.6 CenterY=34.8 CenterZ=0 NormalX=0 NormalY=0 NormalZ=1 AngleXU=0 Radius=1.8
    g28: Circle CenterX=-5.6 CenterY=7.6 CenterZ=0 NormalX=0 NormalY=0 NormalZ=1 AngleXU=0 Radius=1.8
    g29: LineSegment StartX=-190.127 StartY=31.6356 StartZ=0 EndX=-189.939 EndY=31.5672 EndZ=0
    g30: LineSegment StartX=-194.073 StartY=33.0721 StartZ=0 EndX=-193.885 EndY=33.0037 EndZ=0
    g31: LineSegment StartX=-193.885 StartY=33.0037 StartZ=0 EndX=-190.127 EndY=31.6356 EndZ=0
    g32: LineSegment StartX=-196.467 StartY=26.4942 StartZ=0 EndX=-192.333 EndY=24.9893 EndZ=0
    g33: Circle CenterX=-19 CenterY=21.2 CenterZ=0 NormalX=0 NormalY=0 NormalZ=1 AngleXU=0 Radius=6.3
    g34: Circle CenterX=-42 CenterY=21.2 CenterZ=0 NormalX=0 NormalY=0 NormalZ=1 AngleXU=0 Radius=6.3
    g35: Circle CenterX=-65 CenterY=21.2 CenterZ=0 NormalX=0 NormalY=0 NormalZ=1 AngleXU=0 Radius=6.3
    g36: LineSegment [constr] StartX=-4 StartY=21.2 StartZ=0 EndX=-65 EndY=21.2 EndZ=0
  constraints (96):
    c: Coincident(g0,g-41)
    c: Horizontal(g0)
    c: PointOnObject(g0,g-39)
    c: Coincident(g1,g0)
    c: Vertical(g1)
    c: DistanceY(g1,g1) = 3
    c: Coincident(g2,g-17)
    c: Vertical(g2)
    c: Coincident(g3,g-16)
    c: Vertical(g3)
    c: DistanceY(g2,g2) = 2
    c: DistanceY(g3,g3) = 2
    c: Coincident(g4,g3)
    c: Coincident(g4,g2)
    c: Coincident(g5,g-17)
    c: Coincident(g5,g2)
    c: Coincident(g6,g1)
    c: Horizontal(g6)
    c: Coincident(g6,g5)
    c: Coincident(g7,g-15)
    c: Coincident(g8,g7)
    c: Coincident(g8,g3)
    c: Coincident(g8,g-15)
    c: Horizontal(g9)
    c: DistanceY(g-13,g9) = 2
    c: Coincident(g10,g7)
    c: Parallel(g10,g-14)
    c: Coincident(g9,g10)
    c: Distance(g11) = 2
    c: Coincident(g11,g-11)
    c: Perpendicular(g-11,g11)
    c: Distance(g12) = 2
    c: Coincident(g12,g-12)
    c: Perpendicular(g-11,g12)
    c: Coincident(g13,g11)
    c: Coincident(g13,g12)
    c: Coincident(g14,g-32)
    c: Coincident(g14,g12)
    c: Coincident(g14,g9)
    c: Coincident(g15,g-10)
    c: Coincident(g15,g11)
    c: Parallel(g16,g-22)
    c: Distance(g17) = 4
    c: PointOnObject(g17,g16)
    c: Coincident(g15,g16)
    c: Horizontal(g18)
    c: Coincident(g18,g16)
    c: Coincident(g19,g0)
    c: PointOnObject(g19,g-39)
    c: DistanceY(g19,g-36) = 2
    c: Coincident(g18,g19)
    c: Diameter(g22) = 3.6
    c: Coincident(g22,g-9)
    c: Diameter(g23) = 3.6
    c: Coincident(g23,g-8)
    c: Diameter(g24) = 3.6
    c: Diameter(g25) = 3.6
    c: Diameter(g26) = 3.6
    c: Diameter(g27) = 3.6
    c: Diameter(g28) = 3.6
    c: Coincident(g27,g-4)
    c: Coincident(g28,g-3)
    c: Coincident(g25,g-6)
    c: Coincident(g26,g-5)
    c: Coincident(g24,g-7)
    c: Parallel(g20,g-21)
    c: Equal(g20,g-21)
    c: Parallel(g21,g-19)
    c: Equal(g21,g-19)
    c: Distance(g29) = 0.2
    c: Distance(g30) = 0.2
    c: Parallel(g29,g-20)
    c: Parallel(g31,g-20)
    c: Equal(g31,g-20)
    c: Coincident(g30,g31)
    c: Coincident(g31,g29)
    c: Coincident(g29,g-21)
    c: Parallel(g30,g31)
    c: Coincident(g17,g30)
    c: Coincident(g20,g29)
    c: Coincident(g21,g30)
    c: Perpendicular(g16,g17)
    c: Coincident(g32,g21)
    c: Coincident(g32,g20)
    c: Perpendicular(g10,g7)
    c: Diameter(g33) = 12.6
    c: Diameter(g34) = 12.6
    c: Diameter(g35) = 12.6
    c: Horizontal(g36)
    c: PointOnObject(g33,g36)
    c: PointOnObject(g34,g36)
    c: DistanceX(g34,g33) = 23
    c: DistanceX(g35,g34) = 23
    c: DistanceX(g33,g36) = 15
    c: Symmetric(g-24,g-24,g36)
    c: Coincident(g36,g35)
FEATURE [Sketcher::SketchObject] Sketch075  label="lato dx pistola"
  ArcFitTolerance = 1e-06
  AttachmentSupport = -> [XZ_Plane]
  ExternalGeometry = -> [Sketch016,Sketch,Sketch058,Sketch074]
  FullyConstrained = true
  MakeInternals = false
  MapMode = 5
  Placement = pos=(0,0,0) rot=(1,0,0;1.5708rad)
  sketch-geometry (61):
    g0: LineSegment StartX=-82.8 StartY=3.2 StartZ=0 EndX=0 EndY=3.2 EndZ=0
    g1: LineSegment StartX=-82.8 StartY=3.2 StartZ=0 EndX=-82.8 EndY=6.2 EndZ=0
    g2: LineSegment [constr] StartX=-107.6 StartY=18 StartZ=0 EndX=-107.6 EndY=20 EndZ=0
    g3: LineSegment [constr] StartX=-132.428 StartY=18 StartZ=0 EndX=-132.428 EndY=20 EndZ=0
    g4: LineSegment StartX=-132.428 StartY=20 StartZ=0 EndX=-107.6 EndY=20 EndZ=0
    g5: ArcOfCircle CenterX=-107.6 CenterY=4 CenterZ=0 NormalX=0 NormalY=0 NormalZ=1 AngleXU=0 Radius=16 StartAngle=0.137937 EndAngle=1.5708
    g6: LineSegment StartX=-82.8 StartY=6.2 StartZ=0 EndX=-91.752 EndY=6.2 EndZ=0
    g7: LineSegment [constr] StartX=-145.743 StartY=8.32624 StartZ=0 EndX=-147.645 EndY=8.94427 EndZ=0
    g8: ArcOfCircle CenterX=-132.428 CenterY=4 CenterZ=0 NormalX=0 NormalY=0 NormalZ=1 AngleXU=0 Radius=16 StartAngle=1.5708 EndAngle=2.82743
    g9: LineSegment StartX=-215.932 StartY=-80.4316 StartZ=0 EndX=-176.685 EndY=-80.4316 EndZ=0
    g10: LineSegment StartX=-147.645 StartY=8.94427 StartZ=0 EndX=-176.685 EndY=-80.4316 EndZ=0
    g11: LineSegment [constr] StartX=-193.988 StartY=-2.33927 StartZ=0 EndX=-192.176 EndY=-3.18451 EndZ=0
    g12: LineSegment [constr] StartX=-217.232 StartY=-52.1862 StartZ=0 EndX=-215.42 EndY=-53.0314 EndZ=0
    g13: LineSegment StartX=-192.176 StartY=-3.18451 StartZ=0 EndX=-215.42 EndY=-53.0314 EndZ=0
    g14: ArcOfCircle CenterX=-184.801 CenterY=-67.3089 CenterZ=0 NormalX=0 NormalY=0 NormalZ=1 AngleXU=0 Radius=33.7833 StartAngle=2.70526 EndAngle=3.54053
    g15: ArcOfCircle CenterX=-207.583 CenterY=4 CenterZ=0 NormalX=0 NormalY=0 NormalZ=1 AngleXU=0 Radius=17 StartAngle=5.84685 EndAngle=7.56663
    g16: LineSegment StartX=-202.765 StartY=20.303 StartZ=0 EndX=-195.887 EndY=39.2 EndZ=0
    g17: LineSegment [constr] StartX=-193.885 StartY=33.0037 StartZ=0 EndX=-197.644 EndY=34.3718 EndZ=0
    g18: LineSegment StartX=-195.887 StartY=39.2 StartZ=0 EndX=0 EndY=39.2 EndZ=0
    g19: LineSegment StartX=0 StartY=3.2 StartZ=0 EndX=0 EndY=39.2 EndZ=0
    g20: LineSegment StartX=-189.939 StartY=31.5672 StartZ=0 EndX=-192.333 EndY=24.9893 EndZ=0
    g21: LineSegment StartX=-196.467 StartY=26.4942 StartZ=0 EndX=-194.073 EndY=33.0721 EndZ=0
    g22: Circle CenterX=-213.443 CenterY=-76.8316 CenterZ=0 NormalX=0 NormalY=0 NormalZ=1 AngleXU=0 Radius=1.8
    g23: Circle CenterX=-179.305 CenterY=-76.8316 CenterZ=0 NormalX=0 NormalY=0 NormalZ=1 AngleXU=0 Radius=1.8
    g24: Circle CenterX=-184.08 CenterY=34.8 CenterZ=0 NormalX=0 NormalY=0 NormalZ=1 AngleXU=0 Radius=1.8
    g25: Circle CenterX=-78.51 CenterY=34.8 CenterZ=0 NormalX=0 NormalY=0 NormalZ=1 AngleXU=0 Radius=1.8
    g26: Circle CenterX=-78.51 CenterY=7.6 CenterZ=0 NormalX=0 NormalY=0 NormalZ=1 AngleXU=0 Radius=1.8
    g27: Circle CenterX=-5.6 CenterY=34.8 CenterZ=0 NormalX=0 NormalY=0 NormalZ=1 AngleXU=0 Radius=1.8
    g28: Circle CenterX=-5.6 CenterY=7.6 CenterZ=0 NormalX=0 NormalY=0 NormalZ=1 AngleXU=0 Radius=1.8
    g29: LineSegment StartX=-190.127 StartY=31.6356 StartZ=0 EndX=-189.939 EndY=31.5672 EndZ=0
    g30: LineSegment StartX=-194.073 StartY=33.0721 StartZ=0 EndX=-193.885 EndY=33.0037 EndZ=0
    g31: LineSegment StartX=-193.885 StartY=33.0037 StartZ=0 EndX=-190.127 EndY=31.6356 EndZ=0
    g32: LineSegment StartX=-196.467 StartY=26.4942 StartZ=0 EndX=-192.333 EndY=24.9893 EndZ=0
    g33: LineSegment [constr] StartX=-4 StartY=21.2 StartZ=0 EndX=-87.91 EndY=21.2 EndZ=0
    g34: GeomPoint [constr] X=-4 Y=21.2 Z=0
    g35: LineSegment [constr] StartX=-15.2 StartY=33.7 StartZ=0 EndX=-15.2 EndY=8.7 EndZ=0
    g36: LineSegment [constr] StartX=-15.2 StartY=33.7 StartZ=0 EndX=-56.2 EndY=33.7 EndZ=0
    g37: LineSegment [constr] StartX=-15.2 StartY=8.7 StartZ=0 EndX=-56.2 EndY=8.7 EndZ=0
    g38: LineSegment [constr] StartX=-56.2 StartY=33.7 StartZ=0 EndX=-56.2 EndY=8.7 EndZ=0
    g39: Circle CenterX=-18.6 CenterY=30.3 CenterZ=0 NormalX=0 NormalY=0 NormalZ=1 AngleXU=0 Radius=3.4
    g40: Circle CenterX=-18.6 CenterY=12.1 CenterZ=0 NormalX=0 NormalY=0 NormalZ=1 AngleXU=0 Radius=3.4
    g41: Circle CenterX=-43.2 CenterY=30.3 CenterZ=0 NormalX=0 NormalY=0 NormalZ=1 AngleXU=0 Radius=3.4
    g42: Circle CenterX=-43.2 CenterY=12.1 CenterZ=0 NormalX=0 NormalY=0 NormalZ=1 AngleXU=0 Radius=3.4
    g43: LineSegment [constr] StartX=-4 StartY=21.2 StartZ=0 EndX=-15.2 EndY=21.2 EndZ=0
    g44: LineSegment [constr] StartX=-15.2 StartY=21.2 StartZ=0 EndX=-36.2 EndY=21.2 EndZ=0
    g45: LineSegment [constr] StartX=-41.5 StartY=16.2 StartZ=0 EndX=-30.9 EndY=16.2 EndZ=0
    g46: LineSegment [constr] StartX=-30.9 StartY=16.2 StartZ=0 EndX=-30.9 EndY=26.2 EndZ=0
    g47: LineSegment [constr] StartX=-30.9 StartY=26.2 StartZ=0 EndX=-41.5 EndY=26.2 EndZ=0
    g48: LineSegment [constr] StartX=-41.5 StartY=26.2 StartZ=0 EndX=-41.5 EndY=16.2 EndZ=0
    g49: GeomPoint [constr] X=-36.2 Y=21.2 Z=0
    g50: Circle CenterX=-36.2 CenterY=21.2 CenterZ=0 NormalX=0 NormalY=0 NormalZ=1 AngleXU=0 Radius=2.8
    g51: LineSegment [constr] StartX=-24.2 StartY=26.7 StartZ=0 EndX=-24.2 EndY=15.7 EndZ=0
    g52: Circle CenterX=-24.2 CenterY=26.7 CenterZ=0 NormalX=0 NormalY=0 NormalZ=1 AngleXU=0 Radius=3
    g53: Circle CenterX=-24.2 CenterY=15.7 CenterZ=0 NormalX=0 NormalY=0 NormalZ=1 AngleXU=0 Radius=3
    g54: GeomPoint X=-18.6 Y=30.3 Z=0
    g55: GeomPoint X=-18.6 Y=12.1 Z=0
    g56: GeomPoint X=-43.2 Y=12.1 Z=0
    g57: GeomPoint X=-43.2 Y=30.3 Z=0
    g58: Circle CenterX=-65 CenterY=21.2 CenterZ=0 NormalX=0 NormalY=0 NormalZ=1 AngleXU=0 Radius=1.5
    g59: Circle CenterX=-42 CenterY=21.2 CenterZ=0 NormalX=0 NormalY=0 NormalZ=1 AngleXU=0 Radius=1.5
    g60: Circle CenterX=-19 CenterY=21.2 CenterZ=0 NormalX=0 NormalY=0 NormalZ=1 AngleXU=0 Radius=1.5
  constraints (149):
    c: Coincident(g0,g-41)
    c: Horizontal(g0)
    c: PointOnObject(g0,g-39)
    c: Coincident(g1,g0)
    c: Vertical(g1)
    c: DistanceY(g1,g1) = 3
    c: Coincident(g2,g-17)
    c: Vertical(g2)
    c: Coincident(g3,g-16)
    c: Vertical(g3)
    c: DistanceY(g2,g2) = 2
    c: DistanceY(g3,g3) = 2
    c: Coincident(g4,g3)
    c: Coincident(g4,g2)
    c: Coincident(g5,g-17)
    c: Coincident(g5,g2)
    c: Coincident(g6,g1)
    c: Horizontal(g6)
    c: Coincident(g6,g5)
    c: Coincident(g7,g-15)
    c: Coincident(g8,g7)
    c: Coincident(g8,g3)
    c: Coincident(g8,g-15)
    c: Horizontal(g9)
    c: DistanceY(g-13,g9) = 2
    c: Coincident(g10,g7)
    c: Parallel(g10,g-14)
    c: Coincident(g9,g10)
    c: Distance(g11) = 2
    c: Coincident(g11,g-11)
    c: Perpendicular(g-11,g11)
    c: Distance(g12) = 2
    c: Coincident(g12,g-12)
    c: Perpendicular(g-11,g12)
    c: Coincident(g13,g11)
    c: Coincident(g13,g12)
    c: Coincident(g14,g-32)
    c: Coincident(g14,g12)
    c: Coincident(g14,g9)
    c: Coincident(g15,g-10)
    c: Coincident(g15,g11)
    c: Parallel(g16,g-22)
    c: Distance(g17) = 4
    c: PointOnObject(g17,g16)
    c: Coincident(g15,g16)
    c: Horizontal(g18)
    c: Coincident(g18,g16)
    c: Coincident(g19,g0)
    c: PointOnObject(g19,g-39)
    c: DistanceY(g19,g-36) = 2
    c: Coincident(g18,g19)
    c: Diameter(g22) = 3.6
    c: Coincident(g22,g-9)
    c: Diameter(g23) = 3.6
    c: Coincident(g23,g-8)
    c: Diameter(g24) = 3.6
    c: Diameter(g25) = 3.6
    c: Diameter(g26) = 3.6
    c: Diameter(g27) = 3.6
    c: Diameter(g28) = 3.6
    c: Coincident(g27,g-4)
    c: Coincident(g28,g-3)
    c: Coincident(g25,g-6)
    c: Coincident(g26,g-5)
    c: Coincident(g24,g-7)
    c: Parallel(g20,g-21)
    c: Equal(g20,g-21)
    c: Parallel(g21,g-19)
    c: Equal(g21,g-19)
    c: Distance(g29) = 0.2
    c: Distance(g30) = 0.2
    c: Parallel(g29,g-20)
    c: Parallel(g31,g-20)
    c: Equal(g31,g-20)
    c: Coincident(g30,g31)
    c: Coincident(g31,g29)
    c: Coincident(g29,g-21)
    c: Parallel(g30,g31)
    c: Coincident(g17,g30)
    c: Coincident(g20,g29)
    c: Coincident(g21,g30)
    c: Perpendicular(g16,g17)
    c: Coincident(g32,g21)
    c: Coincident(g32,g20)
    c: Perpendicular(g10,g7)
    c: Horizontal(g33)
    c: Symmetric(g-24,g-24,g33)
    c: PointOnObject(g33,g-28)
    c: Symmetric(g-24,g-24,g34)
    c: DistanceY(g35,g35) = 25
    c: Symmetric(g35,g35,g33)
    c: Distance(g36) = 41
    c: Coincident(g36,g35)
    c: Horizontal(g36)
    c: Coincident(g37,g35)
    c: Horizontal(g37)
    c: Coincident(g38,g36)
    c: Vertical(g38)
    c: Coincident(g37,g38)
    c: Diameter(g39) = 6.8
    c: Diameter(g40) = 6.8
    c: Tangent(g39,g36)
    c: Tangent(g40,g37)
    c: Tangent(g39,g35)
    c: Tangent(g40,g35)
    c: Diameter(g41) = 6.8
    c: Diameter(g42) = 6.8
    c: Tangent(g41,g36)
    c: Tangent(g42,g37)
    c: DistanceX(g41,g39) = 24.6
    c: DistanceX(g42,g40) = 24.6
    c: Distance(g43) = 11.2
    c: Coincident(g43,g33)
    c: PointOnObject(g43,g33)
    c: PointOnObject(g43,g35)
    c: Distance(g44) = 21
    c: Coincident(g44,g43)
    c: PointOnObject(g44,g33)
    c: Coincident(g45,g46)
    c: Coincident(g46,g47)
    c: Coincident(g47,g48)
    c: Coincident(g48,g45)
    c: Horizontal(g45)
    c: Horizontal(g47)
    c: Vertical(g46)
    c: Vertical(g48)
    c: Symmetric(g47,g45,g49)
    c: Distance(g46,g48) = 10.6
    c: Distance(g45,g47) = 10
    c: Coincident(g49,g44)
    c: Diameter(g50) = 5.6
    c: Coincident(g50,g44)
    c: Distance(g51) = 11
    c: Symmetric(g51,g51,g33)
    c: DistanceX(g51,g43) = 9
    c: Diameter(g52) = 6
    c: Coincident(g52,g51)
    c: Diameter(g53) = 6
    c: Coincident(g53,g51)
    c: Coincident(g40,g55)
    c: Coincident(g39,g54)
    c: Coincident(g41,g57)
    c: Coincident(g42,g56)
    c: Diameter(g58) = 3
    c: Diameter(g59) = 3
    c: Diameter(g60) = 3
    c: Coincident(g58,g-44)
    c: Coincident(g59,g-46)
    c: Coincident(g60,g-45)
FEATURE [Sketcher::SketchObject] Sketch078
  ArcFitTolerance = 1e-06
  AttachmentSupport = -> [XZ_Plane005]
  FullyConstrained = true
  MakeInternals = false
  MapMode = 5
  Placement = pos=(0,0,0) rot=(1,0,0;1.5708rad)
  sketch-geometry (5):
    g0: LineSegment [constr] StartX=0 StartY=5.5 StartZ=0 EndX=0 EndY=-5.5 EndZ=0
    g1: ArcOfCircle CenterX=0 CenterY=5.5 CenterZ=0 NormalX=0 NormalY=0 NormalZ=1 AngleXU=0 Radius=2.7 StartAngle=0 EndAngle=3.14159
    g2: ArcOfCircle CenterX=0 CenterY=-5.5 CenterZ=0 NormalX=0 NormalY=0 NormalZ=1 AngleXU=0 Radius=2.7 StartAngle=3.1416 EndAngle=6.28318
    g3: LineSegment StartX=-2.7 StartY=5.5 StartZ=0 EndX=-2.7 EndY=-5.50001 EndZ=0
    g4: LineSegment StartX=2.7 StartY=5.5 StartZ=0 EndX=2.7 EndY=-5.50001 EndZ=0
  constraints (13):
    c: Distance(g0) = 11
    c: Vertical(g0)
    c: Symmetric(g0,g0,g-1)
    c: Radius(g1) = 2.7
    c: Coincident(g1,g0)
    c: Radius(g2) = 2.7
    c: Coincident(g2,g0)
    c: Vertical(g3)
    c: Vertical(g4)
    c: Coincident(g2,g4)
    c: Coincident(g2,g3)
    c: Tangent(g3,g1) = -1.5708
    c: Tangent(g4,g1) = 1.5708
FEATURE [PartDesign::Pad] Pad002
  Direction = (0,-1,2e-16)
  Length = 0.8
  Length2 = 10
  Placement = pos=(0,0,0) rot=(1,0,0;1.5708rad)
  Profile = -> Sketch078
  ReferenceAxis = -> Sketch078 [N_Axis]
  Refine = true
  Suppressed = false
  Type = 0
FEATURE [Sketcher::SketchObject] Sketch079
  ArcFitTolerance = 1e-06
  AttachmentSupport = -> [XZ_Plane005]
  ExternalGeometry = -> [Sketch078]
  FullyConstrained = true
  MakeInternals = false
  MapMode = 5
  Placement = pos=(0,0,0) rot=(1,0,0;1.5708rad)
  sketch-geometry (2):
    g0: Circle CenterX=-1e-16 CenterY=5.5 CenterZ=0 NormalX=0 NormalY=0 NormalZ=1 AngleXU=0 Radius=2.7
    g1: Circle CenterX=0 CenterY=-5.5 CenterZ=0 NormalX=0 NormalY=0 NormalZ=1 AngleXU=0 Radius=2.7
  constraints (4):
    c: Coincident(g0,g-3)
    c: PointOnObject(g-3,g0)
    c: Coincident(g1,g-4)
    c: Equal(g1,g-4)
FEATURE [PartDesign::Pad] Pad003
  BaseFeature = -> Pad002
  Direction = (0,-1,2e-16)
  Length = 5
  Length2 = 10
  Placement = pos=(0,0,0) rot=(1,0,0;1.5708rad)
  Profile = -> Sketch079
  ReferenceAxis = -> Sketch079 [N_Axis]
  Refine = true
  Suppressed = false
  Type = 0
FEATURE [PartDesign::Fillet] Fillet001
  Base = -> Pad003 [Edge16,Edge14]
  BaseFeature = -> Pad003
  Placement = pos=(0,0,0) rot=(1,0,0;1.5708rad)
  Radius = 0.4
  Refine = true
  SupportTransform = false
  Suppressed = false
  UseAllEdges = false
FEATURE [PartDesign::Body] Body005  label="pulsanti lato destro"
  AllowCompound = false
  Group = -> [Sketch078,Pad002,Sketch079,Pad003,Fillet001]
  Origin = -> Origin005
  Tip = -> Fillet001
FEATURE [PartDesign::SubShapeBinder] Binder
  BindCopyOnChange = 0
  BindMode = 0
  ClaimChildren = false
  Context = -> Body006 [Binder.]
  Fuse = false
  MakeFace = true
  OffsetFill = false
  OffsetIntersection = false
  OffsetJoinType = 0
  OffsetOpenResult = false
  PartialLoad = false
  Refine = true
  Relative = true
  Support = -> [Body[Sketch074.]]
  _Version = 2
FEATURE [PartDesign::SubShapeBinder] Binder001
  BindCopyOnChange = 0
  BindMode = 0
  ClaimChildren = false
  Context = -> Body007 [Binder001.]
  Fuse = false
  MakeFace = true
  OffsetFill = false
  OffsetIntersection = false
  OffsetJoinType = 0
  OffsetOpenResult = false
  PartialLoad = false
  Refine = true
  Relative = true
  Support = -> [Body[Sketch075.]]
  _Version = 2
FEATURE [Mesh::Feature] logo_per_PCB_definitivo_positivo
  Placement = pos=(-191,17,-66) rot=(0,1,1;0rad)
FEATURE [Sketcher::SketchObject] Sketch114  label="Sketch114 - base lato DX"
  ArcFitTolerance = 1e-06
  AttachmentSupport = -> [Binder001]
  ExternalGeometry = -> [Binder001]
  FullyConstrained = true
  MakeInternals = false
  MapMode = 5
  Placement = pos=(0,1e-15,0) rot=(0,0.707107,0.707107;3.14159rad)
  sketch-geometry (30):
    g0: Circle CenterX=5.6 CenterY=34.8 CenterZ=0 NormalX=0 NormalY=0 NormalZ=1 AngleXU=0 Radius=1.8
    g1: Circle CenterX=5.6 CenterY=7.6 CenterZ=0 NormalX=0 NormalY=0 NormalZ=1 AngleXU=0 Radius=1.8
    g2: Circle CenterX=24.2 CenterY=26.7 CenterZ=0 NormalX=0 NormalY=0 NormalZ=1 AngleXU=0 Radius=3
    g3: Circle CenterX=24.2 CenterY=15.7 CenterZ=0 NormalX=0 NormalY=0 NormalZ=1 AngleXU=0 Radius=3
    g4: Circle CenterX=36.2 CenterY=21.2 CenterZ=0 NormalX=0 NormalY=0 NormalZ=1 AngleXU=0 Radius=2.8
    g5: Circle CenterX=78.51 CenterY=34.8 CenterZ=0 NormalX=0 NormalY=0 NormalZ=1 AngleXU=0 Radius=1.8
    g6: Circle CenterX=78.51 CenterY=7.6 CenterZ=0 NormalX=0 NormalY=0 NormalZ=1 AngleXU=0 Radius=1.8
    g7: Circle CenterX=184.08 CenterY=34.8 CenterZ=0 NormalX=0 NormalY=0 NormalZ=1 AngleXU=0 Radius=1.8
    g8: Circle CenterX=213.443 CenterY=-76.8316 CenterZ=0 NormalX=0 NormalY=0 NormalZ=1 AngleXU=0 Radius=1.8
    g9: Circle CenterX=179.305 CenterY=-76.8316 CenterZ=0 NormalX=0 NormalY=0 NormalZ=1 AngleXU=0 Radius=1.8
    g10: ArcOfCircle [constr] CenterX=132.428 CenterY=4 CenterZ=0 NormalX=0 NormalY=0 NormalZ=1 AngleXU=0 Radius=16 StartAngle=0.314159 EndAngle=1.5708
    g11: ArcOfCircle CenterX=107.6 CenterY=4 CenterZ=0 NormalX=0 NormalY=0 NormalZ=1 AngleXU=0 Radius=16 StartAngle=1.5708 EndAngle=3.00366
    g12: ArcOfCircle CenterX=207.583 CenterY=4 CenterZ=0 NormalX=0 NormalY=0 NormalZ=1 AngleXU=0 Radius=17 StartAngle=1.85815 EndAngle=3.57792
    g13: ArcOfCircle CenterX=184.801 CenterY=-67.3089 CenterZ=0 NormalX=0 NormalY=0 NormalZ=1 AngleXU=0 Radius=33.7833 StartAngle=5.88425 EndAngle=6.71952
    g14: LineSegment StartX=0 StartY=39.2 StartZ=0 EndX=0 EndY=3.2 EndZ=0
    g15: LineSegment StartX=0 StartY=3.2 StartZ=0 EndX=82.8 EndY=3.2 EndZ=0
    g16: LineSegment StartX=82.8 StartY=3.2 StartZ=0 EndX=82.8 EndY=6.2 EndZ=0
    g17: LineSegment StartX=82.8 StartY=6.2 StartZ=0 EndX=91.752 EndY=6.2 EndZ=0
    g18: LineSegment StartX=107.6 StartY=20 StartZ=0 EndX=132.428 EndY=20 EndZ=0
    g19: LineSegment StartX=147.645 StartY=8.94427 StartZ=0 EndX=176.685 EndY=-80.4316 EndZ=0
    g20: LineSegment StartX=176.685 StartY=-80.4316 StartZ=0 EndX=215.932 EndY=-80.4316 EndZ=0
    g21: LineSegment StartX=215.42 StartY=-53.0314 StartZ=0 EndX=192.176 EndY=-3.18451 EndZ=0
    g22: LineSegment StartX=202.765 StartY=20.303 StartZ=0 EndX=195.887 EndY=39.2 EndZ=0
    g23: LineSegment StartX=195.887 StartY=39.2 StartZ=0 EndX=0 EndY=39.2 EndZ=0
    g24: LineSegment StartX=196.467 StartY=26.4942 StartZ=0 EndX=194.073 EndY=33.0721 EndZ=0
    g25: LineSegment StartX=194.073 StartY=33.0721 StartZ=0 EndX=189.939 EndY=31.5672 EndZ=0
    g26: LineSegment StartX=189.939 StartY=31.5672 StartZ=0 EndX=192.333 EndY=24.9893 EndZ=0
    g27: LineSegment StartX=192.333 StartY=24.9893 StartZ=0 EndX=196.467 EndY=26.4942 EndZ=0
    g28: LineSegment StartX=132.428 StartY=20 StartZ=0 EndX=144.053 EndY=20 EndZ=0
    g29: LineSegment StartX=144.053 StartY=20 StartZ=0 EndX=147.645 EndY=8.94427 EndZ=0
  constraints (65):
    c: Equal(g0,g-25)
    c: Equal(g2,g-29)
    c: Equal(g3,g-30)
    c: Equal(g4,g-28)
    c: Equal(g1,g-26)
    c: Coincident(g0,g-25)
    c: Coincident(g1,g-26)
    c: Coincident(g2,g-29)
    c: Coincident(g3,g-30)
    c: Coincident(g4,g-28)
    c: Equal(g5,g-23)
    c: Equal(g6,g-24)
    c: Coincident(g5,g-23)
    c: Coincident(g6,g-24)
    c: Equal(g7,g-20)
    c: Coincident(g7,g-20)
    c: Equal(g9,g-22)
    c: Coincident(g9,g-22)
    c: Equal(g8,g-21)
    c: Coincident(g8,g-21)
    c: Equal(g13,g-12)
    c: Equal(g12,g-14)
    c: Equal(g10,g-9)
    c: Equal(g11,g-7)
    c: Coincident(g14,g-27)
    c: Coincident(g14,g-27)
    c: Coincident(g15,g14)
    c: Coincident(g15,g-5)
    c: Coincident(g16,g15)
    c: Coincident(g16,g-6)
    c: Coincident(g17,g16)
    c: Coincident(g17,g-7)
    c: Coincident(g11,g17)
    c: Coincident(g11,g-8)
    c: Coincident(g18,g11)
    c: Coincident(g18,g-9)
    c: Coincident(g10,g18)
    c: Coincident(g10,g-10)
    c: Coincident(g19,g10)
    c: Coincident(g19,g-11)
    c: Coincident(g20,g19)
    c: Coincident(g20,g-12)
    c: Coincident(g13,g20)
    c: Coincident(g13,g-13)
    c: Coincident(g21,g13)
    c: Coincident(g21,g-14)
    c: Coincident(g12,g21)
    c: Coincident(g12,g-15)
    c: Coincident(g22,g12)
    c: Coincident(g22,g-15)
    c: Coincident(g23,g22)
    c: Coincident(g23,g14)
    c: Coincident(g24,g-18)
    c: Coincident(g24,g-16)
    c: Coincident(g25,g24)
    c: Coincident(g25,g-19)
    c: Coincident(g26,g25)
    c: Coincident(g26,g-19)
    c: Coincident(g27,g26)
    c: Coincident(g27,g24)
    c: Coincident(g29,g10)
    c: Coincident(g28,g10)
    c: Coincident(g29,g28)
    c: Parallel(g28,g18)
    c: Parallel(g29,g19)
FEATURE [PartDesign::Pad] Pad011
  Direction = (0,1,-2e-16)
  Length = 2
  Length2 = 10
  Profile = -> Sketch114
  ReferenceAxis = -> Sketch114 [N_Axis]
  Refine = true
  Reversed = true
  Suppressed = false
  Type = 0
FEATURE [Sketcher::SketchObject] Sketch115
  ArcFitTolerance = 1e-06
  AttachmentSupport = -> [Pad011]
  ExternalGeometry = -> [Binder001]
  FullyConstrained = true
  MakeInternals = false
  MapMode = 5
  Placement = pos=(0,1.7e-15,0) rot=(0,0.707107,0.707107;3.14159rad)
  sketch-geometry (4):
    g0: ArcOfCircle CenterX=24.2 CenterY=26.7 CenterZ=0 NormalX=0 NormalY=0 NormalZ=1 AngleXU=0 Radius=3 StartAngle=4.48384e-08 EndAngle=3.14159
    g1: ArcOfCircle CenterX=24.2 CenterY=15.7 CenterZ=0 NormalX=0 NormalY=0 NormalZ=1 AngleXU=0 Radius=3 StartAngle=3.14159 EndAngle=6.28318
    g2: LineSegment StartX=21.2 StartY=26.7 StartZ=0 EndX=21.2 EndY=15.7 EndZ=0
    g3: LineSegment StartX=27.2 StartY=26.7 StartZ=0 EndX=27.2 EndY=15.7 EndZ=0
  constraints (12):
    c: Equal(g1,g-4)
    c: Equal(g0,g-3)
    c: Coincident(g0,g-3)
    c: Coincident(g1,g-4)
    c: Vertical(g2)
    c: Vertical(g3)
    c: Tangent(g3,g-3)
    c: Tangent(g2,g-3)
    c: Coincident(g0,g2)
    c: Coincident(g0,g3)
    c: Coincident(g1,g2)
    c: Coincident(g3,g1)
FEATURE [Sketcher::SketchObject] Sketch117  label="Sketch117 - fori per inserto M3 x 3 x 4.5"
  ArcFitTolerance = 1e-06
  AttachmentSupport = -> [Pad011]
  ExternalGeometry = -> [Binder001]
  FullyConstrained = true
  MakeInternals = false
  MapMode = 5
  Placement = pos=(0,1.7e-15,0) rot=(0,0.707107,0.707107;3.14159rad)
  sketch-geometry (4):
    g0: Circle CenterX=43.2 CenterY=30.3 CenterZ=0 NormalX=0 NormalY=0 NormalZ=1 AngleXU=0 Radius=2.25
    g1: Circle CenterX=43.2 CenterY=12.1 CenterZ=0 NormalX=0 NormalY=0 NormalZ=1 AngleXU=0 Radius=2.25
    g2: Circle CenterX=18.6 CenterY=30.3 CenterZ=0 NormalX=0 NormalY=0 NormalZ=1 AngleXU=0 Radius=2.25
    g3: Circle CenterX=18.6 CenterY=12.1 CenterZ=0 NormalX=0 NormalY=0 NormalZ=1 AngleXU=0 Radius=2.25
  constraints (8):
    c: Diameter(g0) = 4.5
    c: Diameter(g1) = 4.5
    c: Diameter(g2) = 4.5
    c: Diameter(g3) = 4.5
    c: Coincident(g2,g-3)
    c: Coincident(g3,g-6)
    c: Coincident(g0,g-4)
    c: Coincident(g1,g-5)
FEATURE [Sketcher::SketchObject] Sketch118
  ArcFitTolerance = 1e-06
  AttachmentSupport = -> [Pad011]
  ExternalGeometry = -> [Binder001]
  FullyConstrained = true
  MakeInternals = false
  MapMode = 5
  Placement = pos=(0,-2,0) rot=(1,0,0;1.5708rad)
  sketch-geometry (12):
    g0: Circle CenterX=-78.51 CenterY=34.8 CenterZ=0 NormalX=0 NormalY=0 NormalZ=1 AngleXU=0 Radius=1.8
    g1: Circle CenterX=-78.51 CenterY=7.6 CenterZ=0 NormalX=0 NormalY=0 NormalZ=1 AngleXU=0 Radius=1.8
    g2: Circle CenterX=-5.6 CenterY=34.8 CenterZ=0 NormalX=0 NormalY=0 NormalZ=1 AngleXU=0 Radius=1.8
    g3: Circle CenterX=-5.6 CenterY=7.6 CenterZ=0 NormalX=0 NormalY=0 NormalZ=1 AngleXU=0 Radius=1.8
    g4: LineSegment StartX=0 StartY=39.2 StartZ=0 EndX=0 EndY=3.2 EndZ=0
    g5: LineSegment StartX=0 StartY=3.2 StartZ=0 EndX=-82.8 EndY=3.2 EndZ=0
    g6: LineSegment StartX=-82.8 StartY=3.2 StartZ=0 EndX=-82.8 EndY=39.2 EndZ=0
    g7: LineSegment StartX=-82.8 StartY=39.2 StartZ=0 EndX=0 EndY=39.2 EndZ=0
    g8: ArcOfCircle CenterX=-65 CenterY=21.2 CenterZ=0 NormalX=0 NormalY=0 NormalZ=1 AngleXU=0 Radius=10 StartAngle=1.5708 EndAngle=4.71239
    g9: ArcOfCircle CenterX=-19 CenterY=21.2 CenterZ=0 NormalX=0 NormalY=0 NormalZ=1 AngleXU=0 Radius=10 StartAngle=4.71239 EndAngle=7.85398
    g10: LineSegment StartX=-65 StartY=31.2 StartZ=0 EndX=-19 EndY=31.2 EndZ=0
    g11: LineSegment StartX=-65 StartY=11.2 StartZ=0 EndX=-19 EndY=11.2 EndZ=0
  constraints (25):
    c: Equal(g2,g-5)
    c: Equal(g3,g-7)
    c: Equal(g1,g-6)
    c: Equal(g0,g-4)
    c: Coincident(g0,g-4)
    c: Coincident(g1,g-6)
    c: Coincident(g3,g-7)
    c: Coincident(g2,g-5)
    c: Coincident(g4,g-8)
    c: Coincident(g4,g-9)
    c: Coincident(g5,g4)
    c: Coincident(g5,g-10)
    c: Coincident(g6,g5)
    c: PointOnObject(g6,g-3)
    c: Vertical(g6)
    c: Coincident(g7,g6)
    c: Coincident(g7,g4)
    c: Tangent(g8,g10) = 1.5708
    c: Tangent(g8,g11) = -1.5708
    c: Tangent(g9,g10) = 1.5708
    c: Tangent(g9,g11) = -1.5708
    c: Equal(g8,g9)
    c: Radius(g8) = 10
    c: Coincident(g8,g-11)
    c: Coincident(g9,g-12)
FEATURE [Sketcher::SketchObject] Sketch120
  ArcFitTolerance = 1e-06
  AttachmentSupport = -> [Pad011]
  ExternalGeometry = -> [Binder001]
  FullyConstrained = true
  MakeInternals = false
  MapMode = 5
  Placement = pos=(0,-2,0) rot=(1,0,0;1.5708rad)
  sketch-geometry (4):
    g0: LineSegment StartX=-137.815 StartY=39.2 StartZ=0 EndX=-142.655 EndY=24.303 EndZ=0
    g1: LineSegment StartX=-137.815 StartY=39.2 StartZ=0 EndX=-110.815 EndY=39.2 EndZ=0
    g2: LineSegment StartX=-142.655 StartY=24.303 StartZ=0 EndX=-110.815 EndY=24.303 EndZ=0
    g3: ArcOfCircle CenterX=-92.2534 CenterY=31.7515 CenterZ=0 NormalX=0 NormalY=0 NormalZ=1 AngleXU=0 Radius=20 StartAngle=2.75997 EndAngle=3.52321
  constraints (12):
    c: PointOnObject(g0,g-3)
    c: Coincident(g1,g0)
    c: PointOnObject(g1,g-3)
    c: Coincident(g2,g0)
    c: Horizontal(g2)
    c: Tangent(g0,g-4)
    c: Vertical(g2,g1)
    c: DistanceX(g1,g1) = 27
    c: DistanceY(g-6,g0) = 4
    c: Radius(g3) = 20
    c: Coincident(g3,g1)
    c: Coincident(g3,g2)
FEATURE [Sketcher::SketchObject] Sketch121
  ArcFitTolerance = 1e-06
  AttachmentSupport = -> [Pad011]
  ExternalGeometry = -> [Binder001]
  FullyConstrained = true
  MakeInternals = false
  MapMode = 5
  Placement = pos=(0,-2,0) rot=(1,0,0;1.5708rad)
  sketch-geometry (15):
    g0: LineSegment StartX=-137.815 StartY=39.2 StartZ=0 EndX=-143.955 EndY=20.303 EndZ=0
    g1: LineSegment StartX=-143.955 StartY=20.303 StartZ=0 EndX=-190.141 EndY=20.303 EndZ=0
    g2: LineSegment StartX=-190.141 StartY=20.303 StartZ=0 EndX=-186.139 EndY=31.3 EndZ=0
    g3: LineSegment StartX=-178.754 StartY=39.2 StartZ=0 EndX=-180.791 EndY=33.6029 EndZ=0
    g4: ArcOfCircle CenterX=-184.08 CenterY=34.8 CenterZ=0 NormalX=0 NormalY=0 NormalZ=1 AngleXU=0 Radius=3.5 StartAngle=4.71239 EndAngle=5.93412
    g5: LineSegment StartX=-184.08 StartY=31.3 StartZ=0 EndX=-186.139 EndY=31.3 EndZ=0
    g6: LineSegment StartX=-137.815 StartY=39.2 StartZ=0 EndX=-156.815 EndY=39.2 EndZ=0
    g7: LineSegment StartX=-168.815 StartY=39.2 StartZ=0 EndX=-178.754 EndY=39.2 EndZ=0
    g8: LineSegment StartX=-157.815 StartY=39.2 StartZ=0 EndX=-167.815 EndY=39.2 EndZ=0
    g9: LineSegment StartX=-168.815 StartY=31.2 StartZ=0 EndX=-156.815 EndY=31.2 EndZ=0
    g10: LineSegment StartX=-167.436 StartY=36.2 StartZ=0 EndX=-157.436 EndY=36.2 EndZ=0
    g11: ArcOfCircle CenterX=-176.411 CenterY=35.2 CenterZ=0 NormalX=0 NormalY=0 NormalZ=1 AngleXU=0 Radius=20 StartAngle=6.08183 EndAngle=6.48454
    g12: ArcOfCircle CenterX=-188.411 CenterY=35.2 CenterZ=0 NormalX=0 NormalY=0 NormalZ=1 AngleXU=0 Radius=20 StartAngle=6.08183 EndAngle=6.48454
    g13: ArcOfCircle CenterX=-177.411 CenterY=35.2 CenterZ=0 NormalX=0 NormalY=0 NormalZ=1 AngleXU=0 Radius=20 StartAngle=0.0500209 EndAngle=0.201358
    g14: ArcOfCircle CenterX=-187.411 CenterY=35.2 CenterZ=0 NormalX=0 NormalY=0 NormalZ=1 AngleXU=0 Radius=20 StartAngle=0.0500209 EndAngle=0.201358
  constraints (46):
    c: PointOnObject(g0,g-3)
    c: Tangent(g0,g-5)
    c: Coincident(g1,g0)
    c: Horizontal(g1)
    c: Coincident(g2,g1)
    c: PointOnObject(g3,g-3)
    c: Parallel(g3,g-6)
    c: Parallel(g2,g-6)
    c: Radius(g4) = 3.5
    c: Coincident(g4,g-7)
    c: Tangent(g3,g4) = 1.5708
    c: Horizontal(g5)
    c: Tangent(g5,g4) = 1.5708
    c: DistanceX(g-8,g5) = 3.8
    c: Coincident(g2,g5)
    c: Coincident(g6,g0)
    c: PointOnObject(g6,g-3)
    c: DistanceX(g6,g6) = 19
    c: PointOnObject(g7,g-3)
    c: DistanceX(g7,g6) = 12
    c: Coincident(g7,g3)
    c: PointOnObject(g8,g-3)
    c: PointOnObject(g8,g-3)
    c: DistanceX(g8,g8) = 10
    c: DistanceX(g8,g6) = 1
    c: Horizontal(g9)
    c: Vertical(g7,g9)
    c: Vertical(g6,g9)
    c: DistanceY(g9,g7) = 8
    c: Horizontal(g10)
    c: Equal(g8,g10)
    c: DistanceY(g10,g8) = 3
    c: Radius(g11) = 20
    c: Coincident(g11,g6)
    c: Coincident(g11,g9)
    c: Radius(g12) = 20
    c: Coincident(g12,g7)
    c: Coincident(g12,g9)
    c: Equal(g13,g11)
    c: Coincident(g13,g8)
    c: Coincident(g13,g10)
    c: Horizontal(g13,g11)
    c: Equal(g14,g12)
    c: Coincident(g14,g8)
    c: Coincident(g14,g10)
    c: Horizontal(g1,g-6)
FEATURE [Sketcher::SketchObject] Sketch122
  ArcFitTolerance = 1e-06
  AttachmentSupport = -> [Pad011]
  ExternalGeometry = -> [Binder001]
  FullyConstrained = true
  MakeInternals = false
  MapMode = 5
  Placement = pos=(0,-2,0) rot=(1,0,0;1.5708rad)
  sketch-geometry (8):
    g0: LineSegment StartX=-202.765 StartY=20.303 StartZ=0 EndX=-143.955 EndY=20.303 EndZ=0
    g1: ArcOfCircle CenterX=-184.801 CenterY=-67.3089 CenterZ=0 NormalX=0 NormalY=0 NormalZ=1 AngleXU=0 Radius=33.7833 StartAngle=2.70526 EndAngle=3.54053
    g2: LineSegment StartX=-176.685 StartY=-80.4316 StartZ=0 EndX=-215.932 EndY=-80.4316 EndZ=0
    g3: LineSegment StartX=-215.42 StartY=-53.0315 StartZ=0 EndX=-192.176 EndY=-3.18454 EndZ=0
    g4: ArcOfCircle CenterX=-207.583 CenterY=4 CenterZ=0 NormalX=0 NormalY=0 NormalZ=1 AngleXU=0 Radius=17 StartAngle=5.84685 EndAngle=7.56663
    g5: Circle CenterX=-213.443 CenterY=-76.8316 CenterZ=0 NormalX=0 NormalY=0 NormalZ=1 AngleXU=0 Radius=3
    g6: Circle CenterX=-179.305 CenterY=-76.8316 CenterZ=0 NormalX=0 NormalY=0 NormalZ=1 AngleXU=0 Radius=3
    g7: LineSegment StartX=-143.955 StartY=20.303 StartZ=0 EndX=-176.685 EndY=-80.4316 EndZ=0
  constraints (18):
    c: Coincident(g0,g-6)
    c: Coincident(g1,g-7)
    c: Coincident(g1,g-8)
    c: Coincident(g2,g1)
    c: Tangent(g3,g-5)
    c: Coincident(g4,g-6)
    c: Coincident(g4,g0)
    c: Coincident(g3,g4)
    c: Coincident(g1,g3)
    c: Diameter(g5) = 6
    c: Diameter(g6) = 6
    c: Coincident(g5,g-9)
    c: Coincident(g6,g-10)
    c: Horizontal(g0)
    c: Horizontal(g2)
    c: Coincident(g7,g0)
    c: Coincident(g7,g2)
    c: Tangent(g7,g-4)
FEATURE [Sketcher::SketchObject] Sketch123
  ArcFitTolerance = 1e-06
  AttachmentSupport = -> [Pad011]
  ExternalGeometry = -> [Binder001]
  FullyConstrained = true
  MakeInternals = false
  MapMode = 5
  Placement = pos=(0,-2,0) rot=(1,0,0;1.5708rad)
  sketch-geometry (4):
    g0: LineSegment StartX=-108 StartY=36.8 StartZ=0 EndX=-90 EndY=36.8 EndZ=0
    g1: LineSegment StartX=-108 StartY=36.8 StartZ=0 EndX=-108 EndY=26.8 EndZ=0
    g2: LineSegment StartX=-108 StartY=26.8 StartZ=0 EndX=-90 EndY=26.8 EndZ=0
    g3: ArcOfCircle CenterX=-94 CenterY=31.8 CenterZ=0 NormalX=0 NormalY=0 NormalZ=1 AngleXU=0 Radius=6.40312 StartAngle=5.38713 EndAngle=7.17924
  constraints (13):
    c: Horizontal(g0)
    c: Coincident(g1,g0)
    c: Vertical(g1)
    c: Coincident(g2,g1)
    c: Horizontal(g2)
    c: DistanceX(g0,g0) = 18
    c: DistanceY(g1,g1) = 10
    c: Equal(g0,g2)
    c: DistanceX(g0,g-3) = 90
    c: DistanceY(g0,g-3) = 2.4
    c: Coincident(g3,g0)
    c: Coincident(g3,g2)
    c: DistanceX(g3,g0) = 4
FEATURE [PartDesign::Chamfer] Chamfer014
  Angle = 45
  Base = -> Pad011 [Edge80,Edge4,Edge7]
  BaseFeature = -> Pad011
  ChamferType = 0
  FlipDirection = false
  Refine = true
  Size = 1.9
  Size2 = 1
  SupportTransform = false
  Suppressed = false
  UseAllEdges = false
FEATURE [PartDesign::Pocket] Pocket006
  BaseFeature = -> Chamfer014
  Direction = (0,-1,2e-16)
  Length = 1.2
  Length2 = 5
  Profile = -> Sketch115
  ReferenceAxis = -> Sketch115 [N_Axis]
  Refine = true
  Suppressed = false
  Type = 0
FEATURE [Sketcher::SketchObject] Sketch116  label="Sketch116 - pieno per inserto M3 x 3 x 4,5"
  ArcFitTolerance = 1e-06
  AttachmentSupport = -> [Pocket006]
  ExternalGeometry = -> [Binder001]
  FullyConstrained = true
  MakeInternals = false
  MapMode = 5
  Placement = pos=(0,1.7e-15,0) rot=(0,0.707107,0.707107;3.14159rad)
  sketch-geometry (4):
    g0: Circle CenterX=43.2 CenterY=30.3 CenterZ=0 NormalX=0 NormalY=0 NormalZ=1 AngleXU=0 Radius=3.4
    g1: Circle CenterX=43.2 CenterY=12.1 CenterZ=0 NormalX=0 NormalY=0 NormalZ=1 AngleXU=0 Radius=3.4
    g2: Circle CenterX=18.6 CenterY=30.3 CenterZ=0 NormalX=0 NormalY=0 NormalZ=1 AngleXU=0 Radius=3.4
    g3: Circle CenterX=18.6 CenterY=12.1 CenterZ=0 NormalX=0 NormalY=0 NormalZ=1 AngleXU=0 Radius=3.4
  constraints (8):
    c: Diameter(g0) = 6.8
    c: Diameter(g1) = 6.8
    c: Diameter(g2) = 6.8
    c: Diameter(g3) = 6.8
    c: Coincident(g2,g-3)
    c: Coincident(g0,g-4)
    c: Coincident(g3,g-6)
    c: Coincident(g1,g-5)
FEATURE [PartDesign::Pad] Pad012
  BaseFeature = -> Pocket006
  Direction = (0,1,-2e-16)
  Length = 2.4
  Length2 = 10
  Profile = -> Sketch116
  ReferenceAxis = -> Sketch116 [N_Axis]
  Refine = true
  Suppressed = false
  Type = 0
FEATURE [PartDesign::Pocket] Pocket007
  BaseFeature = -> Pad012
  Direction = (0,-1,2e-16)
  Length = 0.6
  Length2 = 2.4
  Profile = -> Sketch117
  ReferenceAxis = -> Sketch117 [N_Axis]
  Refine = true
  Suppressed = false
  Type = 4
FEATURE [PartDesign::Pad] Pad013
  BaseFeature = -> Pocket007
  Direction = (0,-1,2e-16)
  Length = 1.6
  Length2 = 10
  Profile = -> Sketch118
  ReferenceAxis = -> Sketch118 [N_Axis]
  Refine = true
  Suppressed = false
  Type = 0
FEATURE [Sketcher::SketchObject] Sketch119
  ArcFitTolerance = 1e-06
  AttachmentSupport = -> [Pad013]
  ExternalGeometry = -> [Binder001]
  FullyConstrained = true
  MakeInternals = false
  MapMode = 5
  Placement = pos=(0,-3.6,0) rot=(1,0,0;1.5708rad)
  sketch-geometry (21):
    g0: LineSegment [constr] StartX=-82.8 StartY=3.2 StartZ=0 EndX=-82.8 EndY=39.2 EndZ=0
    g1: ArcOfCircle CenterX=-78.51 CenterY=34.8 CenterZ=0 NormalX=0 NormalY=0 NormalZ=1 AngleXU=0 Radius=3.5 StartAngle=4.71239 EndAngle=6.28319
    g2: ArcOfCircle CenterX=-78.51 CenterY=7.6 CenterZ=0 NormalX=0 NormalY=0 NormalZ=1 AngleXU=0 Radius=3.5 StartAngle=0 EndAngle=1.5708
    g3: ArcOfCircle CenterX=-5.6 CenterY=34.8 CenterZ=0 NormalX=0 NormalY=0 NormalZ=1 AngleXU=0 Radius=3.5 StartAngle=3.14159 EndAngle=4.71239
    g4: ArcOfCircle CenterX=-5.6 CenterY=7.6 CenterZ=0 NormalX=0 NormalY=0 NormalZ=1 AngleXU=0 Radius=3.5 StartAngle=1.5708 EndAngle=3.14159
    g5: LineSegment StartX=0 StartY=39.2 StartZ=0 EndX=0 EndY=31.3 EndZ=0
    g6: LineSegment StartX=0 StartY=39.2 StartZ=0 EndX=-9.1 EndY=39.2 EndZ=0
    g7: LineSegment StartX=0 StartY=3.2 StartZ=0 EndX=0 EndY=11.1 EndZ=0
    g8: LineSegment StartX=0 StartY=3.2 StartZ=0 EndX=-9.1 EndY=3.2 EndZ=0
    g9: LineSegment StartX=-82.8 StartY=3.2 StartZ=0 EndX=-75.01 EndY=3.2 EndZ=0
    g10: LineSegment StartX=-82.8 StartY=3.2 StartZ=0 EndX=-82.8 EndY=11.1 EndZ=0
    g11: LineSegment StartX=-82.8 StartY=39.2 StartZ=0 EndX=-82.8 EndY=31.3 EndZ=0
    g12: LineSegment StartX=-82.8 StartY=39.2 StartZ=0 EndX=-75.01 EndY=39.2 EndZ=0
    g13: LineSegment StartX=-82.8 StartY=31.3 StartZ=0 EndX=-78.51 EndY=31.3 EndZ=0
    g14: LineSegment StartX=-75.01 StartY=39.2 StartZ=0 EndX=-75.01 EndY=34.8 EndZ=0
    g15: LineSegment StartX=-82.8 StartY=11.1 StartZ=0 EndX=-78.51 EndY=11.1 EndZ=0
    g16: LineSegment StartX=-75.01 StartY=3.2 StartZ=0 EndX=-75.01 EndY=7.6 EndZ=0
    g17: LineSegment StartX=-9.1 StartY=39.2 StartZ=0 EndX=-9.1 EndY=34.8 EndZ=0
    g18: LineSegment StartX=0 StartY=31.3 StartZ=0 EndX=-5.6 EndY=31.3 EndZ=0
    g19: LineSegment StartX=0 StartY=11.1 StartZ=0 EndX=-5.6 EndY=11.1 EndZ=0
    g20: LineSegment StartX=-9.1 StartY=3.2 StartZ=0 EndX=-9.1 EndY=7.6 EndZ=0
  constraints (51):
    c: Coincident(g0,g-10)
    c: PointOnObject(g0,g-8)
    c: Vertical(g0)
    c: Coincident(g1,g-3)
    c: Coincident(g2,g-4)
    c: Coincident(g3,g-5)
    c: Coincident(g4,g-6)
    c: Radius(g4) = 3.5
    c: Radius(g3) = 3.5
    c: Radius(g1) = 3.5
    c: Radius(g2) = 3.5
    c: Coincident(g5,g-9)
    c: PointOnObject(g5,g-9)
    c: Coincident(g6,g5)
    c: PointOnObject(g6,g-8)
    c: Coincident(g7,g-9)
    c: PointOnObject(g7,g-9)
    c: Coincident(g8,g7)
    c: PointOnObject(g8,g-7)
    c: Coincident(g9,g0)
    c: PointOnObject(g9,g-7)
    c: Coincident(g10,g0)
    c: PointOnObject(g10,g0)
    c: Coincident(g11,g0)
    c: PointOnObject(g11,g0)
    c: Coincident(g12,g0)
    c: PointOnObject(g12,g-8)
    c: Coincident(g13,g11)
    c: Horizontal(g13)
    c: Coincident(g14,g12)
    c: Vertical(g14)
    c: Coincident(g15,g10)
    c: Horizontal(g15)
    c: Coincident(g16,g9)
    c: Vertical(g16)
    c: Coincident(g17,g6)
    c: Vertical(g17)
    c: Coincident(g18,g5)
    c: Horizontal(g18)
    c: Coincident(g19,g7)
    c: Horizontal(g19)
    c: Coincident(g20,g8)
    c: Vertical(g20)
    c: Tangent(g20,g4) = 1.5708
    c: Tangent(g4,g19) = -1.5708
    c: Tangent(g18,g3) = 1.5708
    c: Tangent(g3,g17) = -1.5708
    c: Tangent(g13,g1) = -1.5708
    c: Tangent(g1,g14) = 1.5708
    c: Tangent(g16,g2) = -1.5708
    c: Tangent(g2,g15) = 1.5708
FEATURE [PartDesign::Pocket] Pocket008
  BaseFeature = -> Pad013
  Direction = (0,1,-2e-16)
  Length = 1.6
  Length2 = 5
  Profile = -> Sketch119
  ReferenceAxis = -> Sketch119 [N_Axis]
  Refine = true
  Suppressed = false
  Type = 0
FEATURE [PartDesign::Pad] Pad017
  BaseFeature = -> Pocket008
  Direction = (0,-1,2e-16)
  Length = 1.6
  Length2 = 10
  Profile = -> Sketch123
  ReferenceAxis = -> Sketch123 [N_Axis]
  Refine = true
  Suppressed = false
  Type = 0
FEATURE [Sketcher::SketchObject] Sketch125
  ArcFitTolerance = 1e-06
  AttachmentSupport = -> [Pad017]
  ExternalGeometry = -> [Pad017]
  FullyConstrained = true
  MakeInternals = false
  MapMode = 5
  Placement = pos=(0,-3.6,8e-16) rot=(1,0,0;1.5708rad)
  sketch-geometry (20):
    g0: LineSegment StartX=-108 StartY=35.8 StartZ=0 EndX=-108 EndY=35 EndZ=0
    g1: LineSegment StartX=-108 StartY=35 StartZ=0 EndX=-97 EndY=35 EndZ=0
    g2: LineSegment StartX=-97 StartY=35 StartZ=0 EndX=-97 EndY=35.8 EndZ=0
    g3: LineSegment StartX=-97 StartY=35.8 StartZ=0 EndX=-108 EndY=35.8 EndZ=0
    g4: LineSegment StartX=-108 StartY=28.6 StartZ=0 EndX=-108 EndY=27.8 EndZ=0
    g5: LineSegment StartX=-108 StartY=27.8 StartZ=0 EndX=-97 EndY=27.8 EndZ=0
    g6: LineSegment StartX=-97 StartY=27.8 StartZ=0 EndX=-97 EndY=28.6 EndZ=0
    g7: LineSegment StartX=-97 StartY=28.6 StartZ=0 EndX=-108 EndY=28.6 EndZ=0
    g8: LineSegment StartX=-108 StartY=30.4 StartZ=0 EndX=-108 EndY=29.6 EndZ=0
    g9: LineSegment StartX=-108 StartY=29.6 StartZ=0 EndX=-97 EndY=29.6 EndZ=0
    g10: LineSegment StartX=-97 StartY=29.6 StartZ=0 EndX=-97 EndY=30.4 EndZ=0
    g11: LineSegment StartX=-97 StartY=30.4 StartZ=0 EndX=-108 EndY=30.4 EndZ=0
    g12: LineSegment StartX=-108 StartY=32.2 StartZ=0 EndX=-108 EndY=31.4 EndZ=0
    g13: LineSegment StartX=-108 StartY=31.4 StartZ=0 EndX=-97 EndY=31.4 EndZ=0
    g14: LineSegment StartX=-97 StartY=31.4 StartZ=0 EndX=-97 EndY=32.2 EndZ=0
    g15: LineSegment StartX=-97 StartY=32.2 StartZ=0 EndX=-108 EndY=32.2 EndZ=0
    g16: LineSegment StartX=-108 StartY=34 StartZ=0 EndX=-108 EndY=33.2 EndZ=0
    g17: LineSegment StartX=-108 StartY=33.2 StartZ=0 EndX=-97 EndY=33.2 EndZ=0
    g18: LineSegment StartX=-97 StartY=33.2 StartZ=0 EndX=-97 EndY=34 EndZ=0
    g19: LineSegment StartX=-97 StartY=34 StartZ=0 EndX=-108 EndY=34 EndZ=0
  constraints (55):
    c: Coincident(g1,g0)
    c: Horizontal(g1)
    c: Coincident(g2,g1)
    c: Vertical(g2)
    c: Coincident(g3,g2)
    c: Horizontal(g3)
    c: Coincident(g3,g0)
    c: DistanceX(g1,g1) = 11
    c: DistanceY(g2,g2) = 0.8
    c: Coincident(g5,g4)
    c: Horizontal(g5)
    c: Coincident(g6,g5)
    c: Vertical(g6)
    c: Coincident(g7,g6)
    c: Horizontal(g7)
    c: Coincident(g7,g4)
    c: Coincident(g9,g8)
    c: Horizontal(g9)
    c: Coincident(g10,g9)
    c: Vertical(g10)
    c: Coincident(g11,g10)
    c: Horizontal(g11)
    c: Coincident(g11,g8)
    c: Coincident(g13,g12)
    c: Horizontal(g13)
    c: Coincident(g14,g13)
    c: Vertical(g14)
    c: Coincident(g15,g14)
    c: Horizontal(g15)
    c: Coincident(g15,g12)
    c: Coincident(g17,g16)
    c: Horizontal(g17)
    c: Coincident(g18,g17)
    c: Vertical(g18)
    c: Coincident(g19,g18)
    c: Horizontal(g19)
    c: Coincident(g19,g16)
    c: Equal(g3,g19)
    c: Equal(g3,g15)
    c: Equal(g3,g11)
    c: Equal(g3,g7)
    c: Equal(g2,g18)
    c: Equal(g2,g14)
    c: Equal(g2,g10)
    c: Equal(g2,g6)
    c: DistanceY(g-4,g4) = 1
    c: DistanceY(g4,g8) = 1
    c: DistanceY(g8,g12) = 1
    c: DistanceY(g12,g16) = 1
    c: DistanceY(g16,g0) = 1
    c: Tangent(g0,g-5)
    c: Tangent(g16,g-5)
    c: Tangent(g12,g-5)
    c: Tangent(g8,g-5)
    c: Tangent(g4,g-5)
FEATURE [PartDesign::Chamfer] Chamfer009
  Angle = 45
  Base = -> Pad017 [Edge151,Edge154]
  BaseFeature = -> Pad017
  ChamferType = 1
  FlipDirection = false
  Refine = true
  Size = 1.5
  Size2 = 2.8
  SupportTransform = false
  Suppressed = false
  UseAllEdges = false
FEATURE [PartDesign::Pocket] Pocket009
  BaseFeature = -> Chamfer009
  Direction = (0,1,-2e-16)
  Length = 1
  Length2 = 5
  Profile = -> Sketch125
  ReferenceAxis = -> Sketch125 [N_Axis]
  Refine = true
  Suppressed = false
  Type = 0
FEATURE [PartDesign::Pad] Pad014
  BaseFeature = -> Pocket009
  Direction = (0,-1,2e-16)
  Length = 0.8
  Length2 = 10
  Profile = -> Sketch120
  ReferenceAxis = -> Sketch120 [N_Axis]
  Refine = true
  Suppressed = false
  Type = 0
FEATURE [Sketcher::SketchObject] Sketch124
  ArcFitTolerance = 1e-06
  AttachmentSupport = -> [Pad014]
  ExternalGeometry = -> [Binder001]
  FullyConstrained = true
  MakeInternals = false
  MapMode = 5
  Placement = pos=(0,-2.8,6e-16) rot=(1,0,0;1.5708rad)
  sketch-geometry (4):
    g0: LineSegment StartX=-129 StartY=39.2 StartZ=0 EndX=-131.599 EndY=31.2 EndZ=0
    g1: LineSegment StartX=-118 StartY=39.2 StartZ=0 EndX=-120.599 EndY=31.2 EndZ=0
    g2: LineSegment StartX=-129 StartY=39.2 StartZ=0 EndX=-118 EndY=39.2 EndZ=0
    g3: LineSegment StartX=-120.599 StartY=31.2 StartZ=0 EndX=-131.599 EndY=31.2 EndZ=0
  constraints (12):
    c: PointOnObject(g0,g-3)
    c: PointOnObject(g1,g-3)
    c: Parallel(g-4,g0)
    c: Parallel(g-4,g1)
    c: Coincident(g2,g0)
    c: Coincident(g2,g1)
    c: DistanceX(g2,g2) = 11
    c: DistanceY(g1,g1) = 8
    c: Coincident(g3,g1)
    c: Horizontal(g3)
    c: Coincident(g3,g0)
    c: DistanceX(g1,g-3) = 118
FEATURE [PartDesign::Pad] Pad018
  BaseFeature = -> Pad014
  Direction = (0,-1,2e-16)
  Length = 1.2
  Length2 = 10
  Profile = -> Sketch124
  ReferenceAxis = -> Sketch124 [N_Axis]
  Refine = true
  Suppressed = false
  Type = 0
FEATURE [Sketcher::SketchObject] Sketch126
  ArcFitTolerance = 1e-06
  AttachmentSupport = -> [Pad018]
  ExternalGeometry = -> [Pad018]
  FullyConstrained = true
  MakeInternals = false
  MapMode = 5
  Placement = pos=(0,-4,0) rot=(1,0,0;1.5708rad)
  sketch-geometry (8):
    g0: LineSegment StartX=-129.877 StartY=36.5 StartZ=0 EndX=-130.137 EndY=35.7 EndZ=0
    g1: LineSegment StartX=-130.69 StartY=34 StartZ=0 EndX=-130.95 EndY=33.2 EndZ=0
    g2: LineSegment StartX=-129.877 StartY=36.5 StartZ=0 EndX=-118.877 EndY=36.5 EndZ=0
    g3: LineSegment StartX=-130.137 StartY=35.7 StartZ=0 EndX=-119.137 EndY=35.7 EndZ=0
    g4: LineSegment StartX=-130.69 StartY=34 StartZ=0 EndX=-119.69 EndY=34 EndZ=0
    g5: LineSegment StartX=-130.95 StartY=33.2 StartZ=0 EndX=-119.95 EndY=33.2 EndZ=0
    g6: LineSegment StartX=-118.877 StartY=36.5 StartZ=0 EndX=-119.137 EndY=35.7 EndZ=0
    g7: LineSegment StartX=-119.69 StartY=34 StartZ=0 EndX=-119.95 EndY=33.2 EndZ=0
  constraints (20):
    c: Coincident(g2,g0)
    c: Horizontal(g2)
    c: Coincident(g3,g0)
    c: Horizontal(g3)
    c: Coincident(g4,g1)
    c: Horizontal(g4)
    c: Coincident(g5,g1)
    c: Horizontal(g5)
    c: Coincident(g6,g2)
    c: Coincident(g6,g3)
    c: Coincident(g7,g4)
    c: Coincident(g7,g5)
    c: Tangent(g0,g-4)
    c: Tangent(g6,g-5)
    c: Tangent(g1,g-4)
    c: Tangent(g7,g-5)
    c: DistanceY(g3,g2) = 0.8
    c: DistanceY(g5,g4) = 0.8
    c: DistanceY(g-6,g1) = 2
    c: DistanceY(g-6,g0) = 4.5
FEATURE [PartDesign::Chamfer] Chamfer008
  Angle = 45
  Base = -> Pad018 [Edge257]
  BaseFeature = -> Pad018
  ChamferType = 1
  FlipDirection = false
  Refine = true
  Size = 1
  Size2 = 6
  SupportTransform = false
  Suppressed = false
  UseAllEdges = false
FEATURE [PartDesign::Pocket] Pocket010
  BaseFeature = -> Chamfer008
  Direction = (0,1,-2e-16)
  Length = 1
  Length2 = 5
  Profile = -> Sketch126
  ReferenceAxis = -> Sketch126 [N_Axis]
  Refine = true
  Suppressed = false
  Type = 0
FEATURE [PartDesign::Pad] Pad015
  BaseFeature = -> Pocket010
  Direction = (0,-1,2e-16)
  Length = 2
  Length2 = 10
  Profile = -> Sketch121
  ReferenceAxis = -> Sketch121 [N_Axis]
  Refine = true
  Suppressed = false
  Type = 0
FEATURE [PartDesign::Pad] Pad016
  BaseFeature = -> Pad015
  Direction = (0,-1,2e-16)
  Length = 1.6
  Length2 = 10
  Profile = -> Sketch122
  ReferenceAxis = -> Sketch122 [N_Axis]
  Refine = true
  Suppressed = false
  Type = 0
FEATURE [Sketcher::SketchObject] Sketch127
  ArcFitTolerance = 1e-06
  AttachmentSupport = -> [Pad016]
  ExternalGeometry = -> [Pad016]
  FullyConstrained = true
  MakeInternals = false
  MapMode = 5
  Placement = pos=(0,0,-80.4316) rot=(1,0,0;3.14159rad)
  sketch-geometry (8):
    g0: LineSegment StartX=-176.685 StartY=3.6 StartZ=0 EndX=-186.685 EndY=3.6 EndZ=0
    g1: LineSegment [constr] StartX=-186.685 StartY=3.6 StartZ=0 EndX=-186.685 EndY=-9e-16 EndZ=0
    g2: LineSegment StartX=-176.685 StartY=3.6 StartZ=0 EndX=-176.685 EndY=0 EndZ=0
    g3: ArcOfEllipse CenterX=-186.685 CenterY=-9e-16 CenterZ=0 NormalX=0 NormalY=0 NormalZ=1 MajorRadius=10 MinorRadius=3.6 AngleXU=1e-16 StartAngle=0 EndAngle=1.5708
    g4: LineSegment [constr] StartX=-176.685 StartY=-2e-15 StartZ=0 EndX=-196.685 EndY=-2e-15 EndZ=0
    g5: LineSegment [constr] StartX=-186.685 StartY=3.6 StartZ=0 EndX=-186.685 EndY=-3.6 EndZ=0
    g6: GeomPoint [constr] X=-177.356 Y=0 Z=0
    g7: GeomPoint [constr] X=-196.015 Y=-1.9e-15 Z=0
  constraints (13):
    c: Coincident(g0,g-4)
    c: PointOnObject(g0,g-4)
    c: DistanceX(g0,g0) = 10
    c: Coincident(g1,g0)
    c: PointOnObject(g1,g-5)
    c: Vertical(g1)
    c: Coincident(g2,g0)
    c: Coincident(g2,g-5)
    c: InternalAlignment(g4-g7 -> g3) x4
    c: Coincident(g3,g1)
    c: Coincident(g3,g0)
    c: Coincident(g3,g2)
    c: Horizontal(g4)
FEATURE [Sketcher::SketchObject] Sketch128
  ArcFitTolerance = 1e-06
  AttachmentSupport = -> [Pad016]
  ExternalGeometry = -> [Pad016]
  FullyConstrained = true
  MakeInternals = false
  MapMode = 5
  Placement = pos=(0,0,-80.4316) rot=(1,0,0;3.14159rad)
  sketch-geometry (8):
    g0: LineSegment StartX=-215.932 StartY=3.6 StartZ=0 EndX=-215.932 EndY=-1.3e-15 EndZ=0
    g1: LineSegment StartX=-215.932 StartY=3.6 StartZ=0 EndX=-205.932 EndY=3.6 EndZ=0
    g2: LineSegment [constr] StartX=-205.932 StartY=3.6 StartZ=0 EndX=-205.932 EndY=-9e-16 EndZ=0
    g3: ArcOfEllipse CenterX=-205.932 CenterY=-9e-16 CenterZ=0 NormalX=0 NormalY=0 NormalZ=1 MajorRadius=10 MinorRadius=3.6 AngleXU=-3.14159 StartAngle=4.71239 EndAngle=6.28319
    g4: LineSegment [constr] StartX=-215.932 StartY=-1e-15 StartZ=0 EndX=-195.932 EndY=-1e-15 EndZ=0
    g5: LineSegment [constr] StartX=-205.932 StartY=-3.6 StartZ=0 EndX=-205.932 EndY=3.6 EndZ=0
    g6: GeomPoint [constr] X=-215.262 Y=-2e-15 Z=0
    g7: GeomPoint [constr] X=-196.602 Y=-1e-15 Z=0
  constraints (13):
    c: Coincident(g0,g-4)
    c: Coincident(g0,g-5)
    c: Coincident(g1,g0)
    c: PointOnObject(g1,g-3)
    c: DistanceX(g1,g1) = 10
    c: Coincident(g2,g1)
    c: Vertical(g2)
    c: PointOnObject(g2,g-5)
    c: InternalAlignment(g4-g7 -> g3) x4
    c: Coincident(g3,g2)
    c: Coincident(g3,g1)
    c: Coincident(g3,g0)
    c: Horizontal(g4)
FEATURE [PartDesign::SubtractivePipe] SubtractivePipe002
  AuxilleryCurvelinear = true
  AuxillerySpineTangent = false
  BaseFeature = -> Pad016
  Binormal = (0,0,0)
  Mode = 0
  Profile = -> Sketch127
  Refine = true
  Spine = -> Pad016 [Edge254]
  SpineTangent = false
  Suppressed = false
  Transformation = 0
  Transition = 0
FEATURE [PartDesign::SubtractivePipe] SubtractivePipe003
  AuxilleryCurvelinear = true
  AuxillerySpineTangent = false
  BaseFeature = -> SubtractivePipe002
  Binormal = (0,0,0)
  Mode = 0
  Profile = -> Sketch128
  Refine = true
  Spine = -> Pad016 [Edge256,Edge251,Edge252]
  SpineTangent = false
  Suppressed = false
  Transformation = 0
  Transition = 0
FEATURE [Sketcher::SketchObject] Sketch129
  ArcFitTolerance = 1e-06
  AttachmentSupport = -> [Pad016]
  ExternalGeometry = -> [Binder001]
  FullyConstrained = true
  MakeInternals = false
  MapMode = 5
  Placement = pos=(0,-3.6,0) rot=(1,0,0;1.5708rad)
  sketch-geometry (12):
    g0: LineSegment [constr] StartX=-192.176 StartY=-3.18451 StartZ=0 EndX=-181.223 EndY=20.303 EndZ=0
    g1: LineSegment [constr] StartX=-202.765 StartY=20.303 StartZ=0 EndX=-181.223 EndY=20.303 EndZ=0
    g2: LineSegment StartX=-202.765 StartY=20.303 StartZ=0 EndX=-181.223 EndY=20.303 EndZ=0
    g3: LineSegment StartX=-192.176 StartY=-3.18451 StartZ=0 EndX=-196.804 EndY=-13.1107 EndZ=0
    g4: ArcOfCircle CenterX=-207.583 CenterY=4 CenterZ=0 NormalX=0 NormalY=0 NormalZ=1 AngleXU=0 Radius=17 StartAngle=5.84685 EndAngle=7.56663
    g5: ArcOfEllipse CenterX=-181.223 CenterY=8.55923 CenterZ=0 NormalX=0 NormalY=0 NormalZ=1 MajorRadius=23.4779 MinorRadius=11.7437 AngleXU=2e-16 StartAngle=4.71239 EndAngle=7.85398
    g6: LineSegment [constr] StartX=-157.745 StartY=8.55923 StartZ=0 EndX=-204.701 EndY=8.55923 EndZ=0
    g7: LineSegment [constr] StartX=-181.223 StartY=20.303 StartZ=0 EndX=-181.223 EndY=-3.18451 EndZ=0
    g8: GeomPoint [constr] X=-160.894 Y=8.55923 Z=0
    g9: GeomPoint [constr] X=-201.553 Y=8.55923 Z=0
    g10: ArcOfCircle CenterX=-181.223 CenterY=-20.3763 CenterZ=0 NormalX=0 NormalY=0 NormalZ=1 AngleXU=0 Radius=17.1918 StartAngle=1.57079 EndAngle=2.70526
    g11: GeomPoint [constr] X=-181.223 Y=-3.18451 Z=0
  constraints (23):
    c: Coincident(g0,g-5)
    c: Coincident(g1,g-6)
    c: Horizontal(g1)
    c: Coincident(g1,g0)
    c: Parallel(g0,g-4)
    c: Coincident(g2,g1)
    c: Coincident(g2,g0)
    c: Coincident(g3,g0)
    c: Equal(g4,g-5)
    c: Coincident(g4,g1)
    c: Coincident(g4,g0)
    c: InternalAlignment(g6-g9 -> g5) x4
    c: Vertical(g5,g0)
    c: Horizontal(g6)
    c: Coincident(g5,g0)
    c: DistanceX(g6,g-3) = 10.1
    c: Tangent(g10,g3) = -1.5708
    c: PointOnObject(g11,g10)
    c: Tangent(g5,g10,g11) = 1.5708
    c: Coincident(g10,g5)
    c: Coincident(g11,g7)
    c: Parallel(g3,g-4)
    c: Horizontal(g5,g0)
FEATURE [Sketcher::SketchObject] Sketch130
  ArcFitTolerance = 1e-06
  AttachmentOffset = pos=(0,0,-1.6) rot=(0,0,1;0rad)
  AttachmentSupport = -> [Pad016]
  ExternalGeometry = -> [Binder001]
  FullyConstrained = true
  MakeInternals = false
  MapMode = 5
  Placement = pos=(0,-2,-4e-16) rot=(1,0,0;1.5708rad)
  sketch-geometry (12):
    g0: LineSegment [constr] StartX=-192.176 StartY=-3.18451 StartZ=0 EndX=-181.223 EndY=20.303 EndZ=0
    g1: LineSegment [constr] StartX=-202.765 StartY=20.303 StartZ=0 EndX=-181.223 EndY=20.303 EndZ=0
    g2: LineSegment StartX=-202.765 StartY=20.303 StartZ=0 EndX=-181.223 EndY=20.303 EndZ=0
    g3: LineSegment StartX=-192.176 StartY=-3.18451 StartZ=0 EndX=-193.827 EndY=-6.72678 EndZ=0
    g4: ArcOfCircle CenterX=-207.583 CenterY=4 CenterZ=0 NormalX=0 NormalY=0 NormalZ=1 AngleXU=0 Radius=17 StartAngle=5.84685 EndAngle=7.56663
    g5: ArcOfEllipse CenterX=-181.223 CenterY=10.803 CenterZ=0 NormalX=0 NormalY=0 NormalZ=1 MajorRadius=14.4779 MinorRadius=9.5 AngleXU=0 StartAngle=4.71239 EndAngle=7.85398
    g6: LineSegment [constr] StartX=-166.745 StartY=10.803 StartZ=0 EndX=-195.701 EndY=10.803 EndZ=0
    g7: LineSegment [constr] StartX=-181.223 StartY=20.303 StartZ=0 EndX=-181.223 EndY=1.30297 EndZ=0
    g8: GeomPoint [constr] X=-170.298 Y=10.803 Z=0
    g9: GeomPoint [constr] X=-192.148 Y=10.803 Z=0
    g10: ArcOfCircle CenterX=-181.223 CenterY=-12.6042 CenterZ=0 NormalX=0 NormalY=0 NormalZ=1 AngleXU=0 Radius=13.9072 StartAngle=1.5708 EndAngle=2.70526
    g11: GeomPoint [constr] X=-181.223 Y=1.30297 Z=0
  constraints (23):
    c: Coincident(g0,g-5)
    c: Coincident(g1,g-6)
    c: Horizontal(g1)
    c: Coincident(g1,g0)
    c: Parallel(g0,g-4)
    c: Coincident(g2,g1)
    c: Coincident(g2,g0)
    c: Coincident(g3,g0)
    c: Equal(g4,g-5)
    c: Coincident(g4,g1)
    c: Coincident(g4,g0)
    c: InternalAlignment(g6-g9 -> g5) x4
    c: Vertical(g5,g0)
    c: Horizontal(g6)
    c: Coincident(g5,g0)
    c: DistanceX(g6,g-3) = 19.1
    c: Tangent(g10,g3) = -1.5708
    c: PointOnObject(g11,g10)
    c: Tangent(g5,g10,g11) = 1.5708
    c: Coincident(g10,g5)
    c: Coincident(g11,g7)
    c: Parallel(g3,g-4)
    c: DistanceY(g5,g0) = 19
FEATURE [Part::Part2DObjectPython] Clone2D001  label="Sketch130 (2D)"  # Draft 2D object (typed FeaturePython)
  Fuse = false
  Objects = -> [Sketch130]
  Placement = pos=(0,-2,-4e-16) rot=(1,0,0;1.5708rad)
  Scale = (1,1,1)
FEATURE [Sketcher::SketchObject] Sketch131
  ArcFitTolerance = 1e-06
  AttachmentOffset = pos=(0,0,-3.5) rot=(0,0,1;0rad)
  AttachmentSupport = -> [Pad016]
  ExternalGeometry = -> [Binder001]
  FullyConstrained = true
  MakeInternals = false
  MapMode = 5
  Placement = pos=(0,-0.1,-8e-16) rot=(1,0,0;1.5708rad)
  sketch-geometry (1):
    g0: GeomPoint X=-197.47 Y=8.55923 Z=0
  constraints (1):
    c: Symmetric(g-6,g-4,g0)
FEATURE [PartDesign::SubtractiveLoft] SubtractiveLoft002
  BaseFeature = -> SubtractivePipe003
  Closed = false
  Profile = -> Sketch129
  Refine = true
  Ruled = false
  Sections = -> [Sketch130]
  Suppressed = false
FEATURE [PartDesign::SubtractiveLoft] SubtractiveLoft003
  BaseFeature = -> SubtractiveLoft002
  Closed = false
  Profile = -> Clone2D001
  Refine = true
  Ruled = false
  Sections = -> [Sketch131]
  Suppressed = false
FEATURE [PartDesign::Chamfer] Chamfer010
  Angle = 45
  Base = -> SubtractiveLoft003 [Edge200,Edge201,Edge203,Edge202,Edge194]
  BaseFeature = -> SubtractiveLoft003
  ChamferType = 0
  FlipDirection = false
  Refine = true
  Size = 1.5
  Size2 = 1
  SupportTransform = false
  Suppressed = false
  UseAllEdges = false
FEATURE [PartDesign::Chamfer] Chamfer011
  Angle = 45
  Base = -> Chamfer010 [Edge15]
  BaseFeature = -> Chamfer010
  ChamferType = 0
  FlipDirection = false
  Refine = true
  Size = 1.6
  Size2 = 1
  SupportTransform = false
  Suppressed = false
  UseAllEdges = false
FEATURE [PartDesign::Chamfer] Chamfer012
  Angle = 45
  Base = -> Chamfer011 [Edge10]
  BaseFeature = -> Chamfer011
  ChamferType = 0
  FlipDirection = false
  Refine = true
  Size = 3.5
  Size2 = 1
  SupportTransform = false
  Suppressed = false
  UseAllEdges = false
FEATURE [PartDesign::Chamfer] Chamfer013
  Angle = 45
  Base = -> Chamfer012 [Edge145,Edge94]
  BaseFeature = -> Chamfer012
  ChamferType = 0
  FlipDirection = false
  Refine = true
  Size = 1.9
  Size2 = 1
  SupportTransform = false
  Suppressed = false
  UseAllEdges = false
FEATURE [Sketcher::SketchObject] Sketch132
  ArcFitTolerance = 1e-06
  AttachmentSupport = -> [Pad016]
  ExternalGeometry = -> [Binder001]
  FullyConstrained = true
  MakeInternals = false
  MapMode = 5
  Placement = pos=(0,-3.6,0) rot=(1,0,0;1.5708rad)
  sketch-geometry (3):
    g0: LineSegment [constr] StartX=-215.42 StartY=-53.0314 StartZ=0 EndX=-167.782 EndY=-53.0314 EndZ=0
    g1: Circle CenterX=-191.282 CenterY=-53.0314 CenterZ=0 NormalX=0 NormalY=0 NormalZ=1 AngleXU=0 Radius=11.5
    g2: Circle CenterX=-191.282 CenterY=-53.0314 CenterZ=0 NormalX=0 NormalY=0 NormalZ=1 AngleXU=0 Radius=10.7
  constraints (8):
    c: Coincident(g0,g-3)
    c: PointOnObject(g0,g-4)
    c: Horizontal(g0)
    c: Diameter(g1) = 23
    c: PointOnObject(g1,g0)
    c: DistanceX(g1,g0) = 23.5
    c: Diameter(g2) = 21.4
    c: Coincident(g2,g1)
FEATURE [PartDesign::Fillet] Fillet007
  Base = -> Chamfer013 [Edge83]
  BaseFeature = -> Chamfer013
  Radius = 1.1
  Refine = true
  SupportTransform = false
  Suppressed = false
  UseAllEdges = false
FEATURE [PartDesign::Fillet] Fillet008
  Base = -> Fillet007 [Edge76]
  BaseFeature = -> Fillet007
  Radius = 1.9
  Refine = true
  SupportTransform = false
  Suppressed = false
  UseAllEdges = false
FEATURE [PartDesign::Pocket] Pocket011
  BaseFeature = -> Fillet008
  Direction = (0,1,-2e-16)
  Length = 0.8
  Length2 = 5
  Profile = -> Sketch132
  ReferenceAxis = -> Sketch132 [N_Axis]
  Refine = true
  Suppressed = false
  Type = 0
FEATURE [Part::Part2DObjectPython] ShapeString  # Draft 2D object (typed FeaturePython)
  FontFile = <path>
  Fuse = false
  Justification = 6
  JustificationReference = 0
  KeepLeftMargin = false
  MakeFace = true
  ObliqueAngle = 0
  Placement = pos=(-199,-3.6,-57.5) rot=(1,0,0;1.5708rad)
  ScaleToSize = true
  Size = 10
  String = AS
  Tracking = 0
FEATURE [PartDesign::Pocket] Pocket012
  BaseFeature = -> Pocket011
  Direction = (0,1,0)
  Length = 1
  Length2 = 5
  Profile = -> ShapeString
  ReferenceAxis = -> ShapeString [N_Axis]
  Refine = true
  Suppressed = false
  Type = 0
FEATURE [PartDesign::Body] Body007  label="lato DX"
  AllowCompound = false
  Group = -> [Binder001,Sketch114,Pad011,Chamfer014,Sketch115,Pocket006,Sketch116,Pad012,Sketch117,Pocket007,Sketch118,Pad013,Sketch119,Pocket008,Pad017,Chamfer009,Pocket009,Sketch123,Sketch120,Pad014,Pad018,Chamfer008,Pocket010,Sketch121,Pad015,Sketch122,Pad016,Sketch124,Sketch125,Sketch126,Sketch127,Sketch128,SubtractivePipe002,SubtractivePipe003,Sketch129,Sketch130,Clone2D001,Sketch131,SubtractiveLoft002,+11 more]
  Origin = -> Origin007
  Tip = -> Pocket012
FEATURE [Sketcher::SketchObject] Sketch133
  ArcFitTolerance = 1e-06
  AttachmentSupport = -> [Binder]
  ExternalGeometry = -> [Binder]
  FullyConstrained = true
  MakeInternals = false
  MapMode = 5
  Placement = pos=(0,9e-16,0) rot=(0,0.707107,0.707107;3.14159rad)
  sketch-geometry (30):
    g0: LineSegment StartX=0 StartY=39.2 StartZ=0 EndX=0 EndY=3.2 EndZ=0
    g1: LineSegment StartX=0 StartY=3.2 StartZ=0 EndX=82.8 EndY=3.2 EndZ=0
    g2: LineSegment StartX=82.8 StartY=3.2 StartZ=0 EndX=82.8 EndY=6.2 EndZ=0
    g3: LineSegment StartX=82.8 StartY=6.2 StartZ=0 EndX=91.752 EndY=6.2 EndZ=0
    g4: LineSegment StartX=0 StartY=39.2 StartZ=0 EndX=195.887 EndY=39.2 EndZ=0
    g5: LineSegment StartX=195.887 StartY=39.2 StartZ=0 EndX=202.765 EndY=20.303 EndZ=0
    g6: LineSegment StartX=192.333 StartY=24.9893 StartZ=0 EndX=196.467 EndY=26.4942 EndZ=0
    g7: LineSegment StartX=196.467 StartY=26.4942 StartZ=0 EndX=194.073 EndY=33.0721 EndZ=0
    g8: LineSegment StartX=194.073 StartY=33.0721 StartZ=0 EndX=189.939 EndY=31.5672 EndZ=0
    g9: LineSegment StartX=189.939 StartY=31.5672 StartZ=0 EndX=192.333 EndY=24.9893 EndZ=0
    g10: ArcOfCircle CenterX=107.6 CenterY=4 CenterZ=0 NormalX=0 NormalY=0 NormalZ=1 AngleXU=0 Radius=16 StartAngle=1.5708 EndAngle=3.00366
    g11: LineSegment StartX=107.6 StartY=20 StartZ=0 EndX=132.428 EndY=20 EndZ=0
    g12: ArcOfCircle [constr] CenterX=132.428 CenterY=4 CenterZ=0 NormalX=0 NormalY=0 NormalZ=1 AngleXU=0 Radius=16 StartAngle=0.314159 EndAngle=1.5708
    g13: LineSegment StartX=147.645 StartY=8.94427 StartZ=0 EndX=176.685 EndY=-80.4316 EndZ=0
    g14: LineSegment StartX=176.685 StartY=-80.4316 StartZ=0 EndX=215.932 EndY=-80.4316 EndZ=0
    g15: ArcOfCircle CenterX=207.583 CenterY=4 CenterZ=0 NormalX=0 NormalY=0 NormalZ=1 AngleXU=0 Radius=17 StartAngle=1.85815 EndAngle=3.57792
    g16: ArcOfCircle CenterX=184.801 CenterY=-67.3089 CenterZ=0 NormalX=0 NormalY=0 NormalZ=1 AngleXU=0 Radius=33.7833 StartAngle=5.88425 EndAngle=6.71952
    g17: LineSegment StartX=192.176 StartY=-3.18451 StartZ=0 EndX=215.42 EndY=-53.0314 EndZ=0
    g18: Circle CenterX=5.6 CenterY=34.8 CenterZ=0 NormalX=0 NormalY=0 NormalZ=1 AngleXU=0 Radius=1.8
    g19: Circle CenterX=5.6 CenterY=7.6 CenterZ=0 NormalX=0 NormalY=0 NormalZ=1 AngleXU=0 Radius=1.8
    g20: Circle CenterX=78.51 CenterY=34.8 CenterZ=0 NormalX=0 NormalY=0 NormalZ=1 AngleXU=0 Radius=1.8
    g21: Circle CenterX=78.51 CenterY=7.6 CenterZ=0 NormalX=0 NormalY=0 NormalZ=1 AngleXU=0 Radius=1.8
    g22: Circle CenterX=184.08 CenterY=34.8 CenterZ=0 NormalX=0 NormalY=0 NormalZ=1 AngleXU=0 Radius=1.8
    g23: Circle CenterX=179.305 CenterY=-76.8316 CenterZ=0 NormalX=0 NormalY=0 NormalZ=1 AngleXU=0 Radius=1.8
    g24: Circle CenterX=213.443 CenterY=-76.8316 CenterZ=0 NormalX=0 NormalY=0 NormalZ=1 AngleXU=0 Radius=1.8
    g25: Circle CenterX=19 CenterY=21.2 CenterZ=0 NormalX=0 NormalY=0 NormalZ=1 AngleXU=0 Radius=6.3
    g26: Circle CenterX=42 CenterY=21.2 CenterZ=0 NormalX=0 NormalY=0 NormalZ=1 AngleXU=0 Radius=6.3
    g27: Circle CenterX=65 CenterY=21.2 CenterZ=0 NormalX=0 NormalY=0 NormalZ=1 AngleXU=0 Radius=6.3
    g28: LineSegment StartX=132.428 StartY=20 StartZ=0 EndX=144.053 EndY=20 EndZ=0
    g29: LineSegment StartX=147.645 StartY=8.94427 StartZ=0 EndX=144.053 EndY=20 EndZ=0
  constraints (65):
    c: Coincident(g0,g-4)
    c: Coincident(g0,g-5)
    c: Coincident(g1,g0)
    c: Coincident(g1,g-6)
    c: Coincident(g2,g1)
    c: Coincident(g2,g-7)
    c: Coincident(g3,g2)
    c: Coincident(g3,g-8)
    c: Coincident(g4,g0)
    c: Coincident(g4,g-16)
    c: Coincident(g5,g4)
    c: Coincident(g5,g-16)
    c: Coincident(g6,g-20)
    c: Coincident(g6,g-21)
    c: Coincident(g7,g6)
    c: Coincident(g7,g-23)
    c: Coincident(g8,g7)
    c: Coincident(g8,g-22)
    c: Coincident(g9,g8)
    c: Coincident(g9,g6)
    c: Equal(g10,g-8)
    c: Coincident(g10,g3)
    c: Coincident(g10,g-9)
    c: Coincident(g11,g10)
    c: Coincident(g11,g-10)
    c: Equal(g12,g-10)
    c: Coincident(g12,g11)
    c: Coincident(g12,g-11)
    c: Coincident(g13,g12)
    c: Coincident(g13,g-12)
    c: Coincident(g14,g13)
    c: Coincident(g14,g-13)
    c: Equal(g15,g-15)
    c: Coincident(g15,g5)
    c: Coincident(g15,g-15)
    c: Equal(g16,g-13)
    c: Coincident(g16,g14)
    c: Coincident(g16,g-14)
    c: Coincident(g17,g15)
    c: Coincident(g17,g16)
    c: Equal(g18,g-28)
    c: Equal(g19,g-29)
    c: Equal(g20,g-26)
    c: Equal(g21,g-27)
    c: Equal(g22,g-17)
    c: Equal(g24,g-25)
    c: Equal(g23,g-24)
    c: Coincident(g23,g-24)
    c: Coincident(g24,g-25)
    c: Coincident(g22,g-17)
    c: Coincident(g20,g-26)
    c: Coincident(g21,g-27)
    c: Coincident(g18,g-28)
    c: Coincident(g19,g-29)
    c: Equal(g25,g-30)
    c: Equal(g26,g-31)
    c: Equal(g27,g-32)
    c: Coincident(g25,g-30)
    c: Coincident(g26,g-31)
    c: Coincident(g27,g-32)
    c: Parallel(g28,g11)
    c: Parallel(g29,g13)
    c: Coincident(g28,g11)
    c: Coincident(g29,g12)
    c: Coincident(g29,g28)
FEATURE [PartDesign::Pad] Pad019
  Direction = (0,1,-2e-16)
  Length = 2
  Length2 = 10
  Profile = -> Sketch133
  ReferenceAxis = -> Sketch133 [N_Axis]
  Refine = true
  Suppressed = false
  Type = 0
FEATURE [Sketcher::SketchObject] Sketch091  label="Sketch091 - forma anteriore"
  ArcFitTolerance = 1e-06
  AttachmentSupport = -> [Pad019]
  ExternalGeometry = -> [Binder]
  FullyConstrained = true
  MakeInternals = false
  MapMode = 5
  Placement = pos=(0,2,0) rot=(0,0.707107,0.707107;3.14159rad)
  sketch-geometry (12):
    g0: Circle CenterX=5.6 CenterY=34.8 CenterZ=0 NormalX=0 NormalY=0 NormalZ=1 AngleXU=0 Radius=1.8
    g1: Circle CenterX=5.6 CenterY=7.6 CenterZ=0 NormalX=0 NormalY=0 NormalZ=1 AngleXU=0 Radius=1.8
    g2: Circle CenterX=78.51 CenterY=34.8 CenterZ=0 NormalX=0 NormalY=0 NormalZ=1 AngleXU=0 Radius=1.8
    g3: Circle CenterX=78.51 CenterY=7.6 CenterZ=0 NormalX=0 NormalY=0 NormalZ=1 AngleXU=0 Radius=1.8
    g4: LineSegment StartX=0 StartY=39.2 StartZ=0 EndX=0 EndY=3.2 EndZ=0
    g5: LineSegment StartX=0 StartY=3.2 StartZ=0 EndX=82.8 EndY=3.2 EndZ=0
    g6: LineSegment StartX=82.8 StartY=3.2 StartZ=0 EndX=82.8 EndY=39.2 EndZ=0
    g7: LineSegment StartX=82.8 StartY=39.2 StartZ=0 EndX=0 EndY=39.2 EndZ=0
    g8: ArcOfCircle CenterX=19 CenterY=21.2 CenterZ=0 NormalX=0 NormalY=0 NormalZ=1 AngleXU=0 Radius=10 StartAngle=1.5708 EndAngle=4.71239
    g9: ArcOfCircle CenterX=65 CenterY=21.2 CenterZ=0 NormalX=0 NormalY=0 NormalZ=1 AngleXU=0 Radius=10 StartAngle=4.71239 EndAngle=7.85398
    g10: LineSegment StartX=19 StartY=31.2 StartZ=0 EndX=65 EndY=31.2 EndZ=0
    g11: LineSegment StartX=19 StartY=11.2 StartZ=0 EndX=65 EndY=11.2 EndZ=0
  constraints (25):
    c: Equal(g2,g-7)
    c: Equal(g3,g-8)
    c: Equal(g1,g-13)
    c: Equal(g0,g-12)
    c: Coincident(g0,g-12)
    c: Coincident(g1,g-13)
    c: Coincident(g3,g-8)
    c: Coincident(g2,g-7)
    c: Coincident(g4,g-4)
    c: Coincident(g4,g-5)
    c: Coincident(g5,g4)
    c: Coincident(g5,g-6)
    c: Coincident(g6,g5)
    c: PointOnObject(g6,g-3)
    c: Vertical(g6)
    c: Coincident(g7,g6)
    c: Coincident(g7,g4)
    c: Tangent(g8,g10) = 1.5708
    c: Tangent(g8,g11) = -1.5708
    c: Tangent(g9,g10) = 1.5708
    c: Tangent(g9,g11) = -1.5708
    c: Equal(g8,g9)
    c: Radius(g8) = 10
    c: Coincident(g8,g-11)
    c: Coincident(g9,g-9)
FEATURE [Sketcher::SketchObject] Sketch093  label="Sketch093 - scavi interni pulsanti"
  ArcFitTolerance = 1e-06
  AttachmentSupport = -> [Pad019]
  ExternalGeometry = -> [Binder]
  FullyConstrained = true
  MakeInternals = false
  MapMode = 5
  Placement = pos=(0,1.8e-15,0) rot=(1,0,0;1.5708rad)
  sketch-geometry (3):
    g0: Circle CenterX=-65 CenterY=21.2 CenterZ=0 NormalX=0 NormalY=0 NormalZ=1 AngleXU=0 Radius=7.3
    g1: Circle CenterX=-42 CenterY=21.2 CenterZ=0 NormalX=0 NormalY=0 NormalZ=1 AngleXU=0 Radius=7.3
    g2: Circle CenterX=-19 CenterY=21.2 CenterZ=0 NormalX=0 NormalY=0 NormalZ=1 AngleXU=0 Radius=7.3
  constraints (6):
    c: Coincident(g0,g-3)
    c: Coincident(g1,g-4)
    c: Coincident(g2,g-5)
    c: Diameter(g0) = 14.6
    c: Diameter(g1) = 14.6
    c: Diameter(g2) = 14.6
FEATURE [Sketcher::SketchObject] Sketch094  label="Sketch094 - forma centrale"
  ArcFitTolerance = 1e-06
  AttachmentSupport = -> [Pad019]
  ExternalGeometry = -> [Binder]
  FullyConstrained = true
  MakeInternals = false
  MapMode = 5
  Placement = pos=(0,2,0) rot=(0,0.707107,0.707107;3.14159rad)
  sketch-geometry (4):
    g0: LineSegment StartX=137.815 StartY=39.2 StartZ=0 EndX=142.655 EndY=24.303 EndZ=0
    g1: LineSegment StartX=110.815 StartY=24.303 StartZ=0 EndX=142.655 EndY=24.303 EndZ=0
    g2: LineSegment StartX=137.815 StartY=39.2 StartZ=0 EndX=110.815 EndY=39.2 EndZ=0
    g3: ArcOfCircle CenterX=92.2534 CenterY=31.7515 CenterZ=0 NormalX=0 NormalY=0 NormalZ=1 AngleXU=0 Radius=20 StartAngle=5.90156 EndAngle=6.66481
  constraints (12):
    c: PointOnObject(g0,g-3)
    c: Tangent(g0,g-5)
    c: Horizontal(g1)
    c: Coincident(g1,g0)
    c: Coincident(g2,g0)
    c: PointOnObject(g2,g-3)
    c: DistanceX(g2,g2) = 27
    c: Vertical(g1,g2)
    c: Coincident(g3,g2)
    c: Radius(g3) = 20
    c: Coincident(g3,g1)
    c: DistanceY(g-6,g0) = 4
FEATURE [Sketcher::SketchObject] Sketch095  label="Sketch095 - forma posteriore"
  ArcFitTolerance = 1e-06
  AttachmentSupport = -> [Pad019]
  ExternalGeometry = -> [Binder]
  FullyConstrained = true
  MakeInternals = false
  MapMode = 5
  Placement = pos=(0,2,0) rot=(0,0.707107,0.707107;3.14159rad)
  sketch-geometry (15):
    g0: LineSegment StartX=137.815 StartY=39.2 StartZ=0 EndX=143.955 EndY=20.303 EndZ=0
    g1: LineSegment StartX=143.955 StartY=20.303 StartZ=0 EndX=190.141 EndY=20.303 EndZ=0
    g2: ArcOfCircle CenterX=184.08 CenterY=34.8 CenterZ=0 NormalX=0 NormalY=0 NormalZ=1 AngleXU=0 Radius=3.5 StartAngle=3.49066 EndAngle=4.71239
    g3: LineSegment StartX=180.791 StartY=33.6029 StartZ=0 EndX=178.754 EndY=39.2 EndZ=0
    g4: LineSegment StartX=184.08 StartY=31.3 StartZ=0 EndX=186.139 EndY=31.3 EndZ=0
    g5: LineSegment StartX=190.141 StartY=20.303 StartZ=0 EndX=186.139 EndY=31.3 EndZ=0
    g6: LineSegment StartX=137.815 StartY=39.2 StartZ=0 EndX=156.815 EndY=39.2 EndZ=0
    g7: LineSegment StartX=178.754 StartY=39.2 StartZ=0 EndX=168.815 EndY=39.2 EndZ=0
    g8: LineSegment StartX=156.815 StartY=31.2 StartZ=0 EndX=168.815 EndY=31.2 EndZ=0
    g9: ArcOfCircle CenterX=176.411 CenterY=35.2 CenterZ=0 NormalX=0 NormalY=0 NormalZ=1 AngleXU=0 Radius=20 StartAngle=2.94023 EndAngle=3.34295
    g10: ArcOfCircle CenterX=188.411 CenterY=35.2 CenterZ=0 NormalX=0 NormalY=0 NormalZ=1 AngleXU=0 Radius=20 StartAngle=2.94023 EndAngle=3.34295
    g11: LineSegment StartX=157.815 StartY=39.2 StartZ=0 EndX=167.815 EndY=39.2 EndZ=0
    g12: LineSegment StartX=157.436 StartY=36.2 StartZ=0 EndX=167.436 EndY=36.2 EndZ=0
    g13: ArcOfCircle CenterX=177.411 CenterY=35.2 CenterZ=0 NormalX=0 NormalY=0 NormalZ=1 AngleXU=0 Radius=20 StartAngle=2.94023 EndAngle=3.09157
    g14: ArcOfCircle CenterX=187.411 CenterY=35.2 CenterZ=0 NormalX=0 NormalY=0 NormalZ=1 AngleXU=0 Radius=20 StartAngle=2.94023 EndAngle=3.09157
  constraints (46):
    c: PointOnObject(g0,g-3)
    c: Tangent(g0,g-6)
    c: Coincident(g1,g0)
    c: Horizontal(g1)
    c: Radius(g2) = 3.5
    c: Coincident(g2,g-5)
    c: PointOnObject(g3,g-3)
    c: Parallel(g3,g-4)
    c: Tangent(g3,g2) = 1.5708
    c: Horizontal(g4)
    c: Tangent(g4,g2) = -1.5708
    c: Coincident(g5,g1)
    c: Parallel(g5,g-4)
    c: Coincident(g5,g4)
    c: DistanceX(g4,g-8) = 3.8
    c: Coincident(g6,g0)
    c: PointOnObject(g6,g-3)
    c: Coincident(g7,g3)
    c: PointOnObject(g7,g-3)
    c: Horizontal(g8)
    c: DistanceX(g6,g7) = 12
    c: Vertical(g8,g6)
    c: Vertical(g7,g8)
    c: DistanceY(g8,g6) = 8
    c: Coincident(g9,g8)
    c: Coincident(g9,g6)
    c: Coincident(g10,g7)
    c: Coincident(g10,g8)
    c: Radius(g9) = 20
    c: Radius(g10) = 20
    c: PointOnObject(g11,g-3)
    c: PointOnObject(g11,g-3)
    c: DistanceX(g11,g11) = 10
    c: DistanceX(g6,g11) = 1
    c: Horizontal(g12)
    c: Equal(g12,g11)
    c: DistanceY(g12,g11) = 3
    c: Coincident(g13,g11)
    c: Coincident(g13,g12)
    c: Radius(g13) = 20
    c: Coincident(g14,g11)
    c: Coincident(g14,g12)
    c: Radius(g14) = 20
    c: DistanceX(g0,g6) = 19
    c: Horizontal(g9,g13)
    c: Horizontal(g0,g-4)
FEATURE [Sketcher::SketchObject] Sketch096  label="Sketch096 - forma impugnatura"
  ArcFitTolerance = 1e-06
  AttachmentSupport = -> [Pad019]
  ExternalGeometry = -> [Binder]
  FullyConstrained = true
  MakeInternals = false
  MapMode = 5
  Placement = pos=(0,2,0) rot=(0,0.707107,0.707107;3.14159rad)
  sketch-geometry (8):
    g0: LineSegment StartX=176.685 StartY=-80.4316 StartZ=0 EndX=143.955 EndY=20.303 EndZ=0
    g1: LineSegment StartX=176.685 StartY=-80.4316 StartZ=0 EndX=215.932 EndY=-80.4316 EndZ=0
    g2: Circle CenterX=179.305 CenterY=-76.8316 CenterZ=0 NormalX=0 NormalY=0 NormalZ=1 AngleXU=0 Radius=3
    g3: Circle CenterX=213.443 CenterY=-76.8316 CenterZ=0 NormalX=0 NormalY=0 NormalZ=1 AngleXU=0 Radius=3
    g4: LineSegment StartX=143.955 StartY=20.303 StartZ=0 EndX=202.765 EndY=20.303 EndZ=0
    g5: LineSegment StartX=215.42 StartY=-53.0314 StartZ=0 EndX=192.176 EndY=-3.18451 EndZ=0
    g6: ArcOfCircle CenterX=184.801 CenterY=-67.3089 CenterZ=0 NormalX=0 NormalY=0 NormalZ=1 AngleXU=0 Radius=33.7833 StartAngle=5.88425 EndAngle=6.71952
    g7: ArcOfCircle CenterX=207.583 CenterY=4 CenterZ=0 NormalX=0 NormalY=0 NormalZ=1 AngleXU=0 Radius=17 StartAngle=1.85815 EndAngle=3.57792
  constraints (19):
    c: Coincident(g0,g-4)
    c: PointOnObject(g0,g-3)
    c: Horizontal(g0,g-7)
    c: Coincident(g1,g0)
    c: Coincident(g1,g-5)
    c: Diameter(g2) = 6
    c: Diameter(g3) = 6
    c: Coincident(g2,g-9)
    c: Coincident(g3,g-10)
    c: Coincident(g4,g0)
    c: Coincident(g5,g-6)
    c: Coincident(g6,g1)
    c: Coincident(g6,g5)
    c: Equal(g-5,g6)
    c: Coincident(g5,g-7)
    c: Coincident(g4,g-7)
    c: Tangent(g7,g-7)
    c: Coincident(g7,g4)
    c: Coincident(g7,g5)
FEATURE [Sketcher::SketchObject] Sketch097
  ArcFitTolerance = 1e-06
  AttachmentSupport = -> [Pad019]
  ExternalGeometry = -> [Binder]
  FullyConstrained = true
  MakeInternals = false
  MapMode = 5
  Placement = pos=(0,2,0) rot=(0,0.707107,0.707107;3.14159rad)
  sketch-geometry (4):
    g0: LineSegment StartX=90 StartY=36.8 StartZ=0 EndX=108 EndY=36.8 EndZ=0
    g1: LineSegment StartX=108 StartY=36.8 StartZ=0 EndX=108 EndY=26.8 EndZ=0
    g2: LineSegment StartX=108 StartY=26.8 StartZ=0 EndX=90 EndY=26.8 EndZ=0
    g3: ArcOfCircle CenterX=94 CenterY=31.8 CenterZ=0 NormalX=0 NormalY=0 NormalZ=1 AngleXU=0 Radius=6.40312 StartAngle=2.24554 EndAngle=4.03765
  constraints (13):
    c: Horizontal(g0)
    c: Coincident(g1,g0)
    c: Vertical(g1)
    c: DistanceX(g0,g0) = 18
    c: DistanceY(g1,g1) = 10
    c: Coincident(g2,g1)
    c: Horizontal(g2)
    c: Equal(g2,g0)
    c: DistanceY(g0,g-3) = 2.4
    c: Coincident(g3,g0)
    c: Coincident(g3,g2)
    c: DistanceX(g2,g3) = 4
    c: DistanceX(g-3,g0) = 90
FEATURE [PartDesign::Chamfer] Chamfer015
  Angle = 45
  Base = -> Pad019 [Edge19,Edge22,Edge79]
  BaseFeature = -> Pad019
  ChamferType = 0
  FlipDirection = false
  Refine = true
  Size = 1.9
  Size2 = 1
  SupportTransform = false
  Suppressed = false
  UseAllEdges = false
FEATURE [PartDesign::Pocket] Pocket002
  BaseFeature = -> Chamfer015
  Direction = (0,1,-2e-16)
  Length = 1.2
  Length2 = 5
  Profile = -> Sketch093
  ReferenceAxis = -> Sketch093 [N_Axis]
  Refine = true
  Suppressed = false
  Type = 0
FEATURE [PartDesign::Pad] Pad005
  BaseFeature = -> Pocket002
  Direction = (0,1,-2e-16)
  Length = 1.6
  Length2 = 10
  Profile = -> Sketch091
  ReferenceAxis = -> Sketch091 [N_Axis]
  Refine = true
  Suppressed = false
  Type = 0
FEATURE [Sketcher::SketchObject] Sketch092  label="Sketch092 - scavi per viti anteriori"
  ArcFitTolerance = 1e-06
  AttachmentSupport = -> [Pad005]
  ExternalGeometry = -> [Binder]
  FullyConstrained = true
  MakeInternals = false
  MapMode = 5
  Placement = pos=(0,3.6,0) rot=(0,0.707107,0.707107;3.14159rad)
  sketch-geometry (20):
    g0: ArcOfCircle CenterX=5.6 CenterY=7.6 CenterZ=0 NormalX=0 NormalY=0 NormalZ=1 AngleXU=0 Radius=3.5 StartAngle=0 EndAngle=1.5708
    g1: ArcOfCircle CenterX=5.6 CenterY=34.8 CenterZ=0 NormalX=0 NormalY=0 NormalZ=1 AngleXU=0 Radius=3.5 StartAngle=4.71239 EndAngle=6.28319
    g2: ArcOfCircle CenterX=78.51 CenterY=34.8 CenterZ=0 NormalX=0 NormalY=0 NormalZ=1 AngleXU=0 Radius=3.5 StartAngle=3.14159 EndAngle=4.71239
    g3: ArcOfCircle CenterX=78.51 CenterY=7.6 CenterZ=0 NormalX=0 NormalY=0 NormalZ=1 AngleXU=0 Radius=3.5 StartAngle=1.5708 EndAngle=3.14159
    g4: LineSegment StartX=0 StartY=3.2 StartZ=0 EndX=0 EndY=11.1 EndZ=0
    g5: LineSegment StartX=0 StartY=11.1 StartZ=0 EndX=5.6 EndY=11.1 EndZ=0
    g6: LineSegment StartX=0 StartY=3.2 StartZ=0 EndX=9.1 EndY=3.2 EndZ=0
    g7: LineSegment StartX=9.1 StartY=3.2 StartZ=0 EndX=9.1 EndY=7.6 EndZ=0
    g8: LineSegment StartX=0 StartY=39.2 StartZ=0 EndX=0 EndY=31.3 EndZ=0
    g9: LineSegment StartX=0 StartY=31.3 StartZ=0 EndX=5.6 EndY=31.3 EndZ=0
    g10: LineSegment StartX=0 StartY=39.2 StartZ=0 EndX=9.1 EndY=39.2 EndZ=0
    g11: LineSegment StartX=9.1 StartY=39.2 StartZ=0 EndX=9.1 EndY=34.8 EndZ=0
    g12: LineSegment StartX=82.8 StartY=39.2 StartZ=0 EndX=75.01 EndY=39.2 EndZ=0
    g13: LineSegment StartX=82.8 StartY=39.2 StartZ=0 EndX=82.8 EndY=31.3 EndZ=0
    g14: LineSegment StartX=82.8 StartY=31.3 StartZ=0 EndX=78.51 EndY=31.3 EndZ=0
    g15: LineSegment StartX=82.8 StartY=3.2 StartZ=0 EndX=75.01 EndY=3.2 EndZ=0
    g16: LineSegment StartX=75.01 StartY=3.2 StartZ=0 EndX=75.01 EndY=7.6 EndZ=0
    g17: LineSegment StartX=82.8 StartY=3.2 StartZ=0 EndX=82.8 EndY=11.1 EndZ=0
    g18: LineSegment StartX=82.8 StartY=11.1 StartZ=0 EndX=78.51 EndY=11.1 EndZ=0
    g19: LineSegment StartX=75.01 StartY=39.2 StartZ=0 EndX=75.01 EndY=34.8 EndZ=0
  constraints (48):
    c: Radius(g0) = 3.5
    c: Coincident(g0,g-10)
    c: Radius(g1) = 3.5
    c: Coincident(g1,g-9)
    c: Radius(g2) = 3.5
    c: Coincident(g2,g-8)
    c: Radius(g3) = 3.5
    c: Coincident(g3,g-7)
    c: Coincident(g4,g-5)
    c: PointOnObject(g4,g-4)
    c: Coincident(g5,g4)
    c: Horizontal(g5)
    c: Coincident(g6,g4)
    c: PointOnObject(g6,g-5)
    c: Coincident(g7,g6)
    c: Vertical(g7)
    c: Coincident(g8,g-4)
    c: PointOnObject(g8,g-4)
    c: Coincident(g9,g8)
    c: Horizontal(g9)
    c: Coincident(g10,g8)
    c: PointOnObject(g10,g-3)
    c: Coincident(g11,g10)
    c: Vertical(g11)
    c: PointOnObject(g12,g-3)
    c: PointOnObject(g12,g-3)
    c: Coincident(g13,g12)
    c: Vertical(g13)
    c: Coincident(g14,g13)
    c: Horizontal(g14)
    c: Coincident(g15,g-6)
    c: PointOnObject(g15,g-5)
    c: Coincident(g16,g15)
    c: Vertical(g16)
    c: Coincident(g17,g15)
    c: Coincident(g18,g17)
    c: Horizontal(g18)
    c: Tangent(g3,g18) = -1.5708
    c: Tangent(g16,g3) = 1.5708
    c: Coincident(g19,g12)
    c: Vertical(g19)
    c: Tangent(g2,g19) = -1.5708
    c: Tangent(g2,g14) = 1.5708
    c: Tangent(g0,g7) = -1.5708
    c: Tangent(g0,g5) = 1.5708
    c: Tangent(g9,g1) = -1.5708
    c: Tangent(g1,g11) = 1.5708
    c: Tangent(g17,g13)
FEATURE [PartDesign::Pocket] Pocket001
  BaseFeature = -> Pad005
  Direction = (0,-1,2e-16)
  Length = 1.6
  Length2 = 5
  Profile = -> Sketch092
  ReferenceAxis = -> Sketch092 [N_Axis]
  Refine = true
  Suppressed = false
  Type = 0
FEATURE [PartDesign::Pad] Pad006
  BaseFeature = -> Pocket001
  Direction = (0,1,-2e-16)
  Length = 0.8
  Length2 = 10
  Profile = -> Sketch094
  ReferenceAxis = -> Sketch094 [N_Axis]
  Refine = true
  Suppressed = false
  Type = 0
FEATURE [PartDesign::Pad] Pad007
  BaseFeature = -> Pad006
  Direction = (0,1,-2e-16)
  Length = 2
  Length2 = 10
  Profile = -> Sketch095
  ReferenceAxis = -> Sketch095 [N_Axis]
  Refine = true
  Suppressed = false
  Type = 0
FEATURE [PartDesign::Pad] Pad008  label="Pad008 - forma impugnatura"
  BaseFeature = -> Pad007
  Direction = (0,1,-2e-16)
  Length = 1.6
  Length2 = 10
  Profile = -> Sketch096
  ReferenceAxis = -> Sketch096 [N_Axis]
  Refine = true
  Suppressed = false
  Type = 0
FEATURE [PartDesign::Pad] Pad009
  BaseFeature = -> Pad008
  Direction = (0,1,-2e-16)
  Length = 1.6
  Length2 = 10
  Profile = -> Sketch097
  ReferenceAxis = -> Sketch097 [N_Axis]
  Refine = true
  Suppressed = false
  Type = 0
FEATURE [Sketcher::SketchObject] Sketch098
  ArcFitTolerance = 1e-06
  AttachmentSupport = -> [Pad006]
  ExternalGeometry = -> [Binder]
  FullyConstrained = true
  MakeInternals = false
  MapMode = 5
  Placement = pos=(0,2.8,-7e-16) rot=(0,0.707107,0.707107;3.14159rad)
  sketch-geometry (4):
    g0: LineSegment StartX=118 StartY=39.2 StartZ=0 EndX=129 EndY=39.2 EndZ=0
    g1: LineSegment StartX=120.599 StartY=31.2 StartZ=0 EndX=131.599 EndY=31.2 EndZ=0
    g2: LineSegment StartX=129 StartY=39.2 StartZ=0 EndX=131.599 EndY=31.2 EndZ=0
    g3: LineSegment StartX=118 StartY=39.2 StartZ=0 EndX=120.599 EndY=31.2 EndZ=0
  constraints (12):
    c: PointOnObject(g0,g-3)
    c: PointOnObject(g0,g-3)
    c: DistanceX(g0,g0) = 11
    c: Horizontal(g1)
    c: Equal(g1,g0)
    c: Coincident(g2,g0)
    c: Coincident(g3,g0)
    c: Parallel(g-4,g2)
    c: Coincident(g1,g2)
    c: Coincident(g1,g3)
    c: DistanceY(g1,g0) = 8
    c: DistanceX(g-3,g0) = 118
FEATURE [Sketcher::SketchObject] Sketch099
  ArcFitTolerance = 1e-06
  AttachmentSupport = -> [Pad008]
  ExternalGeometry = -> [Binder]
  FullyConstrained = true
  MakeInternals = false
  MapMode = 5
  Placement = pos=(0,3.6,0) rot=(0,0.707107,0.707107;3.14159rad)
  sketch-geometry (13):
    g0: LineSegment StartX=192.176 StartY=-3.18451 StartZ=0 EndX=196.804 EndY=-13.1108 EndZ=0
    g1: LineSegment [constr] StartX=202.765 StartY=20.303 StartZ=0 EndX=181.223 EndY=20.303 EndZ=0
    g2: LineSegment [constr] StartX=181.223 StartY=20.303 StartZ=0 EndX=181.223 EndY=-3.18451 EndZ=0
    g3: ArcOfCircle CenterX=181.223 CenterY=-20.3764 CenterZ=0 NormalX=0 NormalY=0 NormalZ=1 AngleXU=0 Radius=17.1918 StartAngle=0.436332 EndAngle=1.57079
    g4: ArcOfEllipse CenterX=181.223 CenterY=8.55923 CenterZ=0 NormalX=0 NormalY=0 NormalZ=1 MajorRadius=23.4779 MinorRadius=11.7437 AngleXU=0 StartAngle=1.5708 EndAngle=4.71239
    g5: LineSegment [constr] StartX=204.701 StartY=8.55923 StartZ=0 EndX=157.745 EndY=8.55923 EndZ=0
    g6: LineSegment [constr] StartX=181.223 StartY=20.303 StartZ=0 EndX=181.223 EndY=-3.18451 EndZ=0
    g7: GeomPoint [constr] X=201.553 Y=8.55923 Z=0
    g8: GeomPoint [constr] X=160.894 Y=8.55923 Z=0
    g9: GeomPoint [constr] X=181.223 Y=-3.18451 Z=0
    g10: LineSegment StartX=181.223 StartY=20.303 StartZ=0 EndX=202.765 EndY=20.303 EndZ=0
    g11: ArcOfCircle CenterX=207.583 CenterY=4 CenterZ=0 NormalX=0 NormalY=0 NormalZ=1 AngleXU=0 Radius=17 StartAngle=1.85815 EndAngle=3.57792
    g12: LineSegment [constr] StartX=172.411 StartY=39.2 StartZ=0 EndX=192.176 EndY=-3.18451 EndZ=0
  constraints (27):
    c: Coincident(g1,g-7)
    c: Horizontal(g1)
    c: Coincident(g2,g1)
    c: Vertical(g2)
    c: Horizontal(g2,g0)
    c: Coincident(g3,g0)
    c: Coincident(g3,g2)
    c: InternalAlignment(g5-g8 -> g4) x4
    c: Horizontal(g5)
    c: PointOnObject(g4,g2)
    c: Coincident(g4,g1)
    c: DistanceX(g-3,g5) = 10.1
    c: Coincident(g4,g2)
    c: Tangent(g3,g-5)
    c: PointOnObject(g9,g4)
    c: PointOnObject(g9,g3)
    c: Tangent(g4,g3,g9) = 1.5708
    c: Coincident(g10,g1)
    c: Coincident(g10,g1)
    c: Equal(g11,g-4)
    c: Coincident(g11,g1)
    c: Coincident(g11,g0)
    c: PointOnObject(g12,g-6)
    c: PointOnObject(g1,g12)
    c: Tangent(g12,g-5) = -1.5708
    c: Tangent(g0,g-5) = -1.5708
    c: Horizontal(g9,g12)
FEATURE [Sketcher::SketchObject] Sketch106  label="Sketch106 - smusso impuniatura interno"
  ArcFitTolerance = 1e-06
  AttachmentSupport = -> [Pad008]
  ExternalGeometry = -> [Pad008]
  FullyConstrained = true
  MakeInternals = false
  MapMode = 5
  Placement = pos=(0,-1.586e-13,-80.4316) rot=(1,0,0;3.14159rad)
  sketch-geometry (9):
    g0: LineSegment StartX=-176.685 StartY=-3.6 StartZ=0 EndX=-176.685 EndY=-1.492e-13 EndZ=0
    g1: LineSegment [constr] StartX=-176.685 StartY=-1.416e-13 StartZ=0 EndX=-176.685 EndY=-1.49e-13 EndZ=0
    g2: LineSegment [constr] StartX=-186.685 StartY=-3.6 StartZ=0 EndX=-186.685 EndY=-1.492e-13 EndZ=0
    g3: ArcOfEllipse CenterX=-186.685 CenterY=-1.49e-13 CenterZ=0 NormalX=0 NormalY=0 NormalZ=1 MajorRadius=10 MinorRadius=3.6 AngleXU=3.14159 StartAngle=1.5708 EndAngle=3.14159
    g4: LineSegment [constr] StartX=-196.685 StartY=-1.416e-13 StartZ=0 EndX=-176.685 EndY=-1.416e-13 EndZ=0
    g5: LineSegment [constr] StartX=-186.685 StartY=-3.6 StartZ=0 EndX=-186.685 EndY=3.6 EndZ=0
    g6: GeomPoint [constr] X=-196.015 Y=-1.416e-13 Z=0
    g7: GeomPoint [constr] X=-177.356 Y=-1.416e-13 Z=0
    g8: LineSegment StartX=-176.685 StartY=-3.6 StartZ=0 EndX=-186.685 EndY=-3.6 EndZ=0
  constraints (15):
    c: PointOnObject(g2,g-3)
    c: Coincident(g1,g-5)
    c: DistanceY(g1,g1) = 0
    c: Coincident(g0,g1)
    c: DistanceX(g2,g-5) = 10
    c: Vertical(g2)
    c: Horizontal(g2,g0)
    c: InternalAlignment(g4-g7 -> g3) x4
    c: Coincident(g3,g2)
    c: Horizontal(g4)
    c: Coincident(g3,g0)
    c: Tangent(g0,g-5) = 1.5708
    c: Coincident(g3,g2)
    c: Coincident(g8,g0)
    c: Coincident(g8,g2)
FEATURE [Sketcher::SketchObject] Sketch107  label="Sketch107 - smusso impugnatura esterno"
  ArcFitTolerance = 1e-06
  AttachmentSupport = -> [Pad008]
  ExternalGeometry = -> [Pad008]
  FullyConstrained = true
  MakeInternals = false
  MapMode = 5
  Placement = pos=(0,-1.586e-13,-80.4316) rot=(1,0,0;3.14159rad)
  sketch-geometry (9):
    g0: LineSegment [constr] StartX=-215.932 StartY=1.79e-14 StartZ=0 EndX=-215.932 EndY=2.71e-14 EndZ=0
    g1: LineSegment StartX=-215.932 StartY=-3.6 StartZ=0 EndX=-215.932 EndY=2.71e-14 EndZ=0
    g2: LineSegment StartX=-215.932 StartY=-3.6 StartZ=0 EndX=-205.932 EndY=-3.6 EndZ=0
    g3: LineSegment [constr] StartX=-205.932 StartY=-3.6 StartZ=0 EndX=-205.932 EndY=2.71e-14 EndZ=0
    g4: ArcOfEllipse CenterX=-205.932 CenterY=2.71e-14 CenterZ=0 NormalX=0 NormalY=0 NormalZ=1 MajorRadius=10 MinorRadius=3.6 AngleXU=3.14159 StartAngle=1e-16 EndAngle=1.5708
    g5: LineSegment [constr] StartX=-215.932 StartY=1.79e-14 StartZ=0 EndX=-195.932 EndY=1.79e-14 EndZ=0
    g6: LineSegment [constr] StartX=-205.932 StartY=-3.6 StartZ=0 EndX=-205.932 EndY=3.6 EndZ=0
    g7: GeomPoint [constr] X=-215.262 Y=2.76e-14 Z=0
    g8: GeomPoint [constr] X=-196.602 Y=1.78e-14 Z=0
  constraints (16):
    c: Coincident(g0,g-6)
    c: PointOnObject(g0,g-6)
    c: DistanceY(g0,g0) = 0
    c: Coincident(g1,g-6)
    c: Coincident(g1,g0)
    c: Tangent(g2,g-3)
    c: DistanceX(g2,g2) = 10
    c: Coincident(g3,g2)
    c: Vertical(g3)
    c: Horizontal(g3,g0)
    c: InternalAlignment(g5-g8 -> g4) x4
    c: Coincident(g4,g3)
    c: Horizontal(g5)
    c: Coincident(g4,g0)
    c: Coincident(g4,g2)
    c: PointOnObject(g2,g1)
FEATURE [Sketcher::SketchObject] Sketch108
  ArcFitTolerance = 1e-06
  AttachmentOffset = pos=(0,0,-1.6) rot=(0,0,1;0rad)
  AttachmentSupport = -> [Pad008]
  ExternalGeometry = -> [Binder]
  FullyConstrained = true
  MakeInternals = false
  MapMode = 5
  Placement = pos=(0,2,4e-16) rot=(0,0.707107,0.707107;3.14159rad)
  sketch-geometry (14):
    g0: LineSegment StartX=192.176 StartY=-3.18451 StartZ=0 EndX=193.827 EndY=-6.72678 EndZ=0
    g1: LineSegment [constr] StartX=202.765 StartY=20.303 StartZ=0 EndX=181.223 EndY=20.303 EndZ=0
    g2: LineSegment [constr] StartX=181.223 StartY=20.303 StartZ=0 EndX=181.223 EndY=1.30297 EndZ=0
    g3: ArcOfCircle CenterX=181.223 CenterY=-12.6042 CenterZ=0 NormalX=0 NormalY=0 NormalZ=1 AngleXU=0 Radius=13.9072 StartAngle=0.436332 EndAngle=1.5708
    g4: ArcOfEllipse CenterX=181.223 CenterY=10.803 CenterZ=0 NormalX=0 NormalY=0 NormalZ=1 MajorRadius=14.4779 MinorRadius=9.5 AngleXU=0 StartAngle=1.5708 EndAngle=4.71239
    g5: LineSegment [constr] StartX=195.701 StartY=10.803 StartZ=0 EndX=166.745 EndY=10.803 EndZ=0
    g6: LineSegment [constr] StartX=181.223 StartY=20.303 StartZ=0 EndX=181.223 EndY=1.30297 EndZ=0
    g7: GeomPoint [constr] X=192.148 Y=10.803 Z=0
    g8: GeomPoint [constr] X=170.298 Y=10.803 Z=0
    g9: LineSegment StartX=181.223 StartY=20.303 StartZ=0 EndX=202.765 EndY=20.303 EndZ=0
    g10: ArcOfCircle CenterX=207.583 CenterY=4 CenterZ=0 NormalX=0 NormalY=0 NormalZ=1 AngleXU=0 Radius=17 StartAngle=1.85815 EndAngle=3.57792
    g11: LineSegment [constr] StartX=172.411 StartY=39.2 StartZ=0 EndX=192.176 EndY=-3.18451 EndZ=0
    g12: GeomPoint [constr] X=181.223 Y=1.30297 Z=0
    g13: GeomPoint [constr] X=181.223 Y=1.30297 Z=0
  constraints (28):
    c: Coincident(g1,g-7)
    c: Horizontal(g1)
    c: Coincident(g2,g1)
    c: Vertical(g2)
    c: Coincident(g3,g2)
    c: InternalAlignment(g5-g8 -> g4) x4
    c: Horizontal(g5)
    c: PointOnObject(g4,g2)
    c: Coincident(g4,g1)
    c: DistanceX(g-3,g5) = 19.1
    c: Coincident(g4,g2)
    c: Coincident(g9,g1)
    c: Coincident(g9,g1)
    c: Coincident(g10,g1)
    c: Coincident(g10,g0)
    c: PointOnObject(g11,g-6)
    c: PointOnObject(g1,g11)
    c: DistanceY(g2,g1) = 19
    c: Coincident(g10,g-4)
    c: PointOnObject(g12,g4)
    c: PointOnObject(g12,g3)
    c: Tangent(g11,g-5) = -1.5708
    c: Tangent(g0,g-5) = -1.5708
    c: Tangent(g3,g0) = 1.5708
    c: PointOnObject(g13,g4)
    c: PointOnObject(g13,g3)
    c: Tangent(g4,g3,g13) = 1.5708
    c: Horizontal(g11,g0)
FEATURE [Part::Part2DObjectPython] Clone2D  label="Sketch108 (2D)"  # Draft 2D object (typed FeaturePython)
  Fuse = false
  Objects = -> [Sketch108]
  Placement = pos=(0,2,4e-16) rot=(0,0.707107,0.707107;3.14159rad)
  Scale = (1,1,1)
FEATURE [Sketcher::SketchObject] Sketch109
  ArcFitTolerance = 1e-06
  AttachmentOffset = pos=(0,0,-3.5) rot=(0,0,1;0rad)
  AttachmentSupport = -> [Pad008]
  ExternalGeometry = -> [Binder]
  FullyConstrained = true
  MakeInternals = false
  MapMode = 5
  Placement = pos=(0,0.1,8e-16) rot=(0,0.707107,0.707107;3.14159rad)
  sketch-geometry (1):
    g0: GeomPoint X=197.47 Y=8.55923 Z=0
  constraints (1):
    c: Symmetric(g-7,g-5,g0)
FEATURE [PartDesign::Chamfer] Chamfer005
  Angle = 45
  Base = -> Pad009 [Edge215,Edge212]
  BaseFeature = -> Pad009
  ChamferType = 1
  FlipDirection = false
  Refine = true
  Size = 1.5
  Size2 = 2.8
  SupportTransform = false
  Suppressed = false
  UseAllEdges = false
FEATURE [Sketcher::SketchObject] Sketch111
  ArcFitTolerance = 1e-06
  AttachmentSupport = -> [Pad009]
  ExternalGeometry = -> [Pad009]
  FullyConstrained = true
  MakeInternals = false
  MapMode = 5
  Placement = pos=(0,3.6,-8e-16) rot=(0,0.707107,0.707107;3.14159rad)
  sketch-geometry (21):
    g0: LineSegment [constr] StartX=97 StartY=36.8 StartZ=0 EndX=97 EndY=26.8 EndZ=0
    g1: LineSegment StartX=97 StartY=28.6 StartZ=0 EndX=97 EndY=27.8 EndZ=0
    g2: LineSegment StartX=97 StartY=27.8 StartZ=0 EndX=108 EndY=27.8 EndZ=0
    g3: LineSegment StartX=108 StartY=27.8 StartZ=0 EndX=108 EndY=28.6 EndZ=0
    g4: LineSegment StartX=108 StartY=28.6 StartZ=0 EndX=97 EndY=28.6 EndZ=0
    g5: LineSegment StartX=97 StartY=35.8 StartZ=0 EndX=97 EndY=35 EndZ=0
    g6: LineSegment StartX=97 StartY=35 StartZ=0 EndX=108 EndY=35 EndZ=0
    g7: LineSegment StartX=108 StartY=35 StartZ=0 EndX=108 EndY=35.8 EndZ=0
    g8: LineSegment StartX=108 StartY=35.8 StartZ=0 EndX=97 EndY=35.8 EndZ=0
    g9: LineSegment StartX=97 StartY=30.4 StartZ=0 EndX=97 EndY=29.6 EndZ=0
    g10: LineSegment StartX=97 StartY=29.6 StartZ=0 EndX=108 EndY=29.6 EndZ=0
    g11: LineSegment StartX=108 StartY=29.6 StartZ=0 EndX=108 EndY=30.4 EndZ=0
    g12: LineSegment StartX=108 StartY=30.4 StartZ=0 EndX=97 EndY=30.4 EndZ=0
    g13: LineSegment StartX=97 StartY=34 StartZ=0 EndX=97 EndY=33.2 EndZ=0
    g14: LineSegment StartX=97 StartY=33.2 StartZ=0 EndX=108 EndY=33.2 EndZ=0
    g15: LineSegment StartX=108 StartY=33.2 StartZ=0 EndX=108 EndY=34 EndZ=0
    g16: LineSegment StartX=108 StartY=34 StartZ=0 EndX=97 EndY=34 EndZ=0
    g17: LineSegment StartX=97 StartY=32.2 StartZ=0 EndX=97 EndY=31.4 EndZ=0
    g18: LineSegment StartX=97 StartY=31.4 StartZ=0 EndX=108 EndY=31.4 EndZ=0
    g19: LineSegment StartX=108 StartY=31.4 StartZ=0 EndX=108 EndY=32.2 EndZ=0
    g20: LineSegment StartX=108 StartY=32.2 StartZ=0 EndX=97 EndY=32.2 EndZ=0
  constraints (54):
    c: Vertical(g0)
    c: PointOnObject(g0,g-3)
    c: PointOnObject(g0,g-4)
    c: DistanceX(g0,g-5) = 11
    c: Coincident(g1,g2)
    c: Coincident(g2,g3)
    c: Coincident(g3,g4)
    c: Coincident(g4,g1)
    c: Horizontal(g2)
    c: Horizontal(g4)
    c: Tangent(g1,g0)
    c: Tangent(g3,g-5)
    c: DistanceY(g2,g3) = 0.8
    c: Coincident(g5,g6)
    c: Coincident(g6,g7)
    c: Coincident(g7,g8)
    c: Coincident(g8,g5)
    c: Horizontal(g6)
    c: Horizontal(g8)
    c: DistanceY(g6,g7) = 0.8
    c: Coincident(g9,g10)
    c: Coincident(g10,g11)
    c: Coincident(g11,g12)
    c: Coincident(g12,g9)
    c: Horizontal(g10)
    c: Horizontal(g12)
    c: DistanceY(g10,g11) = 0.8
    c: Tangent(g5,g0)
    c: Tangent(g7,g-5)
    c: Tangent(g9,g0)
    c: Tangent(g11,g-5)
    c: Coincident(g13,g14)
    c: Coincident(g14,g15)
    c: Coincident(g15,g16)
    c: Coincident(g16,g13)
    c: Horizontal(g14)
    c: Horizontal(g16)
    c: DistanceY(g14,g15) = 0.8
    c: Tangent(g13,g0)
    c: Tangent(g15,g-5)
    c: Coincident(g17,g18)
    c: Coincident(g18,g19)
    c: Coincident(g19,g20)
    c: Coincident(g20,g17)
    c: Horizontal(g18)
    c: Horizontal(g20)
    c: DistanceY(g18,g19) = 0.8
    c: Tangent(g17,g0)
    c: Tangent(g19,g-5)
    c: DistanceY(g1,g9) = 1
    c: DistanceY(g9,g17) = 1
    c: DistanceY(g17,g13) = 1
    c: DistanceY(g13,g5) = 1
    c: DistanceY(g0,g1) = 1
FEATURE [PartDesign::Pocket] Pocket004
  BaseFeature = -> Chamfer005
  Direction = (0,-1,2e-16)
  Length = 1
  Length2 = 5
  Profile = -> Sketch111
  ReferenceAxis = -> Sketch111 [N_Axis]
  Refine = true
  Suppressed = false
  Type = 0
FEATURE [PartDesign::Pad] Pad010
  BaseFeature = -> Pocket004
  Direction = (0,1,-2e-16)
  Length = 1.2
  Length2 = 10
  Profile = -> Sketch098
  ReferenceAxis = -> Sketch098 [N_Axis]
  Refine = true
  Suppressed = false
  Type = 0
FEATURE [PartDesign::Chamfer] Chamfer006
  Angle = 45
  Base = -> Pad010 [Edge291]
  BaseFeature = -> Pad010
  ChamferType = 1
  FlipDirection = false
  Refine = true
  Size = 1
  Size2 = 6
  SupportTransform = false
  Suppressed = false
  UseAllEdges = false
FEATURE [Sketcher::SketchObject] Sketch110
  ArcFitTolerance = 1e-06
  AttachmentSupport = -> [Pad010]
  ExternalGeometry = -> [Sketch098]
  FullyConstrained = true
  MakeInternals = false
  MapMode = 5
  Placement = pos=(0,4,-9e-16) rot=(0,0.707107,0.707107;3.14159rad)
  sketch-geometry (8):
    g0: LineSegment StartX=119.69 StartY=34 StartZ=0 EndX=130.69 EndY=34 EndZ=0
    g1: LineSegment StartX=119.95 StartY=33.2 StartZ=0 EndX=130.95 EndY=33.2 EndZ=0
    g2: LineSegment StartX=119.137 StartY=35.7 StartZ=0 EndX=130.137 EndY=35.7 EndZ=0
    g3: LineSegment StartX=118.877 StartY=36.5 StartZ=0 EndX=129.877 EndY=36.5 EndZ=0
    g4: LineSegment StartX=118.877 StartY=36.5 StartZ=0 EndX=119.137 EndY=35.7 EndZ=0
    g5: LineSegment StartX=129.877 StartY=36.5 StartZ=0 EndX=130.137 EndY=35.7 EndZ=0
    g6: LineSegment StartX=119.69 StartY=34 StartZ=0 EndX=119.95 EndY=33.2 EndZ=0
    g7: LineSegment StartX=130.69 StartY=34 StartZ=0 EndX=130.95 EndY=33.2 EndZ=0
  constraints (24):
    c: Horizontal(g0)
    c: Horizontal(g1)
    c: Horizontal(g2)
    c: Horizontal(g3)
    c: Equal(g1,g-5)
    c: Equal(g0,g-5)
    c: Equal(g2,g-5)
    c: Equal(g3,g-5)
    c: PointOnObject(g0,g-3)
    c: PointOnObject(g1,g-3)
    c: PointOnObject(g2,g-3)
    c: PointOnObject(g3,g-3)
    c: Coincident(g4,g3)
    c: Coincident(g4,g2)
    c: Coincident(g5,g3)
    c: Coincident(g5,g2)
    c: Coincident(g6,g0)
    c: Coincident(g6,g1)
    c: Coincident(g7,g0)
    c: Coincident(g7,g1)
    c: DistanceY(g1,g0) = 0.8
    c: DistanceY(g2,g3) = 0.8
    c: DistanceY(g-5,g1) = 2
    c: DistanceY(g-5,g2) = 4.5
FEATURE [PartDesign::Pocket] Pocket003
  BaseFeature = -> Chamfer006
  Direction = (0,-1,2e-16)
  Length = 1
  Length2 = 5
  Profile = -> Sketch110
  ReferenceAxis = -> Sketch110 [N_Axis]
  Refine = true
  Suppressed = false
  Type = 0
FEATURE [PartDesign::SubtractivePipe] SubtractivePipe
  AuxilleryCurvelinear = true
  AuxillerySpineTangent = false
  BaseFeature = -> Pocket003
  Binormal = (0,0,0)
  Mode = 0
  Profile = -> Sketch106
  Refine = true
  Spine = -> Pad008 [Edge215]
  SpineTangent = false
  Suppressed = false
  Transformation = 0
  Transition = 0
FEATURE [PartDesign::SubtractivePipe] SubtractivePipe001
  AuxilleryCurvelinear = true
  AuxillerySpineTangent = false
  BaseFeature = -> SubtractivePipe
  Binormal = (0,0,0)
  Mode = 0
  Profile = -> Sketch107
  Refine = true
  Spine = -> Pad008 [Edge213,Edge216,Edge210]
  SpineTangent = false
  Suppressed = false
  Transformation = 0
  Transition = 0
FEATURE [PartDesign::SubtractiveLoft] SubtractiveLoft
  BaseFeature = -> SubtractivePipe001
  Closed = false
  Profile = -> Sketch099
  Refine = true
  Ruled = false
  Sections = -> [Sketch108]
  Suppressed = false
FEATURE [PartDesign::SubtractiveLoft] SubtractiveLoft001
  BaseFeature = -> SubtractiveLoft
  Closed = false
  Profile = -> Clone2D
  Refine = true
  Ruled = false
  Sections = -> [Sketch109]
  Suppressed = false
FEATURE [Sketcher::SketchObject] Sketch112
  ArcFitTolerance = 1e-06
  AttachmentSupport = -> [Pad008]
  ExternalGeometry = -> [Binder]
  FullyConstrained = true
  MakeInternals = false
  MapMode = 5
  Placement = pos=(0,3.6,0) rot=(0,0.707107,0.707107;3.14159rad)
  sketch-geometry (4):
    g0: LineSegment [constr] StartX=167.782 StartY=-53.0314 StartZ=0 EndX=215.42 EndY=-53.0314 EndZ=0
    g1: GeomPoint [constr] X=191.282 Y=-53.0314 Z=0
    g2: Circle CenterX=191.282 CenterY=-53.0314 CenterZ=0 NormalX=0 NormalY=0 NormalZ=1 AngleXU=0 Radius=11.5
    g3: Circle CenterX=191.282 CenterY=-53.0314 CenterZ=0 NormalX=0 NormalY=0 NormalZ=1 AngleXU=0 Radius=10.7
  constraints (9):
    c: Horizontal(g0)
    c: PointOnObject(g0,g-3)
    c: Diameter(g2) = 23
    c: Coincident(g2,g1)
    c: Diameter(g3) = 21.4
    c: Coincident(g3,g1)
    c: DistanceX(g0,g1) = 23.5
    c: PointOnObject(g1,g0)
    c: Coincident(g0,g-4)
FEATURE [PartDesign::Chamfer] Chamfer016
  Angle = 45
  Base = -> SubtractiveLoft001 [Edge118,Edge117,Edge119,Edge120,Edge109]
  BaseFeature = -> SubtractiveLoft001
  ChamferType = 0
  FlipDirection = false
  Refine = true
  Size = 1.5
  Size2 = 1
  SupportTransform = false
  Suppressed = false
  UseAllEdges = false
FEATURE [PartDesign::Chamfer] Chamfer017
  Angle = 45
  Base = -> Chamfer016 [Edge15]
  BaseFeature = -> Chamfer016
  ChamferType = 0
  FlipDirection = false
  Refine = true
  Size = 1.6
  Size2 = 1
  SupportTransform = false
  Suppressed = false
  UseAllEdges = false
FEATURE [PartDesign::Chamfer] Chamfer018
  Angle = 45
  Base = -> Chamfer017 [Edge10]
  BaseFeature = -> Chamfer017
  ChamferType = 0
  FlipDirection = false
  Refine = true
  Size = 3.5
  Size2 = 1
  SupportTransform = false
  Suppressed = false
  UseAllEdges = false
FEATURE [PartDesign::Chamfer] Chamfer019
  Angle = 45
  Base = -> Chamfer018 [Edge94,Edge199]
  BaseFeature = -> Chamfer018
  ChamferType = 0
  FlipDirection = false
  Refine = true
  Size = 1.9
  Size2 = 1
  SupportTransform = false
  Suppressed = false
  UseAllEdges = false
FEATURE [PartDesign::Fillet] Fillet009
  Base = -> Chamfer019 [Edge83]
  BaseFeature = -> Chamfer019
  Radius = 1.1
  Refine = true
  SupportTransform = false
  Suppressed = false
  UseAllEdges = false
FEATURE [PartDesign::Fillet] Fillet010
  Base = -> Fillet009 [Edge77]
  BaseFeature = -> Fillet009
  Radius = 1.9
  Refine = true
  SupportTransform = false
  Suppressed = false
  UseAllEdges = false
FEATURE [PartDesign::Pocket] Pocket005
  BaseFeature = -> Fillet010
  Direction = (0,-1,2e-16)
  Length = 0.8
  Length2 = 5
  Profile = -> Sketch112
  ReferenceAxis = -> Sketch112 [N_Axis]
  Refine = true
  Suppressed = false
  Type = 0
FEATURE [Part::Part2DObjectPython] ShapeString001  # Draft 2D object (typed FeaturePython)
  FontFile = <path>
  Fuse = false
  Justification = 6
  JustificationReference = 0
  KeepLeftMargin = false
  MakeFace = true
  ObliqueAngle = 0
  Placement = pos=(-183.5,3.6,-57.5) rot=(0,0.707107,0.707107;3.14159rad)
  ScaleToSize = true
  Size = 10
  String = AS
  Tracking = 0
FEATURE [PartDesign::Pocket] Pocket013
  BaseFeature = -> Pocket005
  Direction = (-1e-16,-1,2e-16)
  Length = 1
  Length2 = 5
  Profile = -> ShapeString001
  ReferenceAxis = -> ShapeString001 [N_Axis]
  Refine = true
  Suppressed = false
  Type = 0
FEATURE [PartDesign::Body] Body006  label="lato SX"
  AllowCompound = false
  Group = -> [Binder,Pad019,Chamfer015,Pocket002,Sketch133,Sketch091,Pad005,Sketch092,Pocket001,Sketch093,Sketch094,Pad006,Sketch095,Pad007,Sketch096,Pad008,Sketch097,Pad009,Chamfer005,Pocket004,Sketch098,Pad010,Chamfer006,Pocket003,SubtractivePipe,SubtractivePipe001,Sketch099,Sketch106,Sketch107,Sketch108,Clone2D,Sketch109,SubtractiveLoft,SubtractiveLoft001,Sketch110,Sketch111,Sketch112,Chamfer016,Chamfer017,+7 more]
  Origin = -> Origin006
  Tip = -> Pocket013
FEATURE [PartDesign::Pad] Pad020
  Direction = (0,-1,2e-16)
  Length = 25.2
  Length2 = 10
  Midplane = true
  Placement = pos=(0,0,0) rot=(1,0,0;1.5708rad)
  Profile = -> Sketch021
  ReferenceAxis = -> Sketch021 [N_Axis]
  Refine = true
  Suppressed = false
  Type = 0
FEATURE [PartDesign::Body] Body001  label="perno fermo rumble e driver solenoide"
  AllowCompound = false
  Group = -> [Sketch021,Pad020]
  Origin = -> Origin001
  Tip = -> Pad020
FEATURE [PartDesign::Pad] Pad021
  Direction = (0,-1,2e-16)
  Length = 16.8
  Length2 = 10
  Midplane = true
  Placement = pos=(0,0,0) rot=(1,0,0;1.5708rad)
  Profile = -> Sketch061
  ReferenceAxis = -> Sketch061 [N_Axis]
  Refine = true
  Suppressed = false
  Type = 0
FEATURE [PartDesign::Pocket] Pocket014
  BaseFeature = -> Pad021
  Direction = (0,1,-2e-16)
  Length = 12.8
  Length2 = 5
  Midplane = true
  Placement = pos=(0,0,0) rot=(1,0,0;1.5708rad)
  Profile = -> Sketch062
  ReferenceAxis = -> Sketch062 [N_Axis]
  Refine = true
  Suppressed = false
  Type = 0
FEATURE [PartDesign::Pad] Pad022
  BaseFeature = -> Pocket014
  Direction = (0,-1,2e-16)
  Length = 7.6
  Length2 = 10
  Midplane = true
  Placement = pos=(0,0,0) rot=(1,0,0;1.5708rad)
  Profile = -> Sketch063
  ReferenceAxis = -> Sketch063 [N_Axis]
  Refine = true
  Suppressed = false
  Type = 0
FEATURE [PartDesign::Body] Body003  label="blocco switch"
  AllowCompound = false
  Group = -> [Sketch061,Sketch062,Sketch063,Pad021,Pocket014,Pad022]
  Origin = -> Origin003
  Tip = -> Pad022
FEATURE [PartDesign::Pad] Pad024
  Direction = (0,-1,2e-16)
  Length = 17
  Length2 = 10
  Midplane = true
  Placement = pos=(0,0,0) rot=(1,0,0;1.5708rad)
  Profile = -> Sketch045
  ReferenceAxis = -> Sketch045 [N_Axis]
  Refine = true
  Suppressed = false
  Type = 0
FEATURE [PartDesign::Pocket] Pocket015
  BaseFeature = -> Pad024
  Direction = (-1,0,0)
  Length = 8
  Length2 = 5
  Placement = pos=(0,0,0) rot=(1,0,0;1.5708rad)
  Profile = -> Sketch047
  ReferenceAxis = -> Sketch047 [N_Axis]
  Refine = true
  Reversed = true
  Suppressed = false
  Type = 0
FEATURE [PartDesign::Pocket] Pocket016
  BaseFeature = -> Pocket015
  Direction = (-1,0,0)
  Length = 1
  Length2 = 5
  Placement = pos=(0,0,0) rot=(1,0,0;1.5708rad)
  Profile = -> Sketch046
  ReferenceAxis = -> Sketch046 [N_Axis]
  Refine = true
  Reversed = true
  Suppressed = false
  Type = 0
FEATURE [PartDesign::Pocket] Pocket017
  BaseFeature = -> Pocket016
  Direction = (0,1,-2e-16)
  Length = 17
  Length2 = 5
  Midplane = true
  Placement = pos=(0,0,0) rot=(1,0,0;1.5708rad)
  Profile = -> Sketch048
  ReferenceAxis = -> Sketch048 [N_Axis]
  Refine = true
  Suppressed = false
  Type = 0
FEATURE [PartDesign::Pad] Pad025
  BaseFeature = -> Pocket017
  Direction = (0,-1,2e-16)
  Length = 17
  Length2 = 10
  Midplane = true
  Placement = pos=(0,0,0) rot=(1,0,0;1.5708rad)
  Profile = -> Sketch049
  ReferenceAxis = -> Sketch049 [N_Axis]
  Refine = true
  Suppressed = false
  Type = 0
FEATURE [PartDesign::Pad] Pad026
  BaseFeature = -> Pad025
  Direction = (0,-1,2e-16)
  Length = 17
  Length2 = 10
  Midplane = true
  Placement = pos=(0,0,0) rot=(1,0,0;1.5708rad)
  Profile = -> Sketch066
  ReferenceAxis = -> Sketch066 [N_Axis]
  Refine = true
  Suppressed = false
  Type = 0
FEATURE [PartDesign::Pad] Pad027
  BaseFeature = -> Pad026
  Direction = (0,-1,2e-16)
  Length = 5
  Length2 = 10
  Midplane = true
  Placement = pos=(0,0,0) rot=(1,0,0;1.5708rad)
  Profile = -> Sketch064
  ReferenceAxis = -> Sketch064 [N_Axis]
  Refine = true
  Suppressed = false
  Type = 0
FEATURE [PartDesign::Pad] Pad028
  BaseFeature = -> Pad027
  Direction = (1,0,0)
  Length = 1
  Length2 = 10
  Placement = pos=(0,0,0) rot=(1,0,0;1.5708rad)
  Profile = -> Sketch068
  ReferenceAxis = -> Sketch068 [N_Axis]
  Refine = true
  Reversed = true
  Suppressed = false
  Type = 0
FEATURE [PartDesign::Chamfer] Chamfer020
  Angle = 45
  Base = -> Pad028 [Edge73,Edge75,Edge78,Edge77]
  BaseFeature = -> Pad028
  ChamferType = 0
  FlipDirection = false
  Placement = pos=(0,0,0) rot=(1,0,0;1.5708rad)
  Refine = true
  Size = 0.5
  Size2 = 1
  SupportTransform = false
  Suppressed = false
  UseAllEdges = false
FEATURE [PartDesign::Body] Body002  label="supporto per neopixel"
  AllowCompound = false
  Group = -> [Sketch045,Sketch047,Sketch046,Sketch048,Sketch049,Sketch066,Sketch064,Sketch068,Pad024,Pocket015,Pocket016,Pocket017,Pad025,Pad026,Pad027,Pad028,Chamfer020]
  Origin = -> Origin002
  Tip = -> Chamfer020
FEATURE [Sketcher::SketchObject] Sketch134  label="perno fermo rumble002"
  ArcFitTolerance = 1e-06
  AttachmentSupport = -> [XZ_Plane008]
  FullyConstrained = true
  MakeInternals = false
  MapMode = 5
  Placement = pos=(0,0,0) rot=(1,0,0;1.5708rad)
  sketch-geometry (16):
    g0: LineSegment StartX=0 StartY=0.45 StartZ=0 EndX=0 EndY=1.55 EndZ=0
    g1: LineSegment StartX=0.45 StartY=2 StartZ=0 EndX=1.55 EndY=2 EndZ=0
    g2: LineSegment StartX=2 StartY=1.55 StartZ=0 EndX=2 EndY=0.45 EndZ=0
    g3: LineSegment StartX=1.55 StartY=0 StartZ=0 EndX=0.45 EndY=0 EndZ=0
    g4: ArcOfCircle [constr] CenterX=0.45 CenterY=1.55 CenterZ=0 NormalX=0 NormalY=0 NormalZ=1 AngleXU=0 Radius=0.45 StartAngle=1.5708 EndAngle=3.14159
    g5: GeomPoint [constr] X=0 Y=2 Z=0
    g6: LineSegment StartX=0.45 StartY=2 StartZ=0 EndX=0 EndY=1.55 EndZ=0
    g7: ArcOfCircle [constr] CenterX=1.55 CenterY=1.55 CenterZ=0 NormalX=0 NormalY=0 NormalZ=1 AngleXU=0 Radius=0.45 StartAngle=0 EndAngle=1.5708
    g8: GeomPoint [constr] X=2 Y=2 Z=0
    g9: LineSegment StartX=2 StartY=1.55 StartZ=0 EndX=1.55 EndY=2 EndZ=0
    g10: ArcOfCircle [constr] CenterX=1.55 CenterY=0.45 CenterZ=0 NormalX=0 NormalY=0 NormalZ=1 AngleXU=0 Radius=0.45 StartAngle=4.71239 EndAngle=6.28319
    g11: GeomPoint [constr] X=2 Y=0 Z=0
    g12: LineSegment StartX=1.55 StartY=0 StartZ=0 EndX=2 EndY=0.45 EndZ=0
    g13: ArcOfCircle [constr] CenterX=0.45 CenterY=0.45 CenterZ=0 NormalX=0 NormalY=0 NormalZ=1 AngleXU=0 Radius=0.45 StartAngle=3.14159 EndAngle=4.71239
    g14: GeomPoint [constr] X=0 Y=0 Z=0
    g15: LineSegment StartX=0 StartY=0.45 StartZ=0 EndX=0.45 EndY=0 EndZ=0
  constraints (35):
    c: Coincident(g14,g-1)
    c: PointOnObject(g5,g-2)
    c: Horizontal(g1)
    c: Vertical(g2)
    c: Horizontal(g3)
    c: DistanceX(g5,g8) = 2
    c: DistanceY(g11,g8) = 2
    c: PointOnObject(g5,g0)
    c: PointOnObject(g5,g1)
    c: Tangent(g0,g4) = 1.5708
    c: Tangent(g1,g4) = 1.5708
    c: Coincident(g6,g0)
    c: Coincident(g6,g1)
    c: PointOnObject(g8,g2)
    c: PointOnObject(g8,g1)
    c: Tangent(g2,g7) = 1.5708
    c: Tangent(g1,g7) = 1.5708
    c: Coincident(g9,g2)
    c: Coincident(g9,g1)
    c: PointOnObject(g11,g2)
    c: PointOnObject(g11,g3)
    c: Tangent(g2,g10) = 1.5708
    c: Tangent(g3,g10) = 1.5708
    c: Coincident(g12,g2)
    c: Coincident(g12,g3)
    c: PointOnObject(g14,g0)
    c: PointOnObject(g14,g3)
    c: Tangent(g0,g13) = 1.5708
    c: Tangent(g3,g13) = 1.5708
    c: Coincident(g15,g0)
    c: Coincident(g15,g3)
    c: Equal(g6,g9)
    c: Equal(g9,g12)
    c: Equal(g12,g15)
    c: DistanceX(g14,g3) = 0.45
FEATURE [PartDesign::Pad] Pad029
  Direction = (0,-1,2e-16)
  Length = 17
  Length2 = 10
  Midplane = true
  Placement = pos=(0,0,0) rot=(1,0,0;1.5708rad)
  Profile = -> Sketch134
  ReferenceAxis = -> Sketch134 [N_Axis]
  Refine = true
  Suppressed = false
  Type = 0
FEATURE [PartDesign::Body] Body008  label="perno fermo neopixel"
  AllowCompound = false
  Group = -> [Sketch134,Pad029]
  Origin = -> Origin008
  Tip = -> Pad029
FEATURE [Sketcher::SketchObject] Sketch135  label="perno fermo rumble003"
  ArcFitTolerance = 1e-06
  AttachmentSupport = -> [XZ_Plane009]
  FullyConstrained = true
  MakeInternals = false
  MapMode = 5
  Placement = pos=(0,0,0) rot=(1,0,0;1.5708rad)
  sketch-geometry (16):
    g0: LineSegment StartX=4.69e-14 StartY=0.8 StartZ=0 EndX=-3.04e-14 EndY=3.1 EndZ=0
    g1: LineSegment StartX=0.8 StartY=3.9 StartZ=0 EndX=3.1 EndY=3.9 EndZ=0
    g2: LineSegment StartX=3.9 StartY=3.1 StartZ=0 EndX=3.9 EndY=0.8 EndZ=0
    g3: LineSegment StartX=3.1 StartY=0 StartZ=0 EndX=0.8 EndY=0 EndZ=0
    g4: ArcOfCircle [constr] CenterX=0.8 CenterY=3.1 CenterZ=0 NormalX=0 NormalY=0 NormalZ=1 AngleXU=0 Radius=0.8 StartAngle=1.5708 EndAngle=3.14159
    g5: GeomPoint [constr] X=0 Y=3.9 Z=0
    g6: LineSegment StartX=0.8 StartY=3.9 StartZ=0 EndX=-3.04e-14 EndY=3.1 EndZ=0
    g7: ArcOfCircle [constr] CenterX=3.1 CenterY=3.1 CenterZ=0 NormalX=0 NormalY=0 NormalZ=1 AngleXU=0 Radius=0.8 StartAngle=-2.4e-14 EndAngle=1.5708
    g8: GeomPoint [constr] X=3.9 Y=3.9 Z=0
    g9: LineSegment StartX=3.9 StartY=3.1 StartZ=0 EndX=3.1 EndY=3.9 EndZ=0
    g10: ArcOfCircle [constr] CenterX=3.1 CenterY=0.8 CenterZ=0 NormalX=0 NormalY=0 NormalZ=1 AngleXU=0 Radius=0.8 StartAngle=4.71239 EndAngle=6.28319
    g11: GeomPoint [constr] X=3.9 Y=0 Z=0
    g12: LineSegment StartX=3.1 StartY=0 StartZ=0 EndX=3.9 EndY=0.8 EndZ=0
    g13: ArcOfCircle [constr] CenterX=0.8 CenterY=0.8 CenterZ=0 NormalX=0 NormalY=0 NormalZ=1 AngleXU=0 Radius=0.8 StartAngle=3.14159 EndAngle=4.71239
    g14: GeomPoint [constr] X=0 Y=0 Z=0
    g15: LineSegment StartX=4.69e-14 StartY=0.8 StartZ=0 EndX=0.8 EndY=0 EndZ=0
  constraints (35):
    c: Coincident(g14,g-1)
    c: PointOnObject(g5,g-2)
    c: Horizontal(g1)
    c: Vertical(g2)
    c: Horizontal(g3)
    c: DistanceX(g5,g8) = 3.9
    c: DistanceY(g11,g8) = 3.9
    c: PointOnObject(g5,g0)
    c: PointOnObject(g5,g1)
    c: Tangent(g0,g4) = 1.5708
    c: Tangent(g1,g4) = 1.5708
    c: Coincident(g6,g0)
    c: Coincident(g6,g1)
    c: PointOnObject(g8,g2)
    c: PointOnObject(g8,g1)
    c: Tangent(g2,g7) = 1.5708
    c: Tangent(g1,g7) = 1.5708
    c: Coincident(g9,g2)
    c: Coincident(g9,g1)
    c: PointOnObject(g11,g2)
    c: PointOnObject(g11,g3)
    c: Tangent(g2,g10) = 1.5708
    c: Tangent(g3,g10) = 1.5708
    c: Coincident(g12,g2)
    c: Coincident(g12,g3)
    c: PointOnObject(g14,g0)
    c: PointOnObject(g14,g3)
    c: Tangent(g0,g13) = 1.5708
    c: Tangent(g3,g13) = 1.5708
    c: Coincident(g15,g0)
    c: Coincident(g15,g3)
    c: Equal(g6,g9)
    c: Equal(g9,g12)
    c: Equal(g12,g15)
    c: DistanceX(g14,g3) = 0.8
FEATURE [PartDesign::Pad] Pad030
  Direction = (0,-1,2e-16)
  Length = 25.2
  Length2 = 10
  Midplane = true
  Placement = pos=(0,0,0) rot=(1,0,0;1.5708rad)
  Profile = -> Sketch135
  ReferenceAxis = -> Sketch135 [N_Axis]
  Refine = true
  Suppressed = false
  Type = 0
FEATURE [PartDesign::Body] Body009  label="perno fermo switch - caricabatterie - grilletto"
  AllowCompound = false
  Group = -> [Sketch135,Pad030]
  Origin = -> Origin009
  Tip = -> Pad030
FEATURE [Sketcher::SketchObject] Sketch136  label="scavo_rele"
  ArcFitTolerance = 1e-06
  AttachmentSupport = -> [XZ_Plane]
  ExternalGeometry = -> [Sketch]
  FullyConstrained = true
  MakeInternals = false
  MapMode = 5
  Placement = pos=(0,0,0) rot=(1,0,0;1.5708rad)
  sketch-geometry (7):
    g0: LineSegment [constr] StartX=-173.013 StartY=-62.644 StartZ=0 EndX=-176.535 EndY=-73.4861 EndZ=0
    g1: LineSegment [constr] StartX=-173.013 StartY=-62.644 StartZ=0 EndX=-170.35 EndY=-63.5093 EndZ=0
    g2: LineSegment [constr] StartX=-173.013 StartY=-62.644 StartZ=0 EndX=-176.627 EndY=-61.4698 EndZ=0
    g3: LineSegment StartX=-176.627 StartY=-61.4698 StartZ=0 EndX=-170.35 EndY=-63.5093 EndZ=0
    g4: LineSegment StartX=-176.627 StartY=-61.4698 StartZ=0 EndX=-180.149 EndY=-72.3118 EndZ=0
    g5: LineSegment StartX=-170.35 StartY=-63.5093 StartZ=0 EndX=-173.872 EndY=-74.3513 EndZ=0
    g6: LineSegment StartX=-180.149 StartY=-72.3118 StartZ=0 EndX=-173.872 EndY=-74.3513 EndZ=0
  constraints (19):
    c: Tangent(g0,g-3)
    c: Distance(g0,g-3) = 89
    c: Distance(g0,g0) = 11.4
    c: Coincident(g1,g0)
    c: Coincident(g2,g0)
    c: Distance(g2) = 3.8
    c: Distance(g1) = 2.8
    c: Perpendicular(g0,g1)
    c: Perpendicular(g0,g2)
    c: Coincident(g3,g2)
    c: Coincident(g3,g1)
    c: Equal(g4,g0)
    c: Equal(g5,g0)
    c: Parallel(g4,g0)
    c: Parallel(g5,g0)
    c: Coincident(g4,g2)
    c: Coincident(g5,g1)
    c: Coincident(g6,g4)
    c: Coincident(g6,g5)
FEATURE [Part::Extrusion] Extrude076  label="Extrude076 - scavo_rele"
  Base = -> Sketch136
  Dir = (0,-1,2e-16)
  DirMode = 2
  FaceMakerClass = Part::FaceMakerBullseye
  FaceMakerMode = 3
  LengthFwd = 17.8
  LengthRev = 0
  Solid = true
  Symmetric = true
FEATURE [Sketcher::SketchObject] Sketch137  label="scavo_nuovo_driver"
  ArcFitTolerance = 1e-06
  AttachmentSupport = -> [XZ_Plane]
  ExternalGeometry = -> [Sketch]
  FullyConstrained = true
  MakeInternals = false
  MapMode = 5
  Placement = pos=(0,0,0) rot=(1,0,0;1.5708rad)
  sketch-geometry (7):
    g0: LineSegment [constr] StartX=-167.759 StartY=-46.4761 StartZ=0 EndX=-172.58 EndY=-61.3126 EndZ=0
    g1: LineSegment [constr] StartX=-167.759 StartY=-46.4761 StartZ=0 EndX=-165.477 EndY=-47.2177 EndZ=0
    g2: LineSegment [constr] StartX=-167.759 StartY=-46.4761 StartZ=0 EndX=-171.373 EndY=-45.3018 EndZ=0
    g3: LineSegment StartX=-171.373 StartY=-45.3018 StartZ=0 EndX=-165.477 EndY=-47.2177 EndZ=0
    g4: LineSegment StartX=-171.373 StartY=-45.3018 StartZ=0 EndX=-176.194 EndY=-60.1383 EndZ=0
    g5: LineSegment StartX=-165.477 StartY=-47.2177 StartZ=0 EndX=-170.297 EndY=-62.0542 EndZ=0
    g6: LineSegment StartX=-176.194 StartY=-60.1383 StartZ=0 EndX=-170.297 EndY=-62.0542 EndZ=0
  constraints (19):
    c: Distance(g0,g-3) = 72
    c: Distance(g0) = 15.6
    c: Tangent(g0,g-3)
    c: Coincident(g1,g0)
    c: Coincident(g2,g0)
    c: Distance(g1) = 2.4
    c: Distance(g2) = 3.8
    c: Perpendicular(g0,g1)
    c: Perpendicular(g0,g2)
    c: Coincident(g3,g2)
    c: Coincident(g3,g1)
    c: Equal(g4,g0)
    c: Equal(g5,g0)
    c: Parallel(g4,g0)
    c: Parallel(g5,g0)
    c: Coincident(g4,g2)
    c: Coincident(g5,g1)
    c: Coincident(g6,g4)
    c: Coincident(g6,g5)
FEATURE [Part::Extrusion] Extrude077  label="Extrude077 - scavo_nuovo_driver"
  Base = -> Sketch137
  Dir = (0,-1,2e-16)
  DirMode = 2
  FaceMakerClass = Part::FaceMakerBullseye
  FaceMakerMode = 3
  LengthFwd = 20.8
  LengthRev = 0
  Solid = true
  Symmetric = true
FEATURE [Sketcher::SketchObject] Sketch138  label="scavo_nuovo_driver_alto"
  ArcFitTolerance = 1e-06
  AttachmentSupport = -> [XZ_Plane]
  ExternalGeometry = -> [Sketch]
  FullyConstrained = true
  MakeInternals = false
  MapMode = 5
  Placement = pos=(0,0,0) rot=(1,0,0;1.5708rad)
  sketch-geometry (7):
    g0: LineSegment [constr] StartX=-188.796 StartY=17.7274 StartZ=0 EndX=-187.75 EndY=4.97025 EndZ=0
    g1: LineSegment StartX=-187.75 StartY=4.97025 StartZ=0 EndX=-189.743 EndY=4.8067 EndZ=0
    g2: LineSegment StartX=-187.75 StartY=4.97025 StartZ=0 EndX=-182.766 EndY=5.37913 EndZ=0
    g3: LineSegment StartX=-190.79 StartY=17.5638 StartZ=0 EndX=-189.743 EndY=4.8067 EndZ=0
    g4: LineSegment StartX=-183.813 StartY=18.1363 StartZ=0 EndX=-182.766 EndY=5.37913 EndZ=0
    g5: LineSegment StartX=-190.79 StartY=17.5638 StartZ=0 EndX=-188.796 EndY=17.7274 EndZ=0
    g6: LineSegment StartX=-188.796 StartY=17.7274 StartZ=0 EndX=-183.813 EndY=18.1363 EndZ=0
  constraints (20):
    c: Distance(g0) = 12.8
    c: DistanceY(g-3,g0) = 9
    c: PointOnObject(g0,g-4)
    c: PointOnObject(g0,g-4)
    c: Coincident(g1,g0)
    c: Coincident(g2,g0)
    c: Distance(g1) = 2
    c: Distance(g2) = 5
    c: Perpendicular(g0,g1)
    c: Perpendicular(g0,g2)
    c: Equal(g3,g0)
    c: Parallel(g3,g0)
    c: Coincident(g3,g1)
    c: Equal(g4,g0)
    c: Parallel(g4,g0)
    c: Coincident(g4,g2)
    c: Coincident(g5,g3)
    c: Coincident(g5,g0)
    c: Coincident(g6,g0)
    c: Coincident(g6,g4)
FEATURE [Part::Extrusion] Extrude078  label="Extrude078 - scavo_nuovo_driver_alto"
  Base = -> Sketch138
  Dir = (0,-1,2e-16)
  DirMode = 2
  FaceMakerClass = Part::FaceMakerBullseye
  FaceMakerMode = 3
  LengthFwd = 16.6
  LengthRev = 0
  Solid = true
  Symmetric = true
FEATURE [Sketcher::SketchObject] Sketch139  label="fermi_nuovo_driver_alto"
  ArcFitTolerance = 1e-06
  AttachmentSupport = -> [XZ_Plane]
  ExternalGeometry = -> [Sketch138,Sketch]
  FullyConstrained = true
  MakeInternals = false
  MapMode = 5
  Placement = pos=(0,0,0) rot=(1,0,0;1.5708rad)
  sketch-geometry (17):
    g0: LineSegment [constr] StartX=-188.314 StartY=16.4295 StartZ=0 EndX=-187.885 EndY=13.7638 EndZ=0
    g1: LineSegment [constr] StartX=-187.885 StartY=13.7638 StartZ=0 EndX=-187.456 EndY=11.0981 EndZ=0
    g2: LineSegment StartX=-187.885 StartY=13.7638 StartZ=0 EndX=-187.71 EndY=12.6778 EndZ=0
    g3: LineSegment StartX=-187.885 StartY=13.7638 StartZ=0 EndX=-188.06 EndY=14.8499 EndZ=0
    g4: LineSegment StartX=-187.71 StartY=12.6778 StartZ=0 EndX=-185.538 EndY=13.0274 EndZ=0
    g5: LineSegment StartX=-188.06 StartY=14.8499 StartZ=0 EndX=-185.888 EndY=15.1994 EndZ=0
    g6: LineSegment StartX=-185.888 StartY=15.1994 StartZ=0 EndX=-185.538 EndY=13.0274 EndZ=0
    g7: LineSegment StartX=-187.456 StartY=11.0981 StartZ=0 EndX=-189.035 EndY=10.8439 EndZ=0
    g8: LineSegment StartX=-188.314 StartY=16.4295 StartZ=0 EndX=-189.893 EndY=16.1753 EndZ=0
    g9: LineSegment StartX=-189.893 StartY=16.1753 StartZ=0 EndX=-189.035 EndY=10.8439 EndZ=0
    g10: LineSegment StartX=-187.456 StartY=11.0981 StartZ=0 EndX=-185.284 EndY=11.4477 EndZ=0
    g11: LineSegment StartX=-188.314 StartY=16.4295 StartZ=0 EndX=-186.142 EndY=16.7791 EndZ=0
    g12: LineSegment StartX=-184.308 StartY=15.4537 StartZ=0 EndX=-183.958 EndY=13.2816 EndZ=0
    g13: ArcOfCircle CenterX=-185.888 CenterY=15.1994 CenterZ=0 NormalX=0 NormalY=0 NormalZ=1 AngleXU=0 Radius=1.6 StartAngle=0.15957 EndAngle=1.73037
    g14: GeomPoint [constr] X=-184.562 Y=17.0333 Z=0
    g15: ArcOfCircle CenterX=-185.538 CenterY=13.0274 CenterZ=0 NormalX=0 NormalY=0 NormalZ=1 AngleXU=0 Radius=1.6 StartAngle=4.87196 EndAngle=6.44276
    g16: GeomPoint [constr] X=-183.704 Y=11.7019 Z=0
  constraints (43):
    c: Tangent(g1,g0) = -1.5708
    c: Distance(g0) = 2.7
    c: Equal(g1,g0)
    c: Tangent(g1,g-5)
    c: Coincident(g2,g0)
    c: Coincident(g3,g0)
    c: Distance(g2) = 1.1
    c: Equal(g3,g2)
    c: PointOnObject(g3,g2)
    c: Coincident(g4,g2)
    c: Coincident(g5,g3)
    c: Distance(g4) = 2.2
    c: Equal(g4,g5)
    c: Perpendicular(g1,g4)
    c: Perpendicular(g0,g5)
    c: Coincident(g6,g5)
    c: Coincident(g6,g4)
    c: Coincident(g7,g1)
    c: Coincident(g8,g0)
    c: Distance(g7) = 1.6
    c: Equal(g7,g8)
    c: Perpendicular(g1,g7)
    c: Perpendicular(g8,g0)
    c: Coincident(g9,g8)
    c: Coincident(g9,g7)
    c: Coincident(g10,g1)
    c: Coincident(g11,g0)
    c: Distance(g10,g16) = 3.8
    c: Perpendicular(g1,g10)
    c: Perpendicular(g1,g11)
    c: DistanceY(g0,g-4) = 3.8
    c: PointOnObject(g14,g12)
    c: PointOnObject(g14,g11)
    c: Tangent(g12,g13) = 1.5708
    c: Tangent(g11,g13) = 1.5708
    c: PointOnObject(g16,g12)
    c: PointOnObject(g16,g10)
    c: Tangent(g12,g15) = 1.5708
    c: Tangent(g10,g15) = -1.5708
    c: Equal(g13,g15)
    c: Coincident(g13,g5)
    c: Parallel(g2,g0)
    c: PointOnObject(g0,g-5)
FEATURE [Part::Extrusion] Extrude079  label="Extrude079 - fermi_nuovo_driver_alto"
  Base = -> Sketch139
  Dir = (0,-1,2e-16)
  DirMode = 2
  FaceMakerClass = Part::FaceMakerBullseye
  FaceMakerMode = 3
  LengthFwd = 25.2
  LengthRev = 0
  Solid = true
  Symmetric = true
FEATURE [Sketcher::SketchObject] Sketch140  label="scavo_diodo_nuovo_driver_alto"
  ArcFitTolerance = 1e-06
  AttachmentSupport = -> [XZ_Plane]
  ExternalGeometry = -> [Sketch138]
  FullyConstrained = true
  MakeInternals = false
  MapMode = 5
  Placement = pos=(0,0,0) rot=(1,0,0;1.5708rad)
  sketch-geometry (4):
    g0: LineSegment StartX=-190.79 StartY=17.5638 StartZ=0 EndX=-189.743 EndY=4.8067 EndZ=0
    g1: LineSegment StartX=-193.78 StartY=17.3185 StartZ=0 EndX=-192.733 EndY=4.56137 EndZ=0
    g2: LineSegment StartX=-190.79 StartY=17.5638 StartZ=0 EndX=-193.78 EndY=17.3185 EndZ=0
    g3: LineSegment StartX=-192.733 StartY=4.56137 StartZ=0 EndX=-189.743 EndY=4.8067 EndZ=0
  constraints (11):
    c: Equal(g0,g-3)
    c: Parallel(g0,g-3)
    c: Equal(g1,g-3)
    c: Parallel(g1,g-3)
    c: Coincident(g2,g0)
    c: Distance(g2) = 3
    c: Perpendicular(g0,g2)
    c: Coincident(g1,g2)
    c: Coincident(g3,g1)
    c: Coincident(g3,g0)
    c: Coincident(g0,g-3)
FEATURE [Part::Extrusion] Extrude080  label="Extrude080 - scavo_diodo_nuovo_driver_alto"
  Base = -> Sketch140
  Dir = (0,-1,2e-16)
  DirMode = 2
  FaceMakerClass = Part::FaceMakerBullseye
  FaceMakerMode = 3
  LengthFwd = 4
  LengthRev = 0
  Placement = pos=(0,7.8,0) rot=(0,0,1;0rad)
  Solid = true
  Symmetric = false
FEATURE [Part::MultiFuse] Fusion001
  Refine = true
  Shapes = -> [Cut043,Extrude079]
FEATURE [Part::Cut] Cut044
  Base = -> Fusion001
  Refine = true
  Tool = -> Extrude078
FEATURE [Part::Cut] Cut045
  Base = -> Cut044
  Refine = true
  Tool = -> Extrude080
FEATURE [Sketcher::SketchObject] Sketch141  label="fermi_nuovo_driver"
  ArcFitTolerance = 1e-06
  AttachmentSupport = -> [XZ_Plane]
  ExternalGeometry = -> [Sketch,Sketch137]
  FullyConstrained = true
  MakeInternals = false
  MapMode = 5
  Placement = pos=(0,0,0) rot=(1,0,0;1.5708rad)
  sketch-geometry (16):
    g0: LineSegment [constr] StartX=-165.477 StartY=-47.2177 StartZ=0 EndX=-167.759 EndY=-46.4761 EndZ=0
    g1: LineSegment [constr] StartX=-167.759 StartY=-46.4761 StartZ=0 EndX=-168.006 EndY=-47.2369 EndZ=0
    g2: LineSegment [constr] StartX=-168.006 StartY=-47.2369 StartZ=0 EndX=-169.675 EndY=-52.3726 EndZ=0
    g3: LineSegment StartX=-169.675 StartY=-52.3726 StartZ=0 EndX=-171.767 EndY=-51.6928 EndZ=0
    g4: LineSegment StartX=-172.795 StartY=-49.6767 StartZ=0 EndX=-172.115 EndY=-47.5843 EndZ=0
    g5: LineSegment StartX=-170.099 StartY=-46.5571 StartZ=0 EndX=-166.485 EndY=-47.7313 EndZ=0
    g6: LineSegment StartX=-166.485 StartY=-47.7313 StartZ=0 EndX=-168.153 EndY=-52.867 EndZ=0
    g7: LineSegment StartX=-169.675 StartY=-52.3726 StartZ=0 EndX=-168.153 EndY=-52.867 EndZ=0
    g8: LineSegment StartX=-170.593 StartY=-48.0788 StartZ=0 EndX=-171.273 EndY=-50.1711 EndZ=0
    g9: LineSegment StartX=-171.273 StartY=-50.1711 StartZ=0 EndX=-169.181 EndY=-50.8509 EndZ=0
    g10: LineSegment StartX=-169.181 StartY=-50.8509 StartZ=0 EndX=-168.501 EndY=-48.7586 EndZ=0
    g11: LineSegment StartX=-168.501 StartY=-48.7586 StartZ=0 EndX=-170.593 EndY=-48.0788 EndZ=0
    g12: ArcOfCircle CenterX=-170.593 CenterY=-48.0788 CenterZ=0 NormalX=0 NormalY=0 NormalZ=1 AngleXU=0 Radius=1.6 StartAngle=1.25664 EndAngle=2.82743
    g13: GeomPoint [constr] X=-171.62 Y=-46.0626 Z=0
    g14: ArcOfCircle CenterX=-171.273 CenterY=-50.1711 CenterZ=0 NormalX=0 NormalY=0 NormalZ=1 AngleXU=0 Radius=1.6 StartAngle=2.82743 EndAngle=4.39823
    g15: GeomPoint [constr] X=-173.289 Y=-51.1984 Z=0
  constraints (41):
    c: Coincident(g0,g-4)
    c: PointOnObject(g0,g-3)
    c: Parallel(g0,g-4)
    c: Coincident(g1,g0)
    c: Parallel(g1,g-3)
    c: Distance(g1) = 0.8
    c: Coincident(g2,g1)
    c: Distance(g2) = 5.4
    c: Coincident(g3,g2)
    c: Parallel(g2,g-3)
    c: Distance(g15,g13) = 5.4
    c: Perpendicular(g3,g2)
    c: Parallel(g4,g2)
    c: Distance(g5,g13) = 5.4
    c: Distance(g3,g15) = 3.8
    c: Perpendicular(g4,g5)
    c: Coincident(g6,g5)
    c: Distance(g6) = 5.4
    c: Parallel(g6,g4)
    c: Coincident(g7,g2)
    c: Coincident(g7,g6)
    c: Coincident(g8,g9)
    c: Coincident(g9,g10)
    c: Coincident(g10,g11)
    c: Coincident(g11,g8)
    c: Distance(g8,g10) = 2.2
    c: Distance(g9,g11) = 2.2
    c: Perpendicular(g11,g8)
    c: Equal(g8,g10)
    c: Equal(g11,g9)
    c: Tangent(g10,g2)
    c: Distance(g10,g1) = 1.6
    c: PointOnObject(g13,g4)
    c: PointOnObject(g13,g5)
    c: Tangent(g4,g12) = 1.5708
    c: Tangent(g5,g12) = 1.5708
    c: PointOnObject(g15,g4)
    c: Tangent(g4,g14) = 1.5708
    c: Tangent(g3,g14) = 1.5708
    c: Equal(g14,g12)
    c: Coincident(g12,g8)
FEATURE [Part::Extrusion] Extrude081  label="Extrude081 - fermi_nuovo_driver"
  Base = -> Sketch141
  Dir = (0,-1,2e-16)
  DirMode = 2
  FaceMakerClass = Part::FaceMakerBullseye
  FaceMakerMode = 3
  LengthFwd = 25.2
  LengthRev = 0
  Solid = true
  Symmetric = true
FEATURE [Part::MultiFuse] Fusion002
  Refine = true
  Shapes = -> [Cut045,Extrude081]
FEATURE [Part::Cut] Cut046
  Base = -> Fusion002
  Refine = true
  Tool = -> Extrude077
FEATURE [Sketcher::SketchObject] Sketch142  label="fermi_rele"
  ArcFitTolerance = 1e-06
  AttachmentSupport = -> [XZ_Plane]
  ExternalGeometry = -> [Sketch,Sketch136]
  FullyConstrained = true
  MakeInternals = false
  MapMode = 5
  Placement = pos=(0,0,0) rot=(1,0,0;1.5708rad)
  sketch-geometry (15):
    g0: LineSegment StartX=-177.245 StartY=-63.3719 StartZ=0 EndX=-177.924 EndY=-65.4642 EndZ=0
    g1: LineSegment StartX=-175.228 StartY=-62.3446 StartZ=0 EndX=-171.614 EndY=-63.5189 EndZ=0
    g2: LineSegment StartX=-171.614 StartY=-63.5189 StartZ=0 EndX=-173.283 EndY=-68.6546 EndZ=0
    g3: LineSegment StartX=-176.897 StartY=-67.4803 StartZ=0 EndX=-173.283 EndY=-68.6546 EndZ=0
    g4: LineSegment StartX=-175.723 StartY=-63.8663 StartZ=0 EndX=-173.631 EndY=-64.5461 EndZ=0
    g5: LineSegment StartX=-175.723 StartY=-63.8663 StartZ=0 EndX=-176.403 EndY=-65.9586 EndZ=0
    g6: LineSegment StartX=-173.631 StartY=-64.5461 StartZ=0 EndX=-174.31 EndY=-66.6385 EndZ=0
    g7: LineSegment StartX=-176.403 StartY=-65.9586 StartZ=0 EndX=-174.31 EndY=-66.6385 EndZ=0
    g8: LineSegment [constr] StartX=-173.631 StartY=-64.5461 StartZ=0 EndX=-173.136 EndY=-63.0245 EndZ=0
    g9: LineSegment [constr] StartX=-173.631 StartY=-64.5461 StartZ=0 EndX=-172.109 EndY=-65.0406 EndZ=0
    g10: LineSegment [constr] StartX=-170.35 StartY=-63.5093 StartZ=0 EndX=-173.013 EndY=-62.644 EndZ=0
    g11: ArcOfCircle CenterX=-175.723 CenterY=-63.8663 CenterZ=0 NormalX=0 NormalY=0 NormalZ=1 AngleXU=0 Radius=1.6 StartAngle=1.25664 EndAngle=2.82743
    g12: GeomPoint [constr] X=-176.75 Y=-61.8502 Z=0
    g13: ArcOfCircle CenterX=-176.403 CenterY=-65.9586 CenterZ=0 NormalX=0 NormalY=0 NormalZ=1 AngleXU=0 Radius=1.6 StartAngle=2.82743 EndAngle=4.39823
    g14: GeomPoint [constr] X=-178.419 Y=-66.9859 Z=0
  constraints (39):
    c: Distance(g14,g12) = 5.4
    c: Distance(g1,g12) = 5.4
    c: Perpendicular(g1,g0)
    c: Coincident(g2,g1)
    c: Parallel(g2,g0)
    c: Coincident(g3,g2)
    c: Parallel(g2,g-3)
    c: Coincident(g5,g4)
    c: Distance(g5) = 2.2
    c: Distance(g4) = 2.2
    c: Perpendicular(g4,g5)
    c: Coincident(g6,g4)
    c: Equal(g6,g5)
    c: Parallel(g6,g5)
    c: Coincident(g7,g5)
    c: Coincident(g7,g6)
    c: Coincident(g8,g4)
    c: Coincident(g9,g4)
    c: Distance(g8) = 1.6
    c: Distance(g9) = 1.6
    c: Parallel(g8,g6)
    c: Parallel(g9,g4)
    c: PointOnObject(g8,g1)
    c: PointOnObject(g9,g2)
    c: Coincident(g10,g-4)
    c: Parallel(g10,g-4)
    c: PointOnObject(g10,g-3)
    c: Tangent(g6,g-3) = 1.5708
    c: Distance(g4,g10) = 2
    c: PointOnObject(g12,g1)
    c: Tangent(g1,g11) = 1.5708
    c: Tangent(g0,g11) = -1.5708
    c: PointOnObject(g14,g3)
    c: PointOnObject(g14,g0)
    c: Tangent(g3,g13) = -1.5708
    c: Tangent(g0,g13) = -1.5708
    c: Equal(g11,g13)
    c: Coincident(g11,g4)
    c: Parallel(g3,g1)
FEATURE [Part::Extrusion] Extrude082  label="Extrude082 - fermi_rele"
  Base = -> Sketch142
  Dir = (0,-1,2e-16)
  DirMode = 2
  FaceMakerClass = Part::FaceMakerBullseye
  FaceMakerMode = 3
  LengthFwd = 25.2
  LengthRev = 0
  Solid = true
  Symmetric = true
FEATURE [Part::MultiFuse] Fusion003
  Refine = true
  Shapes = -> [Cut046,Extrude082]
FEATURE [Part::Cut] Cut047
  Base = -> Fusion003
  Refine = true
  Tool = -> Extrude076
FEATURE [Sketcher::SketchObject] Sketch143  label="foro_passaggio_cavi_led_batteria"
  ArcFitTolerance = 1e-06
  AttachmentSupport = -> [XZ_Plane]
  ExternalGeometry = -> [Sketch,Sketch042,Sketch036]
  FullyConstrained = true
  MakeInternals = false
  MapMode = 5
  Placement = pos=(0,0,0) rot=(1,0,0;1.5708rad)
  sketch-geometry (4):
    g0: LineSegment StartX=-207.775 StartY=-41.3701 StartZ=0 EndX=-213.607 EndY=-53.8767 EndZ=0
    g1: LineSegment StartX=-213.607 StartY=-53.8767 StartZ=0 EndX=-211.843 EndY=-59.5559 EndZ=0
    g2: LineSegment StartX=-207.775 StartY=-41.3701 StartZ=0 EndX=-207.775 EndY=-50.8316 EndZ=0
    g3: LineSegment StartX=-207.775 StartY=-50.8316 StartZ=0 EndX=-211.843 EndY=-59.5559 EndZ=0
  constraints (9):
    c: Coincident(g0,g-3)
    c: PointOnObject(g1,g-6)
    c: Coincident(g1,g0)
    c: Coincident(g2,g0)
    c: Coincident(g2,g-7)
    c: Coincident(g3,g2)
    c: Parallel(g3,g0)
    c: Coincident(g3,g1)
    c: Coincident(g0,g-5)
FEATURE [Part::Extrusion] Extrude083  label="Extrude083 - foro_passaggio_cavi_led_batteria"
  Base = -> Sketch143
  Dir = (0,-1,2e-16)
  DirMode = 2
  FaceMakerClass = Part::FaceMakerBullseye
  FaceMakerMode = 3
  LengthFwd = 6
  LengthRev = 0
  Solid = true
  Symmetric = true
FEATURE [Part::Cut] Cut048
  Base = -> Cut047
  Refine = true
  Tool = -> Extrude083
FEATURE [Sketcher::SketchObject] Sketch144  label="foro_areazione_alimentatore"
  ArcFitTolerance = 1e-06
  AttachmentSupport = -> [XZ_Plane]
  ExternalGeometry = -> [Sketch036]
  FullyConstrained = true
  MakeInternals = false
  MapMode = 5
  Placement = pos=(0,0,0) rot=(1,0,0;1.5708rad)
  sketch-geometry (4):
    g0: LineSegment StartX=-211.843 StartY=-60.3701 StartZ=0 EndX=-207.775 EndY=-60.3701 EndZ=0
    g1: LineSegment StartX=-207.775 StartY=-60.3701 StartZ=0 EndX=-207.775 EndY=-70.3701 EndZ=0
    g2: LineSegment StartX=-211.843 StartY=-60.3701 StartZ=0 EndX=-211.843 EndY=-70.3701 EndZ=0
    g3: LineSegment StartX=-207.775 StartY=-70.3701 StartZ=0 EndX=-211.843 EndY=-70.3701 EndZ=0
  constraints (11):
    c: Horizontal(g0)
    c: Distance(g1) = 10
    c: Coincident(g1,g0)
    c: Tangent(g1,g-3)
    c: PointOnObject(g0,g-4)
    c: Coincident(g2,g0)
    c: PointOnObject(g2,g-4)
    c: Coincident(g3,g1)
    c: Horizontal(g3)
    c: Coincident(g3,g2)
    c: DistanceY(g0,g-3) = 19
FEATURE [Part::Extrusion] Extrude084  label="Extrude084 - foro_areazione_alimentatore"
  Base = -> Sketch144
  Dir = (0,-1,2e-16)
  DirMode = 2
  FaceMakerClass = Part::FaceMakerBullseye
  FaceMakerMode = 3
  LengthFwd = 10
  LengthRev = 0
  Solid = true
  Symmetric = true
FEATURE [Part::Cut] Cut049
  Base = -> Cut048
  Refine = true
  Tool = -> Extrude084
FEATURE [Sketcher::SketchObject] Sketch145  label="foro_per_condesatore"
  ArcFitTolerance = 1e-06
  AttachmentSupport = -> [XZ_Plane]
  ExternalGeometry = -> [Sketch,Sketch139]
  FullyConstrained = true
  MakeInternals = false
  MapMode = 5
  Placement = pos=(0,0,0) rot=(1,0,0;1.5708rad)
  sketch-geometry (1):
    g0: Circle CenterX=-182.345 CenterY=7.02342 CenterZ=0 NormalX=0 NormalY=0 NormalZ=1 AngleXU=0 Radius=5.2
  constraints (3):
    c: Diameter(g0) = 10.4
    c: Tangent(g0,g-3)
    c: Tangent(g0,g-4)
FEATURE [Part::Extrusion] Extrude085  label="Extrude085 - foro_per_condesatore"
  Base = -> Sketch145
  Dir = (0,-1,2e-16)
  DirMode = 2
  FaceMakerClass = Part::FaceMakerBullseye
  FaceMakerMode = 3
  LengthFwd = 25.2
  LengthRev = 0
  Solid = true
  Symmetric = true
FEATURE [Part::Cut] Cut050
  Base = -> Cut049
  Refine = true
  Tool = -> Extrude085
FEATURE [Sketcher::SketchObject] Sketch146  label="scavo_pulsante_6x6_per_led_batteria"
  ArcFitTolerance = 1e-06
  AttachmentSupport = -> [XZ_Plane]
  ExternalGeometry = -> [Sketch036,Sketch016]
  FullyConstrained = true
  MakeInternals = false
  MapMode = 5
  Placement = pos=(0,0,0) rot=(1,0,0;1.5708rad)
  sketch-geometry (4):
    g0: LineSegment StartX=-217.243 StartY=-66.0316 StartZ=0 EndX=-217.243 EndY=-72.8316 EndZ=0
    g1: LineSegment StartX=-217.243 StartY=-72.8316 StartZ=0 EndX=-211.043 EndY=-72.8316 EndZ=0
    g2: LineSegment StartX=-211.043 StartY=-72.8316 StartZ=0 EndX=-211.043 EndY=-66.0316 EndZ=0
    g3: LineSegment StartX=-211.043 StartY=-66.0316 StartZ=0 EndX=-217.243 EndY=-66.0316 EndZ=0
  constraints (12):
    c: Coincident(g0,g1)
    c: Coincident(g1,g2)
    c: Coincident(g2,g3)
    c: Coincident(g3,g0)
    c: Vertical(g0)
    c: Vertical(g2)
    c: Horizontal(g1)
    c: Horizontal(g3)
    c: Distance(g0,g2) = 6.2
    c: Distance(g1,g3) = 6.8
    c: Tangent(g1,g-4)
    c: DistanceX(g-3,g1) = 0.8
FEATURE [Part::Extrusion] Extrude086  label="Extrude086 - scavo_pulsante_6x6_per_led_batteria"
  Base = -> Sketch146
  Dir = (0,-1,2e-16)
  DirMode = 2
  FaceMakerClass = Part::FaceMakerBullseye
  FaceMakerMode = 3
  LengthFwd = 4.2
  LengthRev = 0
  Placement = pos=(0,12.6,0) rot=(0,0,1;0rad)
  Solid = true
  Symmetric = false
FEATURE [Sketcher::SketchObject] Sketch147  label="scavo_led_stato_batteria"
  ArcFitTolerance = 1e-06
  AttachmentSupport = -> [XZ_Plane]
  ExternalGeometry = -> [Sketch036,Sketch146]
  FullyConstrained = true
  MakeInternals = false
  MapMode = 5
  Placement = pos=(0,0,0) rot=(1,0,0;1.5708rad)
  sketch-geometry (4):
    g0: LineSegment StartX=-215.643 StartY=-55.6944 StartZ=0 EndX=-215.643 EndY=-64.8944 EndZ=0
    g1: LineSegment StartX=-215.643 StartY=-64.8944 StartZ=0 EndX=-211.043 EndY=-64.8944 EndZ=0
    g2: LineSegment StartX=-211.043 StartY=-64.8944 StartZ=0 EndX=-211.043 EndY=-55.6944 EndZ=0
    g3: LineSegment StartX=-211.043 StartY=-55.6944 StartZ=0 EndX=-215.643 EndY=-55.6944 EndZ=0
  constraints (12):
    c: Coincident(g0,g1)
    c: Coincident(g1,g2)
    c: Coincident(g2,g3)
    c: Coincident(g3,g0)
    c: Vertical(g0)
    c: Vertical(g2)
    c: Horizontal(g1)
    c: Horizontal(g3)
    c: Distance(g0,g2) = 4.6
    c: Distance(g1,g3) = 9.2
    c: DistanceY(g2,g-3) = 5.6
    c: DistanceX(g2,g-4) = 0
FEATURE [PartDesign::Body] Body  label="Struttura pistola"
  AllowCompound = false
  Group = -> [Sketch,Sketch002,Sketch004,DatumPlane,Sketch005,DatumPlane001,CopyCut,Sketch008,Sketch009,Sketch010,Sketch011,Sketch012,Sketch013,Sketch014,Sketch015,Sketch016,Sketch017,Sketch018,Sketch019,Sketch020,Sketch022,Sketch023,Sketch024,Sketch025,Sketch026,Sketch027,Sketch029,Sketch030,Sketch031,Sketch032,Sketch033,Sketch034,Sketch035,Sketch036,Sketch037,Sketch038,Sketch039,Sketch040,Sketch041,Sketch042,+27 more]
  Origin = -> Origin
FEATURE [Part::Extrusion] Extrude087  label="Extrude087 - scavo_led_stato_batteria"
  Base = -> Sketch147
  Dir = (0,-1,2e-16)
  DirMode = 2
  FaceMakerClass = Part::FaceMakerBullseye
  FaceMakerMode = 3
  LengthFwd = 2
  LengthRev = 0
  Placement = pos=(0,12.6,0) rot=(0,0,1;0rad)
  Solid = true
  Symmetric = false
note: 2 file-system paths scrubbed to <path> (originals preserved in the JSON sidecar)
